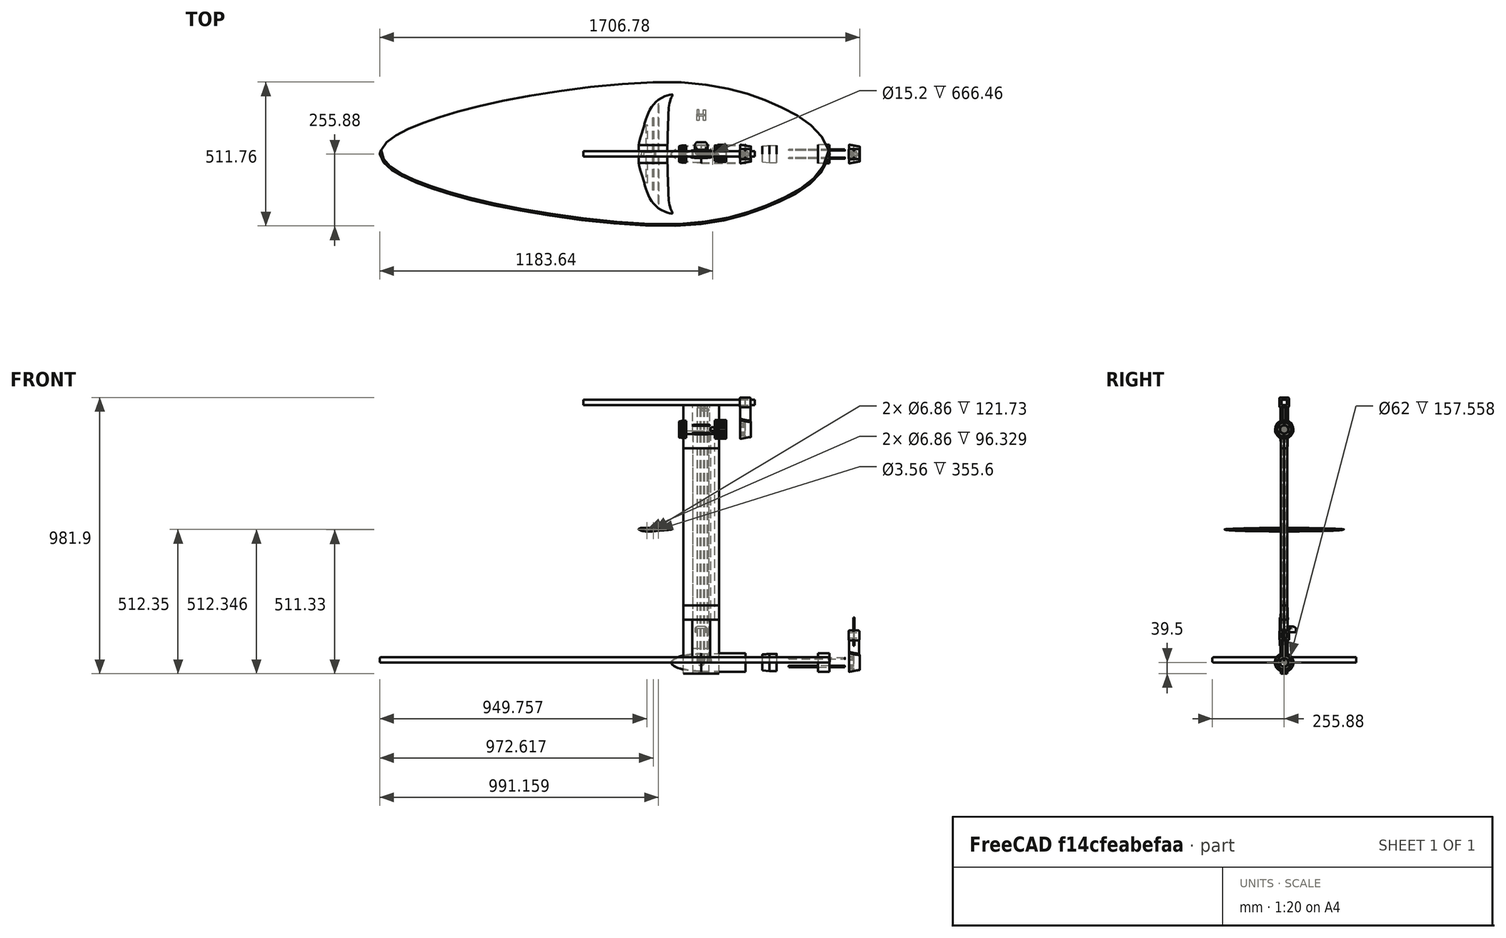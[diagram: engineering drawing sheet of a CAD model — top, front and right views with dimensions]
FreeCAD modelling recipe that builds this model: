
FCSTD DOCUMENT  (FreeCAD 0.21R33771 (Git))
Label: fullboard
License: All rights reserved
LicenseURL: https://en.wikipedia.org/wiki/All_rights_reserved
objects: Sketcher::SketchObject×75, Part::Cylinder×72, PartDesign::Body×57, Part::Cut×45, Part::Box×36, PartDesign::Pad×34, Part::MultiFuse×26, App::DocumentObjectGroup×21, Part::Feature×16, PartDesign::AdditiveLoft×12, Part::RegularPolygon×11, Part::Extrusion×11, App::Part×11, PartDesign::FeatureBase×8, Part::Mirroring×7, Part::Compound×7, Part::Fillet×6, PartDesign::Fillet×4, Mesh::Feature×4, Part::Chamfer×4, +10 more types
note: 500 computed .brp shape members not serialized (recipe doc carries the construction recipe); baked Part::Feature solids carry a one-line shape summary decoded from their .brp

FEATURE [Sketcher::SketchObject] Sketch001
  FullyConstrained = true
  MapMode = 5
  Support = -> [XY_Plane001]
  sketch-geometry (30):
    g0-g6: Circle x7 (B-spline internal-alignment scaffolding for g7; pole/knot coordinates omitted)
    g7: BSplineCurve PolesCount=7 KnotsCount=5 Degree=3 IsPeriodic=0
    g8-g12: GeomPoint x5 (B-spline internal-alignment scaffolding for g7; pole/knot coordinates omitted)
    g13-g19: Circle x7 (B-spline internal-alignment scaffolding for g20; pole/knot coordinates omitted)
    g20: BSplineCurve PolesCount=7 KnotsCount=5 Degree=3 IsPeriodic=0
    g21-g25: GeomPoint x5 (B-spline internal-alignment scaffolding for g20; pole/knot coordinates omitted)
    g26: LineSegment StartX=-28.575 StartY=9.525 StartZ=0 EndX=28.575 EndY=9.525 EndZ=0
    g27: LineSegment StartX=28.575 StartY=9.525 StartZ=0 EndX=28.575 EndY=-9.525 EndZ=0
    g28: LineSegment StartX=28.575 StartY=-9.525 StartZ=0 EndX=-28.575 EndY=-9.525 EndZ=0
    g29: LineSegment StartX=-28.575 StartY=-9.525 StartZ=0 EndX=-28.575 EndY=9.525 EndZ=0
  constraints (40):
    c: Weight(g0) = 1
    c: PointOnObject(g7,g-1)
    c: Equal(g0, g1-g6) x6
    c: PointOnObject(g7,g-1)
    c: InternalAlignment(g0-g6 -> g7) x7
    c: InternalAlignment(g8-g12 -> g7) x5
    c: Weight(g13) = 1
    c: Coincident(g20,g7)
    c: Equal(g13, g14-g19) x6
    c: Coincident(g20,g7)
    c: InternalAlignment(g13-g19 -> g20) x7
    c: InternalAlignment(g21-g25 -> g20) x5
    c: Symmetric(g5,g18,g-1)
    c: Symmetric(g17,g4,g-1)
    c: Symmetric(g16,g3,g-1)
    c: Symmetric(g15,g2,g-1)
    c: Symmetric(g14,g1,g-1)
    c: Coincident(g26,g27)
    c: Coincident(g27,g28)
    c: Coincident(g28,g29)
    c: Coincident(g29,g26)
    c: Horizontal(g26)
    c: Horizontal(g28)
    c: Vertical(g27)
    c: Vertical(g29)
    c: DistanceX(g26,g26) = 57.15
    c: DistanceX(g26,g-1) = 28.575
    c: DistanceY(g27,g26) = 19.05
    c: DistanceY(g27,g-1) = 9.525
    c: DistanceY(g26,g9) = 1
    c: DistanceX(g9,g26) = 1
    c: DistanceY(g26,g3) = 1.5
    c: DistanceY(g26,g11) = 1
    c: DistanceX(g26,g11) = 1
    c: Symmetric(g2,g4,g-2)
    c: DistanceX(g16,g-1) = 0
    c: DistanceX(g-1,g7) = 63.5
    c: DistanceX(g7,g-1) = 63.5
    c: DistanceY(g7,g5) = 7.1374
    c: DistanceX(g5,g7) = 16.5608
FEATURE [PartDesign::Pad] Pad001
  Direction = (0,0,1)
  Length = 863.6
  Length2 = 10
  Profile = -> Sketch001
  ReferenceAxis = -> Sketch001 [N_Axis]
  Type = 0
FEATURE [PartDesign::Body] Body001  label="Mast"
  Group = -> [Sketch001,Pad001]
  Origin = -> Origin001
  Placement = pos=(0,0,-39.497) rot=(0,0,1;0rad)
  Tip = -> Pad001
FEATURE [Sketcher::SketchObject] Sketch003
  FullyConstrained = true
  MapMode = 5
  Support = -> [XY_Plane002]
  sketch-geometry (32):
    g0: GeomPoint X=-1143 Y=0 Z=0
    g1: GeomPoint X=457.2 Y=0 Z=0
    g2-g9: Circle x8 (B-spline internal-alignment scaffolding for g10; pole/knot coordinates omitted)
    g10: BSplineCurve PolesCount=8 KnotsCount=6 Degree=3 IsPeriodic=0
    g11-g16: GeomPoint x6 (B-spline internal-alignment scaffolding for g10; pole/knot coordinates omitted)
    g17-g24: Circle x8 (B-spline internal-alignment scaffolding for g25; pole/knot coordinates omitted)
    g25: BSplineCurve PolesCount=8 KnotsCount=6 Degree=3 IsPeriodic=0
    g26-g31: GeomPoint x6 (B-spline internal-alignment scaffolding for g25; pole/knot coordinates omitted)
  constraints (34):
    c: PointOnObject(g0,g-1)
    c: DistanceX(g0,g-1) = 1143
    c: PointOnObject(g1,g-1)
    c: DistanceX(g-1,g1) = 457.2
    c: Weight(g2) = 1
    c: Coincident(g10,g0)
    c: Equal(g2, g3-g9) x7
    c: Coincident(g10,g1)
    c: InternalAlignment(g2-g9 -> g10) x8
    c: InternalAlignment(g11-g16 -> g10) x6
    c: Weight(g17) = 1
    c: Coincident(g25,g10)
    c: Equal(g17, g18-g24) x7
    c: Coincident(g25,g10)
    c: InternalAlignment(g17-g24 -> g25) x8
    c: InternalAlignment(g26-g31 -> g25) x6
    c: Symmetric(g8,g23,g-1)
    c: Symmetric(g7,g22,g-1)
    c: Symmetric(g6,g21,g-1)
    c: Symmetric(g5,g20,g-1)
    c: Symmetric(g4,g19,g-1)
    c: Symmetric(g3,g18,g-1)
    c: DistanceX(g8) = 435.486
    c: DistanceY(g8) = 90.2091
    c: DistanceX(g7) = 267.582
    c: DistanceY(g7) = 186.903
    c: DistanceX(g6) = -45.8772
    c: DistanceY(g6) = 284.203
    c: DistanceX(g5) = -655.352
    c: DistanceY(g5) = 209.349
    c: DistanceX(g4) = -999.419
    c: DistanceY(g4) = 118.665
    c: DistanceX(g3) = -1133.96
    c: DistanceY(g3) = 47.2203
FEATURE [PartDesign::Pad] Pad002
  Direction = (0,0,1)
  Length = 19.05
  Length2 = 10
  Profile = -> Sketch003
  ReferenceAxis = -> Sketch003 [N_Axis]
  Type = 0
FEATURE [PartDesign::Fillet] Fillet
  Base = -> Pad002 [Edge6]
  BaseFeature = -> Pad002
  Radius = 6.35
  SupportTransform = false
  UseAllEdges = false
FEATURE [PartDesign::Fillet] Fillet001
  Base = -> Fillet [Edge8]
  BaseFeature = -> Fillet
  Radius = 5.08
  SupportTransform = false
  UseAllEdges = false
FEATURE [PartDesign::Body] Body002  label="Board"
  Group = -> [Sketch003,Pad002,Fillet,Fillet001]
  Origin = -> Origin002
  Tip = -> Fillet001
FEATURE [Sketcher::SketchObject] Sketch006
  FullyConstrained = true
  MapMode = 5
  Placement = pos=(0,0,0) rot=(1,0,0;1.5708rad)
  Support = -> [XZ_Plane007]
  sketch-geometry (9):
    g0-g4: Circle x5 (B-spline internal-alignment scaffolding for g5; pole/knot coordinates omitted)
    g5: BSplineCurve PolesCount=5 KnotsCount=3 Degree=3 IsPeriodic=0
    g6: GeomPoint X=-61.1896 Y=1.55299 Z=0
    g7: GeomPoint X=141.928 Y=11.8848 Z=0
    g8: GeomPoint X=-61.1896 Y=1.55299 Z=0
  constraints (15):
    c: Weight(g0) = 1
    c: Equal(g0, g1-g4) x4
    c: Coincident(g5,g0)
    c: InternalAlignment(g0-g4 -> g5) x5
    c: InternalAlignment(g6,g5)
    c: InternalAlignment(g7,g5)
    c: InternalAlignment(g8,g5)
    c: DistanceX(g3) = 103.059
    c: DistanceY(g3) = -5.38655
    c: DistanceX(g1) = 89.7287
    c: DistanceY(g1) = 37.6307
    c: DistanceX(g2) = 187.462
    c: DistanceY(g2) = 7.64757
    c: DistanceX(g5) = -61.1896
    c: DistanceY(g5) = 1.55299
FEATURE [Part::Part2DObjectPython] Clone2D001  label="Wing100"  # Draft 2D object (typed FeaturePython)
  Fuse = false
  Placement = pos=(0,0,0) rot=(1,0,0;1.5708rad)
  Scale = (1,1,1)
FEATURE [Sketcher::SketchObject] Sketch007  label="Wing5"
  FullyConstrained = false
  Placement = pos=(-95.25,284.48,0) rot=(0.995037,0,0.099504;1.5708rad)
  sketch-geometry (1):
    g0: BSplineCurve PolesCount=5 KnotsCount=3 Degree=3 IsPeriodic=0
FEATURE [Sketcher::SketchObject] Sketch008  label="Wing4"
  FullyConstrained = false
  Placement = pos=(-88.9,279.4,0) rot=(0.998205,0,0.059892;1.5708rad)
  sketch-geometry (1):
    g0: BSplineCurve PolesCount=5 KnotsCount=3 Degree=3 IsPeriodic=0
FEATURE [Sketcher::SketchObject] Sketch009  label="Wing3"
  FullyConstrained = false
  Placement = pos=(-63.5,254,0) rot=(0.999201,0,0.039968;1.5708rad)
  sketch-geometry (1):
    g0: BSplineCurve PolesCount=5 KnotsCount=3 Degree=3 IsPeriodic=0
FEATURE [Sketcher::SketchObject] Sketch010  label="Wing2"
  FullyConstrained = false
  Placement = pos=(-25.4,152.4,0) rot=(0.9998,0,0.019996;1.5708rad)
  sketch-geometry (1):
    g0: BSplineCurve PolesCount=5 KnotsCount=3 Degree=3 IsPeriodic=0
FEATURE [Sketcher::SketchObject] Sketch011  label="Wing1"
  FullyConstrained = false
  Placement = pos=(0,-76.2,0) rot=(1,0,0;1.5708rad)
  sketch-geometry (1):
    g0: BSplineCurve PolesCount=5 KnotsCount=3 Degree=3 IsPeriodic=0
FEATURE [Sketcher::SketchObject] Sketch012  label="Wing1.5"
  FullyConstrained = false
  Placement = pos=(-12.7,50.8,0) rot=(-1,0,0;1.5708rad)
  sketch-geometry (1):
    g0: BSplineCurve PolesCount=5 KnotsCount=3 Degree=3 IsPeriodic=0
FEATURE [Sketcher::SketchObject] Sketch013  label="Wing1.25"
  FullyConstrained = false
  Placement = pos=(-3.81,-25.4,0) rot=(-1,0,0;1.5708rad)
  sketch-geometry (1):
    g0: BSplineCurve PolesCount=5 KnotsCount=3 Degree=3 IsPeriodic=0
FEATURE [Sketcher::SketchObject] Sketch014  label="Wing0"
  FullyConstrained = false
  Placement = pos=(0,-139.7,0) rot=(-1,0,0;1.5708rad)
  sketch-geometry (1):
    g0: BSplineCurve PolesCount=5 KnotsCount=3 Degree=3 IsPeriodic=0
FEATURE [Sketcher::SketchObject] Sketch015  label="Wing-1"
  FullyConstrained = false
  Placement = pos=(0,-177.8,0) rot=(-1,0,0;1.5708rad)
  sketch-geometry (1):
    g0: BSplineCurve PolesCount=5 KnotsCount=3 Degree=3 IsPeriodic=0
FEATURE [PartDesign::Body] Body007  label="Front Wing"
  Group = -> [Sketch006,Clone2D001,Sketch015]
  Origin = -> Origin007
FEATURE [PartDesign::AdditiveLoft] AdditiveLoft
  Closed = false
  Placement = pos=(-95.25,284.48,0) rot=(0.995037,0,0.099504;1.5708rad)
  Profile = -> Sketch007 [Edge1]
  Ruled = false
  Sections = -> [Sketch008,Sketch009,Sketch010,Sketch012,Sketch013,Sketch011]
FEATURE [PartDesign::AdditiveLoft] AdditiveLoft001
  BaseFeature = -> AdditiveLoft
  Closed = false
  Placement = pos=(-95.25,284.48,0) rot=(0.995037,0,0.099504;1.5708rad)
  Profile = -> Sketch011
  Ruled = false
  Sections = -> [Sketch014]
FEATURE [Part::Mirroring] Part__Mirroring  label="AdditiveLoft001 (Mirror #1)"
  Base = (0,0,0)
  Normal = (0,0,1)
  Placement = pos=(0,-279.4,3.1e-14) rot=(1,0,0;3.14159rad)
  Source = -> AdditiveLoft001
FEATURE [Sketcher::SketchObject] Sketch016
  FullyConstrained = true
  MapMode = 5
  Support = -> [XY_Plane008]
FEATURE [PartDesign::Body] Body008  label="Body"
  Group = -> [Sketch016]
  Origin = -> Origin008
FEATURE [Sketcher::SketchObject] Sketch017
  FullyConstrained = true
  MapMode = 5
  Placement = pos=(0,0,0) rot=(0.57735,0.57735,0.57735;2.0944rad)
  Support = -> [YZ_Plane009]
  sketch-geometry (4):
    g0: LineSegment StartX=-6.35 StartY=-12.7 StartZ=0 EndX=12.7 EndY=-12.7 EndZ=0
    g1: LineSegment StartX=12.7 StartY=-12.7 StartZ=0 EndX=12.7 EndY=6.35 EndZ=0
    g2: LineSegment StartX=12.7 StartY=6.35 StartZ=0 EndX=-6.35 EndY=6.35 EndZ=0
    g3: LineSegment StartX=-6.35 StartY=6.35 StartZ=0 EndX=-6.35 EndY=-12.7 EndZ=0
  constraints (12):
    c: Coincident(g0,g1)
    c: Coincident(g1,g2)
    c: Coincident(g2,g3)
    c: Coincident(g3,g0)
    c: Horizontal(g0)
    c: Horizontal(g2)
    c: Vertical(g1)
    c: Vertical(g3)
    c: DistanceY(g0,g1) = 19.05
    c: DistanceX(g2,g1) = 19.05
    c: DistanceX(g2) = -6.35
    c: DistanceY(g2) = 6.35
FEATURE [PartDesign::Pad] Pad003
  Direction = (1,-2e-16,3e-16)
  Length = 609.6
  Length2 = 10
  Placement = pos=(0,0,0) rot=(0.57735,0.57735,0.57735;2.0944rad)
  Profile = -> Sketch017
  ReferenceAxis = -> Sketch017 [N_Axis]
  Type = 0
FEATURE [PartDesign::Body] Body009  label="Fuselage"
  Group = -> [Sketch017,Pad003]
  Origin = -> Origin009
  Placement = pos=(-418.998,-3.175,928.688) rot=(0,0,1;0rad)
  Tip = -> Pad003
FEATURE [Sketcher::SketchObject] Sketch018
  FullyConstrained = true
  MapMode = 5
  Support = -> [XY_Plane010]
  sketch-geometry (16):
    g0: LineSegment StartX=-14.2219 StartY=6.35 StartZ=0 EndX=23.8781 EndY=6.35 EndZ=0
    g1: LineSegment StartX=23.8781 StartY=6.35 StartZ=0 EndX=23.8781 EndY=-6.35 EndZ=0
    g2: LineSegment StartX=23.8781 StartY=-6.35 StartZ=0 EndX=-14.2219 EndY=-6.35 EndZ=0
    g3: LineSegment StartX=-14.2219 StartY=-6.35 StartZ=0 EndX=-14.2219 EndY=6.35 EndZ=0
    g4: LineSegment StartX=-12.6217 StartY=4.7498 StartZ=0 EndX=-3.12209 EndY=4.7498 EndZ=0
    g5: LineSegment StartX=-3.12209 StartY=4.7498 StartZ=0 EndX=-3.12209 EndY=-4.7498 EndZ=0
    g6: LineSegment StartX=-3.12209 StartY=-4.7498 StartZ=0 EndX=-12.6217 EndY=-4.7498 EndZ=0
    g7: LineSegment StartX=-12.6217 StartY=-4.7498 StartZ=0 EndX=-12.6217 EndY=4.7498 EndZ=0
    g8: LineSegment StartX=0.078306 StartY=4.7498 StartZ=0 EndX=9.57791 EndY=4.7498 EndZ=0
    g9: LineSegment StartX=9.57791 StartY=4.7498 StartZ=0 EndX=9.57791 EndY=-4.7498 EndZ=0
    g10: LineSegment StartX=9.57791 StartY=-4.7498 StartZ=0 EndX=0.078306 EndY=-4.7498 EndZ=0
    g11: LineSegment StartX=0.078306 StartY=-4.7498 StartZ=0 EndX=0.078306 EndY=4.7498 EndZ=0
    g12: LineSegment StartX=12.7783 StartY=4.7498 StartZ=0 EndX=22.2779 EndY=4.7498 EndZ=0
    g13: LineSegment StartX=22.2779 StartY=4.7498 StartZ=0 EndX=22.2779 EndY=-4.7498 EndZ=0
    g14: LineSegment StartX=22.2779 StartY=-4.7498 StartZ=0 EndX=12.7783 EndY=-4.7498 EndZ=0
    g15: LineSegment StartX=12.7783 StartY=-4.7498 StartZ=0 EndX=12.7783 EndY=4.7498 EndZ=0
  constraints (48):
    c: Coincident(g0,g1)
    c: Coincident(g1,g2)
    c: Coincident(g2,g3)
    c: Coincident(g3,g0)
    c: Horizontal(g0)
    c: Horizontal(g2)
    c: Vertical(g1)
    c: Vertical(g3)
    c: Coincident(g4,g5)
    c: Coincident(g5,g6)
    c: Coincident(g6,g7)
    c: Coincident(g7,g4)
    c: Horizontal(g4)
    c: Horizontal(g6)
    c: Vertical(g5)
    c: Vertical(g7)
    c: Coincident(g8,g9)
    c: Coincident(g9,g10)
    c: Coincident(g10,g11)
    c: Coincident(g11,g8)
    c: Horizontal(g8)
    c: Horizontal(g10)
    c: Vertical(g9)
    c: Vertical(g11)
    c: Coincident(g12,g13)
    c: Coincident(g13,g14)
    c: Coincident(g14,g15)
    c: Coincident(g15,g12)
    c: Horizontal(g12)
    c: Horizontal(g14)
    c: Vertical(g13)
    c: Vertical(g15)
    c: DistanceX(g0,g0) = 38.1
    c: DistanceX(g4,g8) = 3.2004
    c: DistanceX(g8,g12) = 3.2004
    c: DistanceY(g8,g4) = 0
    c: DistanceY(g12,g8) = 0
    c: DistanceY(g2,g6) = 1.6002
    c: DistanceY(g2,g0) = 12.7
    c: DistanceY(g-1,g0) = 6.35
    c: DistanceY(g10,g5) = 0
    c: DistanceY(g14,g9) = 0
    c: DistanceY(g12,g0) = 1.6002
    c: DistanceX(g0,g4) = 1.6002
    c: DistanceX(g0) = -14.2219
    c: DistanceX(g4,g4) = 9.4996
    c: DistanceX(g8,g8) = 9.4996
    c: DistanceX(g12,g12) = 9.4996
FEATURE [PartDesign::Pad] Pad004
  Direction = (0,0,1)
  Length = 914.4
  Length2 = 10
  Profile = -> Sketch018
  ReferenceAxis = -> Sketch018 [N_Axis]
  Type = 0
FEATURE [PartDesign::Body] Body010  label="MastStruct"
  Group = -> [Sketch018,Pad004]
  Origin = -> Origin010
  Tip = -> Pad004
FEATURE [Part::Cylinder] Cylinder
  Angle = 360
  AttacherType = Attacher::AttachEngine3D
  FirstAngle = 0
  Height = 25.4
  Placement = pos=(5.076,0.2286,901.442) rot=(0,0,1;0rad)
  Radius = 3.175
  SecondAngle = 0
FEATURE [Sketcher::SketchObject] Sketch019
  FullyConstrained = true
  MapMode = 5
  Placement = pos=(0,0,0) rot=(1,0,0;1.5708rad)
  Support = -> [XZ_Plane011]
  sketch-geometry (8):
    g0: LineSegment StartX=4.08905 StartY=-9.05917 StartZ=0 EndX=13.6141 EndY=-9.05917 EndZ=0
    g1: LineSegment StartX=13.6141 StartY=-9.05917 StartZ=0 EndX=13.6141 EndY=-18.5842 EndZ=0
    g2: LineSegment StartX=13.6141 StartY=-18.5842 StartZ=0 EndX=4.08905 EndY=-18.5842 EndZ=0
    g3: LineSegment StartX=4.08905 StartY=-18.5842 StartZ=0 EndX=4.08905 EndY=-9.05917 EndZ=0
    g4: LineSegment StartX=4.97805 StartY=-9.94817 StartZ=0 EndX=12.7251 EndY=-9.94817 EndZ=0
    g5: LineSegment StartX=12.7251 StartY=-9.94817 StartZ=0 EndX=12.7251 EndY=-17.6952 EndZ=0
    g6: LineSegment StartX=12.7251 StartY=-17.6952 StartZ=0 EndX=4.97805 EndY=-17.6952 EndZ=0
    g7: LineSegment StartX=4.97805 StartY=-17.6952 StartZ=0 EndX=4.97805 EndY=-9.94817 EndZ=0
  constraints (24):
    c: Coincident(g0,g1)
    c: Coincident(g1,g2)
    c: Coincident(g2,g3)
    c: Coincident(g3,g0)
    c: Horizontal(g0)
    c: Horizontal(g2)
    c: Vertical(g1)
    c: Vertical(g3)
    c: Coincident(g4,g5)
    c: Coincident(g5,g6)
    c: Coincident(g6,g7)
    c: Coincident(g7,g4)
    c: Horizontal(g4)
    c: Horizontal(g6)
    c: Vertical(g5)
    c: Vertical(g7)
    c: DistanceX(g0,g4) = 0.889
    c: DistanceX(g0,g0) = 9.525
    c: DistanceX(g4,g0) = 0.889
    c: DistanceY(g2,g0) = 9.525
    c: DistanceY(g4,g0) = 0.889
    c: DistanceY(g2,g6) = 0.889
    c: DistanceX(g0) = 4.08905
    c: DistanceY(g0) = -9.05917
FEATURE [PartDesign::Pad] Pad005
  Direction = (0,-1,2e-16)
  Length = 9.525
  Length2 = 10
  Placement = pos=(0,0,0) rot=(1,0,0;1.5708rad)
  Profile = -> Sketch019
  ReferenceAxis = -> Sketch019 [N_Axis]
  Type = 0
FEATURE [PartDesign::Body] Body011  label="SteelConnector1"
  Group = -> [Sketch019,Pad005]
  Origin = -> Origin011
  Placement = pos=(-16.764,4.826,923.29) rot=(0,0,1;0rad)
  Tip = -> Pad005
FEATURE [Sketcher::SketchObject] Sketch020
  FullyConstrained = true
  MapMode = 5
  Placement = pos=(0,0,0) rot=(1,0,0;1.5708rad)
  Support = -> [XZ_Plane012]
  sketch-geometry (8):
    g0: LineSegment StartX=4.08905 StartY=-9.05917 StartZ=0 EndX=13.6141 EndY=-9.05917 EndZ=0
    g1: LineSegment StartX=13.6141 StartY=-9.05917 StartZ=0 EndX=13.6141 EndY=-18.5842 EndZ=0
    g2: LineSegment StartX=13.6141 StartY=-18.5842 StartZ=0 EndX=4.08905 EndY=-18.5842 EndZ=0
    g3: LineSegment StartX=4.08905 StartY=-18.5842 StartZ=0 EndX=4.08905 EndY=-9.05917 EndZ=0
    g4: LineSegment StartX=4.97805 StartY=-9.94817 StartZ=0 EndX=12.7251 EndY=-9.94817 EndZ=0
    g5: LineSegment StartX=12.7251 StartY=-9.94817 StartZ=0 EndX=12.7251 EndY=-17.6952 EndZ=0
    g6: LineSegment StartX=12.7251 StartY=-17.6952 StartZ=0 EndX=4.97805 EndY=-17.6952 EndZ=0
    g7: LineSegment StartX=4.97805 StartY=-17.6952 StartZ=0 EndX=4.97805 EndY=-9.94817 EndZ=0
  constraints (24):
    c: Coincident(g0,g1)
    c: Coincident(g1,g2)
    c: Coincident(g2,g3)
    c: Coincident(g3,g0)
    c: Horizontal(g0)
    c: Horizontal(g2)
    c: Vertical(g1)
    c: Vertical(g3)
    c: Coincident(g4,g5)
    c: Coincident(g5,g6)
    c: Coincident(g6,g7)
    c: Coincident(g7,g4)
    c: Horizontal(g4)
    c: Horizontal(g6)
    c: Vertical(g5)
    c: Vertical(g7)
    c: DistanceX(g0,g4) = 0.889
    c: DistanceX(g0,g0) = 9.525
    c: DistanceX(g4,g0) = 0.889
    c: DistanceY(g2,g0) = 9.525
    c: DistanceY(g4,g0) = 0.889
    c: DistanceY(g2,g6) = 0.889
    c: DistanceX(g0) = 4.08905
    c: DistanceY(g0) = -9.05917
FEATURE [PartDesign::Pad] Pad006
  Direction = (0,-1,2e-16)
  Length = 9.525
  Length2 = 10
  Placement = pos=(0,0,0) rot=(1,0,0;1.5708rad)
  Profile = -> Sketch020
  ReferenceAxis = -> Sketch020 [N_Axis]
  Type = 0
FEATURE [PartDesign::Body] Body012  label="SteelConnector2"
  Group = -> [Sketch020,Pad006]
  Origin = -> Origin012
  Placement = pos=(-4.064,4.826,923.29) rot=(0,0,1;0rad)
  Tip = -> Pad006
FEATURE [Sketcher::SketchObject] Sketch021
  FullyConstrained = true
  MapMode = 5
  Placement = pos=(0,0,0) rot=(1,0,0;1.5708rad)
  Support = -> [XZ_Plane013]
  sketch-geometry (8):
    g0: LineSegment StartX=4.08905 StartY=-9.05917 StartZ=0 EndX=13.6141 EndY=-9.05917 EndZ=0
    g1: LineSegment StartX=13.6141 StartY=-9.05917 StartZ=0 EndX=13.6141 EndY=-18.5842 EndZ=0
    g2: LineSegment StartX=13.6141 StartY=-18.5842 StartZ=0 EndX=4.08905 EndY=-18.5842 EndZ=0
    g3: LineSegment StartX=4.08905 StartY=-18.5842 StartZ=0 EndX=4.08905 EndY=-9.05917 EndZ=0
    g4: LineSegment StartX=4.97805 StartY=-9.94817 StartZ=0 EndX=12.7251 EndY=-9.94817 EndZ=0
    g5: LineSegment StartX=12.7251 StartY=-9.94817 StartZ=0 EndX=12.7251 EndY=-17.6952 EndZ=0
    g6: LineSegment StartX=12.7251 StartY=-17.6952 StartZ=0 EndX=4.97805 EndY=-17.6952 EndZ=0
    g7: LineSegment StartX=4.97805 StartY=-17.6952 StartZ=0 EndX=4.97805 EndY=-9.94817 EndZ=0
  constraints (24):
    c: Coincident(g0,g1)
    c: Coincident(g1,g2)
    c: Coincident(g2,g3)
    c: Coincident(g3,g0)
    c: Horizontal(g0)
    c: Horizontal(g2)
    c: Vertical(g1)
    c: Vertical(g3)
    c: Coincident(g4,g5)
    c: Coincident(g5,g6)
    c: Coincident(g6,g7)
    c: Coincident(g7,g4)
    c: Horizontal(g4)
    c: Horizontal(g6)
    c: Vertical(g5)
    c: Vertical(g7)
    c: DistanceX(g0,g4) = 0.889
    c: DistanceX(g0,g0) = 9.525
    c: DistanceX(g4,g0) = 0.889
    c: DistanceY(g2,g0) = 9.525
    c: DistanceY(g4,g0) = 0.889
    c: DistanceY(g2,g6) = 0.889
    c: DistanceX(g0) = 4.08905
    c: DistanceY(g0) = -9.05917
FEATURE [PartDesign::Pad] Pad007
  Direction = (0,-1,2e-16)
  Length = 9.525
  Length2 = 10
  Placement = pos=(0,0,0) rot=(1,0,0;1.5708rad)
  Profile = -> Sketch021
  ReferenceAxis = -> Sketch021 [N_Axis]
  Type = 0
FEATURE [PartDesign::Body] Body013  label="SteelConnector3"
  Group = -> [Sketch021,Pad007]
  Origin = -> Origin013
  Placement = pos=(8.636,4.826,923.29) rot=(0,0,1;0rad)
  Tip = -> Pad007
FEATURE [PartDesign::FeatureBase] BaseFeature
  BaseFeature = -> Cylinder
FEATURE [PartDesign::Body] Body014
  BaseFeature = -> Cylinder
  Group = -> [BaseFeature]
  Origin = -> Origin014
  Placement = pos=(27.2502,0,897.747) rot=(0,-1,0;1.5708rad)
  Tip = -> BaseFeature
FEATURE [App::DocumentObjectGroup] Group  label="Steel Connectors"
  Group = -> [Body011,Body012,Body013,Body014]
FEATURE [Part::Helix] Helix
  Angle = 0
  AttacherType = Attacher::AttachEngine3D
  Height = 50.8
  LocalCoord = 0
  Pitch = 0.999998
  Radius = 2.38125
  SegmentLength = 0
  Style = 1
FEATURE [App::DocumentObjectGroup] Group001  label="Front Wing Support"
FEATURE [Sketcher::SketchObject] Sketch022
  FullyConstrained = true
  MapMode = 5
  Placement = pos=(0,0,0) rot=(1,0,0;1.5708rad)
  Support = -> [XZ_Plane015]
  sketch-geometry (8):
    g0: LineSegment StartX=0 StartY=0 StartZ=0 EndX=12.7 EndY=0 EndZ=0
    g1: LineSegment StartX=12.7 StartY=0 StartZ=0 EndX=12.7 EndY=-12.7 EndZ=0
    g2: LineSegment StartX=12.7 StartY=-12.7 StartZ=0 EndX=0 EndY=-12.7 EndZ=0
    g3: LineSegment StartX=0 StartY=-12.7 StartZ=0 EndX=0 EndY=0 EndZ=0
    g4: LineSegment StartX=1.6002 StartY=-1.6002 StartZ=0 EndX=11.0998 EndY=-1.6002 EndZ=0
    g5: LineSegment StartX=11.0998 StartY=-1.6002 StartZ=0 EndX=11.0998 EndY=-11.0998 EndZ=0
    g6: LineSegment StartX=11.0998 StartY=-11.0998 StartZ=0 EndX=1.6002 EndY=-11.0998 EndZ=0
    g7: LineSegment StartX=1.6002 StartY=-11.0998 StartZ=0 EndX=1.6002 EndY=-1.6002 EndZ=0
  constraints (23):
    c: Coincident(g0,g1)
    c: Coincident(g1,g2)
    c: Coincident(g2,g3)
    c: Coincident(g3,g0)
    c: Horizontal(g0)
    c: Horizontal(g2)
    c: Vertical(g1)
    c: Vertical(g3)
    c: Coincident(g0,g-1)
    c: Coincident(g4,g5)
    c: Coincident(g5,g6)
    c: Coincident(g6,g7)
    c: Coincident(g7,g4)
    c: Horizontal(g4)
    c: Horizontal(g6)
    c: Vertical(g5)
    c: Vertical(g7)
    c: DistanceX(g2,g1) = 12.7
    c: DistanceY(g2,g0) = 12.7
    c: DistanceY(g2,g6) = 1.6002
    c: DistanceY(g4,g0) = 1.6002
    c: DistanceX(g0,g4) = 1.6002
    c: DistanceX(g4,g0) = 1.6002
FEATURE [PartDesign::Pad] Pad008
  Direction = (0,-1,-2e-16)
  Length = 152.4
  Length2 = 10
  Placement = pos=(0,0,0) rot=(1,0,0;1.5708rad)
  Profile = -> Sketch022
  ReferenceAxis = -> Sketch022 [N_Axis]
  Type = 0
FEATURE [PartDesign::Body] Body015  label="Body016"
  Group = -> [Sketch022,Pad008]
  Origin = -> Origin015
  Placement = pos=(-413.918,76.2,939.8) rot=(0,0,1;0rad)
  Tip = -> Pad008
FEATURE [Sketcher::SketchObject] Sketch023
  FullyConstrained = true
  MapMode = 5
  Placement = pos=(0,0,0) rot=(1,0,0;1.5708rad)
  Support = -> [XZ_Plane016]
  sketch-geometry (8):
    g0: LineSegment StartX=0 StartY=0 StartZ=0 EndX=12.7 EndY=0 EndZ=0
    g1: LineSegment StartX=12.7 StartY=0 StartZ=0 EndX=12.7 EndY=-12.7 EndZ=0
    g2: LineSegment StartX=12.7 StartY=-12.7 StartZ=0 EndX=0 EndY=-12.7 EndZ=0
    g3: LineSegment StartX=0 StartY=-12.7 StartZ=0 EndX=0 EndY=0 EndZ=0
    g4: LineSegment StartX=1.6002 StartY=-1.6002 StartZ=0 EndX=11.0998 EndY=-1.6002 EndZ=0
    g5: LineSegment StartX=11.0998 StartY=-1.6002 StartZ=0 EndX=11.0998 EndY=-11.0998 EndZ=0
    g6: LineSegment StartX=11.0998 StartY=-11.0998 StartZ=0 EndX=1.6002 EndY=-11.0998 EndZ=0
    g7: LineSegment StartX=1.6002 StartY=-11.0998 StartZ=0 EndX=1.6002 EndY=-1.6002 EndZ=0
  constraints (23):
    c: Coincident(g0,g1)
    c: Coincident(g1,g2)
    c: Coincident(g2,g3)
    c: Coincident(g3,g0)
    c: Horizontal(g0)
    c: Horizontal(g2)
    c: Vertical(g1)
    c: Vertical(g3)
    c: Coincident(g0,g-1)
    c: Coincident(g4,g5)
    c: Coincident(g5,g6)
    c: Coincident(g6,g7)
    c: Coincident(g7,g4)
    c: Horizontal(g4)
    c: Horizontal(g6)
    c: Vertical(g5)
    c: Vertical(g7)
    c: DistanceX(g2,g1) = 12.7
    c: DistanceY(g2,g0) = 12.7
    c: DistanceY(g2,g6) = 1.6002
    c: DistanceY(g4,g0) = 1.6002
    c: DistanceX(g0,g4) = 1.6002
    c: DistanceX(g4,g0) = 1.6002
FEATURE [PartDesign::Pad] Pad009
  Direction = (0,-1,-2e-16)
  Length = 381
  Length2 = 10
  Placement = pos=(0,0,0) rot=(1,0,0;1.5708rad)
  Profile = -> Sketch023
  ReferenceAxis = -> Sketch023 [N_Axis]
  Type = 0
FEATURE [PartDesign::Body] Body016  label="Body017"
  Group = -> [Sketch023,Pad009]
  Origin = -> Origin016
  Placement = pos=(-393.598,190.5,939.8) rot=(0,0,1;0rad)
  Tip = -> Pad009
FEATURE [Sketcher::SketchObject] Sketch024
  FullyConstrained = true
  MapMode = 5
  Placement = pos=(0,0,0) rot=(1,0,0;1.5708rad)
  Support = -> [XZ_Plane017]
  sketch-geometry (8):
    g0: LineSegment StartX=0 StartY=0 StartZ=0 EndX=12.7 EndY=0 EndZ=0
    g1: LineSegment StartX=12.7 StartY=0 StartZ=0 EndX=12.7 EndY=-12.7 EndZ=0
    g2: LineSegment StartX=12.7 StartY=-12.7 StartZ=0 EndX=0 EndY=-12.7 EndZ=0
    g3: LineSegment StartX=0 StartY=-12.7 StartZ=0 EndX=0 EndY=0 EndZ=0
    g4: LineSegment StartX=1.6002 StartY=-1.6002 StartZ=0 EndX=11.0998 EndY=-1.6002 EndZ=0
    g5: LineSegment StartX=11.0998 StartY=-1.6002 StartZ=0 EndX=11.0998 EndY=-11.0998 EndZ=0
    g6: LineSegment StartX=11.0998 StartY=-11.0998 StartZ=0 EndX=1.6002 EndY=-11.0998 EndZ=0
    g7: LineSegment StartX=1.6002 StartY=-11.0998 StartZ=0 EndX=1.6002 EndY=-1.6002 EndZ=0
  constraints (23):
    c: Coincident(g0,g1)
    c: Coincident(g1,g2)
    c: Coincident(g2,g3)
    c: Coincident(g3,g0)
    c: Horizontal(g0)
    c: Horizontal(g2)
    c: Vertical(g1)
    c: Vertical(g3)
    c: Coincident(g0,g-1)
    c: Coincident(g4,g5)
    c: Coincident(g5,g6)
    c: Coincident(g6,g7)
    c: Coincident(g7,g4)
    c: Horizontal(g4)
    c: Horizontal(g6)
    c: Vertical(g5)
    c: Vertical(g7)
    c: DistanceX(g2,g1) = 12.7
    c: DistanceY(g2,g0) = 12.7
    c: DistanceY(g2,g6) = 1.6002
    c: DistanceY(g4,g0) = 1.6002
    c: DistanceX(g0,g4) = 1.6002
    c: DistanceX(g4,g0) = 1.6002
FEATURE [PartDesign::Pad] Pad010
  Direction = (0,-1,-2e-16)
  Length = 50.8
  Length2 = 10
  Placement = pos=(0,0,0) rot=(1,0,0;1.5708rad)
  Profile = -> Sketch024
  ReferenceAxis = -> Sketch024 [N_Axis]
  Type = 0
FEATURE [PartDesign::Body] Body017  label="Body018"
  Group = -> [Sketch024,Pad010]
  Origin = -> Origin017
  Placement = pos=(139.7,-6.35,914.4) rot=(0,0,1;1.5708rad)
  Tip = -> Pad010
FEATURE [Sketcher::SketchObject] Sketch025
  FullyConstrained = true
  MapMode = 5
  Placement = pos=(0,0,0) rot=(1,0,0;1.5708rad)
  Support = -> [XZ_Plane018]
  sketch-geometry (8):
    g0: LineSegment StartX=0 StartY=0 StartZ=0 EndX=12.7 EndY=0 EndZ=0
    g1: LineSegment StartX=12.7 StartY=0 StartZ=0 EndX=12.7 EndY=-12.7 EndZ=0
    g2: LineSegment StartX=12.7 StartY=-12.7 StartZ=0 EndX=0 EndY=-12.7 EndZ=0
    g3: LineSegment StartX=0 StartY=-12.7 StartZ=0 EndX=0 EndY=0 EndZ=0
    g4: LineSegment StartX=1.6002 StartY=-1.6002 StartZ=0 EndX=11.0998 EndY=-1.6002 EndZ=0
    g5: LineSegment StartX=11.0998 StartY=-1.6002 StartZ=0 EndX=11.0998 EndY=-11.0998 EndZ=0
    g6: LineSegment StartX=11.0998 StartY=-11.0998 StartZ=0 EndX=1.6002 EndY=-11.0998 EndZ=0
    g7: LineSegment StartX=1.6002 StartY=-11.0998 StartZ=0 EndX=1.6002 EndY=-1.6002 EndZ=0
  constraints (23):
    c: Coincident(g0,g1)
    c: Coincident(g1,g2)
    c: Coincident(g2,g3)
    c: Coincident(g3,g0)
    c: Horizontal(g0)
    c: Horizontal(g2)
    c: Vertical(g1)
    c: Vertical(g3)
    c: Coincident(g0,g-1)
    c: Coincident(g4,g5)
    c: Coincident(g5,g6)
    c: Coincident(g6,g7)
    c: Coincident(g7,g4)
    c: Horizontal(g4)
    c: Horizontal(g6)
    c: Vertical(g5)
    c: Vertical(g7)
    c: DistanceX(g2,g1) = 12.7
    c: DistanceY(g2,g0) = 12.7
    c: DistanceY(g2,g6) = 1.6002
    c: DistanceY(g4,g0) = 1.6002
    c: DistanceX(g0,g4) = 1.6002
    c: DistanceX(g4,g0) = 1.6002
FEATURE [PartDesign::Pad] Pad011
  Direction = (0,-1,-2e-16)
  Length = 457.2
  Length2 = 10
  Placement = pos=(0,0,0) rot=(1,0,0;1.5708rad)
  Profile = -> Sketch025
  ReferenceAxis = -> Sketch025 [N_Axis]
  Type = 0
FEATURE [PartDesign::Body] Body018  label="Body019"
  Group = -> [Sketch025,Pad011]
  Origin = -> Origin018
  Placement = pos=(-368.198,228.6,939.8) rot=(0,0,1;0rad)
  Tip = -> Pad011
FEATURE [Sketcher::SketchObject] Sketch027
  FullyConstrained = true
  MapMode = 5
  Placement = pos=(0,0,0) rot=(1,0,0;1.5708rad)
  Support = -> [XZ_Plane020]
  sketch-geometry (8):
    g0: LineSegment StartX=0 StartY=0 StartZ=0 EndX=12.7 EndY=0 EndZ=0
    g1: LineSegment StartX=12.7 StartY=0 StartZ=0 EndX=12.7 EndY=-12.7 EndZ=0
    g2: LineSegment StartX=12.7 StartY=-12.7 StartZ=0 EndX=0 EndY=-12.7 EndZ=0
    g3: LineSegment StartX=0 StartY=-12.7 StartZ=0 EndX=0 EndY=0 EndZ=0
    g4: LineSegment StartX=1.6002 StartY=-1.6002 StartZ=0 EndX=11.0998 EndY=-1.6002 EndZ=0
    g5: LineSegment StartX=11.0998 StartY=-1.6002 StartZ=0 EndX=11.0998 EndY=-11.0998 EndZ=0
    g6: LineSegment StartX=11.0998 StartY=-11.0998 StartZ=0 EndX=1.6002 EndY=-11.0998 EndZ=0
    g7: LineSegment StartX=1.6002 StartY=-11.0998 StartZ=0 EndX=1.6002 EndY=-1.6002 EndZ=0
  constraints (23):
    c: Coincident(g0,g1)
    c: Coincident(g1,g2)
    c: Coincident(g2,g3)
    c: Coincident(g3,g0)
    c: Horizontal(g0)
    c: Horizontal(g2)
    c: Vertical(g1)
    c: Vertical(g3)
    c: Coincident(g0,g-1)
    c: Coincident(g4,g5)
    c: Coincident(g5,g6)
    c: Coincident(g6,g7)
    c: Coincident(g7,g4)
    c: Horizontal(g4)
    c: Horizontal(g6)
    c: Vertical(g5)
    c: Vertical(g7)
    c: DistanceX(g2,g1) = 12.7
    c: DistanceY(g2,g0) = 12.7
    c: DistanceY(g2,g6) = 1.6002
    c: DistanceY(g4,g0) = 1.6002
    c: DistanceX(g0,g4) = 1.6002
    c: DistanceX(g4,g0) = 1.6002
FEATURE [PartDesign::Pad] Pad013
  Direction = (0,-1,-2e-16)
  Length = 584.2
  Length2 = 10
  Placement = pos=(0,0,0) rot=(1,0,0;1.5708rad)
  Profile = -> Sketch027
  ReferenceAxis = -> Sketch027 [N_Axis]
  Type = 0
FEATURE [PartDesign::Body] Body020  label="Body021"
  Group = -> [Sketch027,Pad013]
  Origin = -> Origin020
  Placement = pos=(-347.878,292.1,939.8) rot=(0,0,1;0rad)
  Tip = -> Pad013
FEATURE [Part::Cylinder] Cylinder001
  Angle = 360
  AttacherType = Attacher::AttachEngine3D
  FirstAngle = 0
  Height = 9.906
  Placement = pos=(5.08,-0.86,911.35) rot=(0,0,1;0rad)
  Radius = 3.048
  SecondAngle = 0
FEATURE [Part::Cylinder] Cylinder002
  Angle = 360
  AttacherType = Attacher::AttachEngine3D
  FirstAngle = 0
  Height = 660.4
  Placement = pos=(-295.91,-330.2,937.768) rot=(-1,0,0;1.5708rad)
  Radius = 3.175
  SecondAngle = 0
FEATURE [Part::Cylinder] Cylinder004
  Angle = 360
  AttacherType = Attacher::AttachEngine3D
  FirstAngle = 0
  Height = 101.6
  Placement = pos=(144.78,-50.8,905.256) rot=(-1,0,0;1.5708rad)
  Radius = 1.5875
  SecondAngle = 0
  expr: .Placement.Base.z = 2.97 '
FEATURE [Part::Cylinder] Cylinder005
  Angle = 360
  AttacherType = Attacher::AttachEngine3D
  FirstAngle = 0
  Height = 203.2
  Placement = pos=(162.56,-101.6,905.26) rot=(-1,0,0;1.5708rad)
  Radius = 1.5875
  SecondAngle = 0
FEATURE [Part::Cylinder] Cylinder006
  Angle = 360
  AttacherType = Attacher::AttachEngine3D
  FirstAngle = 0
  Height = 304.8
  Placement = pos=(180.34,-152.4,905.26) rot=(-1,0,0;1.5708rad)
  Radius = 1.5875
  SecondAngle = 0
FEATURE [Part::Cylinder] Cylinder007
  Angle = 360
  AttacherType = Attacher::AttachEngine3D
  FirstAngle = 0
  Height = 355.6
  Placement = pos=(201.422,-177.8,903.935) rot=(-1,0,0;1.5708rad)
  Radius = 1.5875
  SecondAngle = 0
  expr: .Placement.Base.z = 2.97 '
FEATURE [Part::Cylinder] Cylinder008
  Angle = 360
  AttacherType = Attacher::AttachEngine3D
  FirstAngle = 0
  Height = 762
  Placement = pos=(-267.208,-381,942.086) rot=(-1,0,0;1.5708rad)
  Radius = 3.175
  SecondAngle = 0
FEATURE [Part::Box] Box  label="Cube"
  AttacherType = Attacher::AttachEngine3D
  Height = 127
  Length = 914.4
  Placement = pos=(-692,-203.2,25.4) rot=(0,0,1;0rad)
  Width = 406.4
FEATURE [Part::Cylinder] Cylinder009  label="BatteryCell001"
  Angle = 360
  AttacherType = Attacher::AttachEngine3D
  FirstAngle = 0
  Height = 69.85
  Placement = pos=(0,45.212,36.9999) rot=(0,0,1;0rad)
  Radius = 10.414
  SecondAngle = 0
FEATURE [Part::Cylinder] Cylinder010  label="BatteryCell002"
  Angle = 360
  AttacherType = Attacher::AttachEngine3D
  FirstAngle = 0
  Height = 69.85
  Placement = pos=(0,22.606,36.9999) rot=(0,0,1;0rad)
  Radius = 10.414
  SecondAngle = 0
FEATURE [Part::Cylinder] Cylinder011  label="BatteryCell003"
  Angle = 360
  AttacherType = Attacher::AttachEngine3D
  FirstAngle = 0
  Height = 69.85
  Placement = pos=(0,0,36.9999) rot=(0,0,1;0rad)
  Radius = 10.414
  SecondAngle = 0
FEATURE [Part::Cylinder] Cylinder012  label="BatteryCell004"
  Angle = 360
  AttacherType = Attacher::AttachEngine3D
  FirstAngle = 0
  Height = 69.85
  Placement = pos=(0,-22.606,36.9999) rot=(0,0,1;0rad)
  Radius = 10.414
  SecondAngle = 0
FEATURE [Part::Cylinder] Cylinder013  label="BatteryCell005"
  Angle = 360
  AttacherType = Attacher::AttachEngine3D
  FirstAngle = 0
  Height = 69.85
  Placement = pos=(0,-45.212,36.9999) rot=(0,0,1;0rad)
  Radius = 10.414
  SecondAngle = 0
FEATURE [Part::Cylinder] Cylinder014  label="BatteryCell006"
  Angle = 360
  AttacherType = Attacher::AttachEngine3D
  FirstAngle = 0
  Height = 69.85
  Placement = pos=(0,-67.818,36.9999) rot=(0,0,1;0rad)
  Radius = 10.414
  SecondAngle = 0
FEATURE [Part::Cylinder] Cylinder003  label="BatteryCell000"
  Angle = 360
  AttacherType = Attacher::AttachEngine3D
  FirstAngle = 0
  Height = 69.85
  Placement = pos=(0,67.818,36.9999) rot=(0,0,1;0rad)
  Radius = 10.414
  SecondAngle = 0
FEATURE [Part::Compound] Compound  label="Row"
  Links = -> [Cylinder014,Cylinder013,Cylinder012,Cylinder011,Cylinder010,Cylinder009,Cylinder003]
  Placement = pos=(-254,0,0) rot=(0,0,1;0rad)
FEATURE [App::DocumentObjectGroup] Group004  label="Base"
  Group = -> [Cylinder003,Cylinder009,Cylinder010,Cylinder011,Cylinder012,Cylinder013,Cylinder014]
FEATURE [Part::Cylinder] Cylinder015  label="BatteryCell007"
  Angle = 360
  AttacherType = Attacher::AttachEngine3D
  FirstAngle = 0
  Height = 69.85
  Placement = pos=(0,67.818,36.9999) rot=(0,0,1;0rad)
  Radius = 10.414
  SecondAngle = 0
FEATURE [Part::Cylinder] Cylinder016  label="BatteryCell008"
  Angle = 360
  AttacherType = Attacher::AttachEngine3D
  FirstAngle = 0
  Height = 69.85
  Placement = pos=(0,45.212,36.9999) rot=(0,0,1;0rad)
  Radius = 10.414
  SecondAngle = 0
FEATURE [Part::Cylinder] Cylinder017  label="BatteryCell009"
  Angle = 360
  AttacherType = Attacher::AttachEngine3D
  FirstAngle = 0
  Height = 69.85
  Placement = pos=(0,22.606,36.9999) rot=(0,0,1;0rad)
  Radius = 10.414
  SecondAngle = 0
FEATURE [Part::Cylinder] Cylinder018  label="BatteryCell010"
  Angle = 360
  AttacherType = Attacher::AttachEngine3D
  FirstAngle = 0
  Height = 69.85
  Placement = pos=(0,0,36.9999) rot=(0,0,1;0rad)
  Radius = 10.414
  SecondAngle = 0
FEATURE [Part::Cylinder] Cylinder019  label="BatteryCell011"
  Angle = 360
  AttacherType = Attacher::AttachEngine3D
  FirstAngle = 0
  Height = 69.85
  Placement = pos=(0,-22.606,36.9999) rot=(0,0,1;0rad)
  Radius = 10.414
  SecondAngle = 0
FEATURE [Part::Cylinder] Cylinder020  label="BatteryCell012"
  Angle = 360
  AttacherType = Attacher::AttachEngine3D
  FirstAngle = 0
  Height = 69.85
  Placement = pos=(0,-45.212,36.9999) rot=(0,0,1;0rad)
  Radius = 10.414
  SecondAngle = 0
FEATURE [Part::Cylinder] Cylinder021  label="BatteryCell013"
  Angle = 360
  AttacherType = Attacher::AttachEngine3D
  FirstAngle = 0
  Height = 69.85
  Placement = pos=(0,-67.818,36.9999) rot=(0,0,1;0rad)
  Radius = 10.414
  SecondAngle = 0
FEATURE [Part::Compound] Compound001  label="Row001"
  Links = -> [Cylinder021,Cylinder020,Cylinder019,Cylinder018,Cylinder017,Cylinder016,Cylinder015]
  Placement = pos=(-276.606,0,143.84) rot=(0,1,0;3.14159rad)
FEATURE [App::DocumentObjectGroup] Group002  label="Battery"
  Group = -> [Compound,Group004,Compound001]
FEATURE [Sketcher::SketchObject] Sketch028
  FullyConstrained = true
  MapMode = 5
  Support = -> [XY_Plane028]
  sketch-geometry (16):
    g0: LineSegment StartX=-15.1 StartY=-15.1 StartZ=0 EndX=-15.1 EndY=7.4 EndZ=0
    g1: LineSegment StartX=15.1 StartY=7.4 StartZ=0 EndX=15.1 EndY=-15.1 EndZ=0
    g2: LineSegment StartX=15.1 StartY=7.4 StartZ=0 EndX=12.1 EndY=7.4 EndZ=0
    g3: LineSegment StartX=12.1 StartY=7.4 StartZ=0 EndX=12.1 EndY=-0.1 EndZ=0
    g4: LineSegment StartX=12.1 StartY=-0.1 StartZ=0 EndX=11.1 EndY=-0.1 EndZ=0
    g5: LineSegment StartX=11.1 StartY=-0.1 StartZ=0 EndX=11.1 EndY=7.4 EndZ=0
    g6: LineSegment StartX=11.1 StartY=7.4 StartZ=0 EndX=-11.1 EndY=7.4 EndZ=0
    g7: LineSegment StartX=-11.1 StartY=7.4 StartZ=0 EndX=-11.1 EndY=-0.1 EndZ=0
    g8: LineSegment StartX=-11.1 StartY=-0.1 StartZ=0 EndX=-12.1 EndY=-0.1 EndZ=0
    g9: LineSegment StartX=-12.1 StartY=-0.1 StartZ=0 EndX=-12.1 EndY=7.4 EndZ=0
    g10: LineSegment StartX=-12.1 StartY=7.4 StartZ=0 EndX=-15.1 EndY=7.4 EndZ=0
    g11: LineSegment StartX=15.1 StartY=-15.1 StartZ=0 EndX=7.6 EndY=-15.1 EndZ=0
    g12: LineSegment StartX=7.6 StartY=-15.1 StartZ=0 EndX=7.6 EndY=0.1 EndZ=0
    g13: LineSegment StartX=7.6 StartY=0.1 StartZ=0 EndX=-7.6 EndY=0.1 EndZ=0
    g14: LineSegment StartX=-7.6 StartY=0.1 StartZ=0 EndX=-7.6 EndY=-15.1 EndZ=0
    g15: LineSegment StartX=-7.6 StartY=-15.1 StartZ=0 EndX=-15.1 EndY=-15.1 EndZ=0
  constraints (41):
    c: Vertical(g0)
    c: DistanceX(g0,g1) = 30.2
    c: Coincident(g1,g2)
    c: Horizontal(g2)
    c: Coincident(g2,g3)
    c: Vertical(g3)
    c: Coincident(g3,g4)
    c: Coincident(g4,g5)
    c: Vertical(g5)
    c: Coincident(g5,g6)
    c: Coincident(g6,g7)
    c: Coincident(g7,g8)
    c: Coincident(g8,g9)
    c: Coincident(g9,g10)
    c: Coincident(g10,g0)
    c: Horizontal(g4)
    c: DistanceX(g4,g3) = 1
    c: DistanceY(g5,g2) = 0
    c: DistanceX(g2,g1) = 3
    c: Symmetric(g1,g0,g-2)
    c: Symmetric(g5,g6,g-2)
    c: Symmetric(g7,g4,g-2)
    c: Symmetric(g8,g3,g-2)
    c: Symmetric(g2,g9,g-2)
    c: Symmetric(g1,g0,g-2)
    c: DistanceY(g4,g5) = 7.5
    c: DistanceY(g1,g1) = 22.5
    c: Coincident(g1,g11)
    c: Horizontal(g11)
    c: Coincident(g11,g12)
    c: Vertical(g12)
    c: Coincident(g12,g13)
    c: Coincident(g13,g14)
    c: Vertical(g14)
    c: Coincident(g14,g15)
    c: Coincident(g15,g0)
    c: Horizontal(g15)
    c: Symmetric(g12,g13,g-2)
    c: DistanceX(g11,g1) = 7.5
    c: Equal(g12,g13)
    c: DistanceY(g1,g-1) = 15.1
FEATURE [PartDesign::Pad] Pad014
  Direction = (0,0,1)
  Length = 0.15
  Length2 = 10
  Profile = -> Sketch028
  ReferenceAxis = -> Sketch028 [N_Axis]
  Type = 0
FEATURE [Sketcher::SketchObject] Sketch034
  FullyConstrained = false
  MapMode = 5
  Support = -> [XY_Plane026]
  sketch-geometry (22):
    g0: LineSegment StartX=-15.1 StartY=-15.1 StartZ=0 EndX=-15.1 EndY=7.4 EndZ=0
    g1: LineSegment StartX=15.1 StartY=7.4 StartZ=0 EndX=15.1 EndY=-15.1 EndZ=0
    g2: LineSegment StartX=12.1 StartY=7.4 StartZ=0 EndX=12.1 EndY=-0.1 EndZ=0
    g3: LineSegment StartX=12.1 StartY=-0.1 StartZ=0 EndX=11.1 EndY=-0.1 EndZ=0
    g4: LineSegment StartX=11.1 StartY=-0.1 StartZ=0 EndX=11.1 EndY=7.4 EndZ=0
    g5: LineSegment StartX=-11.1 StartY=7.4 StartZ=0 EndX=-11.1 EndY=-0.1 EndZ=0
    g6: LineSegment StartX=-11.1 StartY=-0.1 StartZ=0 EndX=-12.1 EndY=-0.1 EndZ=0
    g7: LineSegment StartX=-12.1 StartY=-0.1 StartZ=0 EndX=-12.1 EndY=7.4 EndZ=0
    g8: LineSegment StartX=15.1 StartY=-15.1 StartZ=0 EndX=7.6 EndY=-15.1 EndZ=0
    g9: LineSegment StartX=7.6 StartY=-15.1 StartZ=0 EndX=7.6 EndY=0.1 EndZ=0
    g10: LineSegment StartX=7.6 StartY=0.1 StartZ=0 EndX=-7.6 EndY=0.1 EndZ=0
    g11: LineSegment StartX=-7.6 StartY=0.1 StartZ=0 EndX=-7.6 EndY=-15.1 EndZ=0
    g12: LineSegment StartX=-7.6 StartY=-15.1 StartZ=0 EndX=-15.1 EndY=-15.1 EndZ=0
    g13: LineSegment StartX=7.6 StartY=7.4 StartZ=0 EndX=7.6 EndY=22.4 EndZ=0
    g14: LineSegment StartX=7.6 StartY=22.4 StartZ=0 EndX=15.1 EndY=22.4 EndZ=0
    g15: LineSegment StartX=15.1 StartY=22.4 StartZ=0 EndX=15.1 EndY=7.4 EndZ=0
    g16: LineSegment StartX=-7.6 StartY=7.4 StartZ=0 EndX=-7.6 EndY=22.4 EndZ=0
    g17: LineSegment StartX=-7.6 StartY=22.4 StartZ=0 EndX=-15.1 EndY=22.4 EndZ=0
    g18: LineSegment StartX=-15.1 StartY=22.4 StartZ=0 EndX=-15.1 EndY=7.4 EndZ=0
    g19: LineSegment StartX=-7.6 StartY=7.4 StartZ=0 EndX=7.6 EndY=7.4 EndZ=0
    g20: LineSegment StartX=-12.1 StartY=7.4 StartZ=0 EndX=-11.1 EndY=7.4 EndZ=0
    g21: LineSegment StartX=11.1 StartY=7.4 StartZ=0 EndX=12.1 EndY=7.4 EndZ=0
  constraints (60):
    c: Vertical(g0)
    c: DistanceX(g0,g1) = 30.2
    c: Vertical(g2)
    c: Coincident(g2,g3)
    c: Coincident(g3,g4)
    c: Vertical(g4)
    c: Coincident(g5,g6)
    c: Coincident(g6,g7)
    c: Horizontal(g3)
    c: DistanceX(g3,g2) = 1
    c: DistanceX(g2,g1) = 3
    c: Symmetric(g1,g0,g-2)
    c: Symmetric(g4,g5,g-2)
    c: Symmetric(g5,g3,g-2)
    c: Symmetric(g6,g2,g-2)
    c: Symmetric(g2,g7,g-2)
    c: Symmetric(g1,g0,g-2)
    c: DistanceY(g1,g1) = 22.5
    c: Coincident(g1,g8)
    c: Horizontal(g8)
    c: Coincident(g8,g9)
    c: Vertical(g9)
    c: Coincident(g9,g10)
    c: Coincident(g10,g11)
    c: Vertical(g11)
    c: Coincident(g11,g12)
    c: Coincident(g12,g0)
    c: Horizontal(g12)
    c: Symmetric(g9,g10,g-2)
    c: DistanceX(g8,g1) = 7.5
    c: Equal(g9,g10)
    c: DistanceY(g1,g-1) = 15.1
    c: Coincident(g13,g14)
    c: Coincident(g14,g15)
    c: Horizontal(g14)
    c: Vertical(g13)
    c: Vertical(g15)
    c: Coincident(g16,g17)
    c: Coincident(g17,g18)
    c: Horizontal(g17)
    c: Vertical(g16)
    c: Vertical(g18)
    c: DistanceY(g13,g13) = 15
    c: DistanceY(g16,g16) = 15
    c: DistanceX(g13,g14) = 7.5
    c: DistanceX(g17,g16) = 7.5
    c: Coincident(g19,g16)
    c: Coincident(g19,g13)
    c: Horizontal(g19)
    c: Coincident(g20,g7)
    c: Coincident(g20,g5)
    c: Horizontal(g20)
    c: Coincident(g21,g4)
    c: Coincident(g21,g2)
    c: DistanceX(g16) = -7.6
    c: DistanceY(g16) = 7.4
    c: DistanceX(g13) = 7.6
    c: DistanceY(g7) = 7.4
    c: DistanceY(g1,g15) = 0
    c: DistanceY(g0,g18) = 0
FEATURE [PartDesign::Pad] Pad020
  Direction = (0,0,1)
  Length = 0.15
  Length2 = 10
  Profile = -> Sketch034
  ReferenceAxis = -> Sketch034 [N_Axis]
  Type = 0
FEATURE [PartDesign::Body] Body026  label="Battery Connector006"
  Group = -> [Sketch034,Pad020]
  Origin = -> Origin026
  Placement = pos=(0,135,0) rot=(0,0,1;0rad)
  Tip = -> Pad020
FEATURE [Part::Feature] Part__Feature  label="21700Battery"
  shape: bbox 22.95 x 22.95 x 70.61 mm, 44 faces (baked)
FEATURE [Part::Box] Box001  label="Cube001"
  AttacherType = Attacher::AttachEngine3D
  Height = 50.8
  Length = 38.1
  Placement = pos=(1.6002,1.6002,1.6002) rot=(0,0,1;0rad)
  Width = 12.7
FEATURE [Part::Box] Box002  label="Cube002"
  AttacherType = Attacher::AttachEngine3D
  Height = 50.8
  Length = 41.3004
  Width = 15.9004
FEATURE [Part::Cut] Cut
  Base = -> Box002
  Placement = pos=(-15.8242,-7.874,-1.6002) rot=(0,0,1;0rad)
  Tool = -> Box001
FEATURE [Part::Box] Box003  label="Cube003"
  AttacherType = Attacher::AttachEngine3D
  Height = 52.4002
  Length = 44.5008
  Placement = pos=(-17.4244,-9.4742,-3.2004) rot=(0,0,1;0rad)
  Width = 19.1008
FEATURE [Part::Box] Box004  label="Cube004"
  AttacherType = Attacher::AttachEngine3D
  Height = 50.8
  Length = 41.3004
  Placement = pos=(-15.8242,-7.874,-1.6002) rot=(0,0,1;0rad)
  Width = 15.9004
FEATURE [Part::Cut] Cut001
  Base = -> Box003
  Tool = -> Box004
FEATURE [Part::Compound] Compound002  label="End Cap"
  Links = -> [Cut001,Cut]
FEATURE [Part::Box] Box005  label="Cube005"
  AttacherType = Attacher::AttachEngine3D
  Height = 50.8
  Length = 38.1
  Placement = pos=(1.6002,1.6002,1.6002) rot=(0,0,1;0rad)
  Width = 12.7
FEATURE [Part::Box] Box006  label="Cube006"
  AttacherType = Attacher::AttachEngine3D
  Height = 50.8
  Length = 41.3004
  Width = 15.9004
FEATURE [Part::Box] Box007  label="Cube007"
  AttacherType = Attacher::AttachEngine3D
  Height = 52.4002
  Length = 44.5008
  Placement = pos=(-17.4244,-9.4742,-3.2004) rot=(0,0,1;0rad)
  Width = 19.1008
FEATURE [Part::Box] Box008  label="Cube008"
  AttacherType = Attacher::AttachEngine3D
  Height = 50.8
  Length = 41.3004
  Placement = pos=(-15.8242,-7.874,-1.6002) rot=(0,0,1;0rad)
  Width = 15.9004
FEATURE [Part::Cut] Cut002
  Base = -> Box006
  Placement = pos=(-15.8242,-7.874,-1.6002) rot=(0,0,1;0rad)
  Tool = -> Box005
FEATURE [Part::Cut] Cut003
  Base = -> Box007
  Tool = -> Box008
FEATURE [Part::Compound] Compound003  label="End Cap001"
  Links = -> [Cut003,Cut002]
  Placement = pos=(0,2.54e-13,914.4) rot=(1,0,0;3.14159rad)
FEATURE [Part::Compound] Compound004  label="Capped Mast"
  Links = -> [Compound003,Pad004,Compound002]
FEATURE [Sketcher::SketchObject] Sketch035
  FullyConstrained = true
  MapMode = 5
  Placement = pos=(0,0,0) rot=(1,0,0;1.5708rad)
  Support = -> [XZ_Plane030]
  sketch-geometry (8):
    g0: LineSegment StartX=0 StartY=0 StartZ=0 EndX=12.7 EndY=0 EndZ=0
    g1: LineSegment StartX=12.7 StartY=0 StartZ=0 EndX=12.7 EndY=-12.7 EndZ=0
    g2: LineSegment StartX=12.7 StartY=-12.7 StartZ=0 EndX=0 EndY=-12.7 EndZ=0
    g3: LineSegment StartX=0 StartY=-12.7 StartZ=0 EndX=0 EndY=0 EndZ=0
    g4: LineSegment StartX=1.6002 StartY=-1.6002 StartZ=0 EndX=11.0998 EndY=-1.6002 EndZ=0
    g5: LineSegment StartX=11.0998 StartY=-1.6002 StartZ=0 EndX=11.0998 EndY=-11.0998 EndZ=0
    g6: LineSegment StartX=11.0998 StartY=-11.0998 StartZ=0 EndX=1.6002 EndY=-11.0998 EndZ=0
    g7: LineSegment StartX=1.6002 StartY=-11.0998 StartZ=0 EndX=1.6002 EndY=-1.6002 EndZ=0
  constraints (23):
    c: Coincident(g0,g1)
    c: Coincident(g1,g2)
    c: Coincident(g2,g3)
    c: Coincident(g3,g0)
    c: Horizontal(g0)
    c: Horizontal(g2)
    c: Vertical(g1)
    c: Vertical(g3)
    c: Coincident(g0,g-1)
    c: Coincident(g4,g5)
    c: Coincident(g5,g6)
    c: Coincident(g6,g7)
    c: Coincident(g7,g4)
    c: Horizontal(g4)
    c: Horizontal(g6)
    c: Vertical(g5)
    c: Vertical(g7)
    c: DistanceX(g2,g1) = 12.7
    c: DistanceY(g2,g0) = 12.7
    c: DistanceY(g2,g6) = 1.6002
    c: DistanceY(g4,g0) = 1.6002
    c: DistanceX(g0,g4) = 1.6002
    c: DistanceX(g4,g0) = 1.6002
FEATURE [PartDesign::Pad] Pad021
  Direction = (0,-1,2e-16)
  Length = 50.8
  Length2 = 10
  Placement = pos=(0,0,0) rot=(1,0,0;1.5708rad)
  Profile = -> Sketch035
  ReferenceAxis = -> Sketch035 [N_Axis]
  Type = 0
FEATURE [PartDesign::Body] Pad014Body
  Group = -> [Sketch028,Pad014]
  Origin = -> Origin028
  Tip = -> Pad014
FEATURE [PartDesign::Body] Pad021Body
  Group = -> [Sketch035,Pad021]
  Origin = -> Origin029
  Placement = pos=(-14.4556,6.16712,12.8016) rot=(0,0,1;1.5708rad)
  Tip = -> Pad021
FEATURE [PartDesign::Body] Body027
  Origin = -> Origin030
FEATURE [Part::Cylinder] Cylinder022
  Angle = 360
  AttacherType = Attacher::AttachEngine3D
  FirstAngle = 0
  Height = 25.4
  Placement = pos=(17.9538,3.2004,901.442) rot=(0,0,1;0rad)
  Radius = 2.3622
  SecondAngle = 0
FEATURE [Sketcher::SketchObject] Sketch036
  FullyConstrained = true
  MapMode = 5
  Support = -> [XY_Plane031]
  sketch-geometry (8):
    g0: LineSegment StartX=-9.525 StartY=-9.525 StartZ=0 EndX=9.525 EndY=-9.525 EndZ=0
    g1: LineSegment StartX=9.525 StartY=-9.525 StartZ=0 EndX=9.525 EndY=9.525 EndZ=0
    g2: LineSegment StartX=9.525 StartY=9.525 StartZ=0 EndX=-9.525 EndY=9.525 EndZ=0
    g3: LineSegment StartX=-9.525 StartY=9.525 StartZ=0 EndX=-9.525 EndY=-9.525 EndZ=0
    g4: LineSegment StartX=-6.35 StartY=-6.35 StartZ=0 EndX=6.35 EndY=-6.35 EndZ=0
    g5: LineSegment StartX=6.35 StartY=-6.35 StartZ=0 EndX=6.35 EndY=6.35 EndZ=0
    g6: LineSegment StartX=6.35 StartY=6.35 StartZ=0 EndX=-6.35 EndY=6.35 EndZ=0
    g7: LineSegment StartX=-6.35 StartY=6.35 StartZ=0 EndX=-6.35 EndY=-6.35 EndZ=0
  constraints (24):
    c: Coincident(g0,g1)
    c: Coincident(g1,g2)
    c: Coincident(g2,g3)
    c: Coincident(g3,g0)
    c: Horizontal(g0)
    c: Horizontal(g2)
    c: Vertical(g1)
    c: Vertical(g3)
    c: Coincident(g4,g5)
    c: Coincident(g5,g6)
    c: Coincident(g6,g7)
    c: Coincident(g7,g4)
    c: Horizontal(g4)
    c: Horizontal(g6)
    c: Vertical(g5)
    c: Vertical(g7)
    c: DistanceY(g0,g2) = 19.05
    c: DistanceX(g2,g1) = 19.05
    c: DistanceX(g2,g6) = 3.175
    c: DistanceX(g5,g1) = 3.175
    c: DistanceY(g6,g2) = 3.175
    c: DistanceY(g0,g4) = 3.175
    c: DistanceX(g2,g-1) = 9.525
    c: DistanceY(g-1,g1) = 9.525
FEATURE [PartDesign::Pad] Pad022
  Direction = (0,0,1)
  Length = 914.4
  Length2 = 10
  Profile = -> Sketch036
  ReferenceAxis = -> Sketch036 [N_Axis]
  Type = 0
FEATURE [PartDesign::Body] Body028
  Group = -> [Sketch036,Pad022]
  Origin = -> Origin031
  Placement = pos=(19.05,0,0) rot=(0,0,1;0rad)
  Tip = -> Pad022
FEATURE [PartDesign::FeatureBase] Clone001
  BaseFeature = -> Body028
FEATURE [PartDesign::Body] Body029
  Group = -> [Clone001]
  Origin = -> Origin032
  Tip = -> Clone001
FEATURE [PartDesign::FeatureBase] Clone002
  BaseFeature = -> Body028
FEATURE [PartDesign::Body] Body030
  Group = -> [Clone002]
  Origin = -> Origin033
  Placement = pos=(-19.05,0,0) rot=(0,0,1;0rad)
  Tip = -> Clone002
FEATURE [Part::Box] Box009  label="Cube009"
  AttacherType = Attacher::AttachEngine3D
  Height = 4.064
  Length = 12.7
  Placement = pos=(-6.354,-6.354,0) rot=(0,0,1;0rad)
  Width = 12.7
FEATURE [Part::Box] Box010  label="Cube010"
  AttacherType = Attacher::AttachEngine3D
  Height = 50.8
  Length = 57.15
  Placement = pos=(-28.575,-9.525,0) rot=(0,0,1;0rad)
  Width = 19.05
FEATURE [Part::Feature] Part__Feature001  label="21700Battery001"
  Placement = pos=(0,22.5,0) rot=(0,0,1;0rad)
  shape: bbox 22.95 x 22.95 x 70.61 mm, 44 faces (baked)
FEATURE [Part::Feature] Part__Feature002  label="21700Battery002"
  Placement = pos=(0,45,0) rot=(0,0,1;0rad)
  shape: bbox 22.95 x 22.95 x 70.61 mm, 44 faces (baked)
FEATURE [Part::Feature] Part__Feature003  label="21700Battery003"
  Placement = pos=(0,67.5,0) rot=(0,0,1;0rad)
  shape: bbox 22.95 x 22.95 x 70.61 mm, 44 faces (baked)
FEATURE [Part::Feature] Part__Feature004  label="21700Battery004"
  Placement = pos=(0,90,0) rot=(0,0,1;0rad)
  shape: bbox 22.95 x 22.95 x 70.61 mm, 44 faces (baked)
FEATURE [Part::Feature] Part__Feature005  label="21700Battery005"
  Placement = pos=(0,112.5,0) rot=(0,0,1;0rad)
  shape: bbox 22.95 x 22.95 x 70.61 mm, 44 faces (baked)
FEATURE [Part::Feature] Part__Feature006  label="21700Battery006"
  Placement = pos=(0,135,0) rot=(0,0,1;0rad)
  shape: bbox 22.95 x 22.95 x 70.61 mm, 44 faces (baked)
FEATURE [App::DocumentObjectGroup] Group008  label="BatteryRowBase"
  Group = -> [Part__Feature,Part__Feature001,Part__Feature002,Part__Feature003,Part__Feature004,Part__Feature005,Part__Feature006]
FEATURE [Part::Compound] Compound005  label="BatteryRow"
  Links = -> [Part__Feature,Part__Feature001,Part__Feature002,Part__Feature003,Part__Feature004,Part__Feature005,Part__Feature006]
  Placement = pos=(-8,-22.4,-127) rot=(0,0,1;0rad)
FEATURE [Sketcher::SketchObject] Sketch037
  FullyConstrained = true
  MapMode = 5
  Support = -> [XY_Plane034]
  sketch-geometry (16):
    g0: LineSegment StartX=-15.25 StartY=-15 StartZ=0 EndX=-15.25 EndY=7.5 EndZ=0
    g1: LineSegment StartX=15.25 StartY=7.5 StartZ=0 EndX=15.25 EndY=-15 EndZ=0
    g2: LineSegment StartX=15.25 StartY=7.5 StartZ=0 EndX=12.25 EndY=7.5 EndZ=0
    g3: LineSegment StartX=12.25 StartY=7.5 StartZ=0 EndX=12.25 EndY=0.25 EndZ=0
    g4: LineSegment StartX=12.25 StartY=0.25 StartZ=0 EndX=11.25 EndY=0.25 EndZ=0
    g5: LineSegment StartX=11.25 StartY=0.25 StartZ=0 EndX=11.25 EndY=7.5 EndZ=0
    g6: LineSegment StartX=11.25 StartY=7.5 StartZ=0 EndX=-11.25 EndY=7.5 EndZ=0
    g7: LineSegment StartX=-11.25 StartY=7.5 StartZ=0 EndX=-11.25 EndY=0.25 EndZ=0
    g8: LineSegment StartX=-11.25 StartY=0.25 StartZ=0 EndX=-12.25 EndY=0.25 EndZ=0
    g9: LineSegment StartX=-12.25 StartY=0.25 StartZ=0 EndX=-12.25 EndY=7.5 EndZ=0
    g10: LineSegment StartX=-12.25 StartY=7.5 StartZ=0 EndX=-15.25 EndY=7.5 EndZ=0
    g11: LineSegment StartX=15.25 StartY=-15 StartZ=0 EndX=7.625 EndY=-15 EndZ=0
    g12: LineSegment StartX=7.625 StartY=-15 StartZ=0 EndX=7.625 EndY=0.25 EndZ=0
    g13: LineSegment StartX=7.625 StartY=0.25 StartZ=0 EndX=-7.625 EndY=0.25 EndZ=0
    g14: LineSegment StartX=-7.625 StartY=0.25 StartZ=0 EndX=-7.625 EndY=-15 EndZ=0
    g15: LineSegment StartX=-7.625 StartY=-15 StartZ=0 EndX=-15.25 EndY=-15 EndZ=0
  constraints (41):
    c: Vertical(g0)
    c: DistanceX(g0,g1) = 30.5
    c: Coincident(g1,g2)
    c: Horizontal(g2)
    c: Coincident(g2,g3)
    c: Vertical(g3)
    c: Coincident(g3,g4)
    c: Coincident(g4,g5)
    c: Vertical(g5)
    c: Coincident(g5,g6)
    c: Coincident(g6,g7)
    c: Coincident(g7,g8)
    c: Coincident(g8,g9)
    c: Coincident(g9,g10)
    c: Coincident(g10,g0)
    c: Horizontal(g4)
    c: DistanceX(g4,g3) = 1
    c: DistanceY(g5,g2) = 0
    c: DistanceX(g2,g1) = 3
    c: Symmetric(g1,g0,g-2)
    c: Symmetric(g5,g6,g-2)
    c: Symmetric(g7,g4,g-2)
    c: Symmetric(g8,g3,g-2)
    c: Symmetric(g2,g9,g-2)
    c: Symmetric(g1,g0,g-2)
    c: DistanceY(g4,g5) = 7.25
    c: DistanceY(g1,g1) = 22.5
    c: Coincident(g1,g11)
    c: Horizontal(g11)
    c: Coincident(g11,g12)
    c: Vertical(g12)
    c: Coincident(g12,g13)
    c: Coincident(g13,g14)
    c: Vertical(g14)
    c: Coincident(g14,g15)
    c: Coincident(g15,g0)
    c: Horizontal(g15)
    c: Symmetric(g12,g13,g-2)
    c: DistanceX(g11,g1) = 7.625
    c: DistanceY(g1,g-1) = 15
    c: DistanceY(g4,g12) = 0
FEATURE [PartDesign::Pad] Pad023
  Direction = (0,0,1)
  Length = 0.15
  Length2 = 10
  Profile = -> Sketch037
  ReferenceAxis = -> Sketch037 [N_Axis]
  Type = 0
FEATURE [PartDesign::Body] Body031  label="Battery Connector007"
  Group = -> [Sketch037,Pad023]
  Origin = -> Origin034
  Tip = -> Pad023
FEATURE [Sketcher::SketchObject] Sketch038
  FullyConstrained = true
  MapMode = 5
  Support = -> [XY_Plane035]
  sketch-geometry (16):
    g0: LineSegment StartX=-15.25 StartY=-15 StartZ=0 EndX=-15.25 EndY=7.5 EndZ=0
    g1: LineSegment StartX=15.25 StartY=7.5 StartZ=0 EndX=15.25 EndY=-15 EndZ=0
    g2: LineSegment StartX=15.25 StartY=7.5 StartZ=0 EndX=12.25 EndY=7.5 EndZ=0
    g3: LineSegment StartX=12.25 StartY=7.5 StartZ=0 EndX=12.25 EndY=0.25 EndZ=0
    g4: LineSegment StartX=12.25 StartY=0.25 StartZ=0 EndX=11.25 EndY=0.25 EndZ=0
    g5: LineSegment StartX=11.25 StartY=0.25 StartZ=0 EndX=11.25 EndY=7.5 EndZ=0
    g6: LineSegment StartX=11.25 StartY=7.5 StartZ=0 EndX=-11.25 EndY=7.5 EndZ=0
    g7: LineSegment StartX=-11.25 StartY=7.5 StartZ=0 EndX=-11.25 EndY=0.25 EndZ=0
    g8: LineSegment StartX=-11.25 StartY=0.25 StartZ=0 EndX=-12.25 EndY=0.25 EndZ=0
    g9: LineSegment StartX=-12.25 StartY=0.25 StartZ=0 EndX=-12.25 EndY=7.5 EndZ=0
    g10: LineSegment StartX=-12.25 StartY=7.5 StartZ=0 EndX=-15.25 EndY=7.5 EndZ=0
    g11: LineSegment StartX=15.25 StartY=-15 StartZ=0 EndX=7.625 EndY=-15 EndZ=0
    g12: LineSegment StartX=7.625 StartY=-15 StartZ=0 EndX=7.625 EndY=0.25 EndZ=0
    g13: LineSegment StartX=7.625 StartY=0.25 StartZ=0 EndX=-7.625 EndY=0.25 EndZ=0
    g14: LineSegment StartX=-7.625 StartY=0.25 StartZ=0 EndX=-7.625 EndY=-15 EndZ=0
    g15: LineSegment StartX=-7.625 StartY=-15 StartZ=0 EndX=-15.25 EndY=-15 EndZ=0
  constraints (41):
    c: Vertical(g0)
    c: DistanceX(g0,g1) = 30.5
    c: Coincident(g1,g2)
    c: Horizontal(g2)
    c: Coincident(g2,g3)
    c: Vertical(g3)
    c: Coincident(g3,g4)
    c: Coincident(g4,g5)
    c: Vertical(g5)
    c: Coincident(g5,g6)
    c: Coincident(g6,g7)
    c: Coincident(g7,g8)
    c: Coincident(g8,g9)
    c: Coincident(g9,g10)
    c: Coincident(g10,g0)
    c: Horizontal(g4)
    c: DistanceX(g4,g3) = 1
    c: DistanceY(g5,g2) = 0
    c: DistanceX(g2,g1) = 3
    c: Symmetric(g1,g0,g-2)
    c: Symmetric(g5,g6,g-2)
    c: Symmetric(g7,g4,g-2)
    c: Symmetric(g8,g3,g-2)
    c: Symmetric(g2,g9,g-2)
    c: Symmetric(g1,g0,g-2)
    c: DistanceY(g4,g5) = 7.25
    c: DistanceY(g1,g1) = 22.5
    c: Coincident(g1,g11)
    c: Horizontal(g11)
    c: Coincident(g11,g12)
    c: Vertical(g12)
    c: Coincident(g12,g13)
    c: Coincident(g13,g14)
    c: Vertical(g14)
    c: Coincident(g14,g15)
    c: Coincident(g15,g0)
    c: Horizontal(g15)
    c: Symmetric(g12,g13,g-2)
    c: DistanceX(g11,g1) = 7.625
    c: DistanceY(g1,g-1) = 15
    c: DistanceY(g4,g12) = 0
FEATURE [PartDesign::Pad] Pad024
  Direction = (0,0,1)
  Length = 0.15
  Length2 = 10
  Profile = -> Sketch038
  ReferenceAxis = -> Sketch038 [N_Axis]
  Type = 0
FEATURE [PartDesign::Body] Body032  label="Battery Connector008"
  Group = -> [Sketch038,Pad024]
  Origin = -> Origin035
  Placement = pos=(0,22.5,0) rot=(0,0,1;0rad)
  Tip = -> Pad024
FEATURE [Sketcher::SketchObject] Sketch039
  FullyConstrained = true
  MapMode = 5
  Support = -> [XY_Plane036]
  sketch-geometry (16):
    g0: LineSegment StartX=-15.25 StartY=-15 StartZ=0 EndX=-15.25 EndY=7.5 EndZ=0
    g1: LineSegment StartX=15.25 StartY=7.5 StartZ=0 EndX=15.25 EndY=-15 EndZ=0
    g2: LineSegment StartX=15.25 StartY=7.5 StartZ=0 EndX=12.25 EndY=7.5 EndZ=0
    g3: LineSegment StartX=12.25 StartY=7.5 StartZ=0 EndX=12.25 EndY=0.25 EndZ=0
    g4: LineSegment StartX=12.25 StartY=0.25 StartZ=0 EndX=11.25 EndY=0.25 EndZ=0
    g5: LineSegment StartX=11.25 StartY=0.25 StartZ=0 EndX=11.25 EndY=7.5 EndZ=0
    g6: LineSegment StartX=11.25 StartY=7.5 StartZ=0 EndX=-11.25 EndY=7.5 EndZ=0
    g7: LineSegment StartX=-11.25 StartY=7.5 StartZ=0 EndX=-11.25 EndY=0.25 EndZ=0
    g8: LineSegment StartX=-11.25 StartY=0.25 StartZ=0 EndX=-12.25 EndY=0.25 EndZ=0
    g9: LineSegment StartX=-12.25 StartY=0.25 StartZ=0 EndX=-12.25 EndY=7.5 EndZ=0
    g10: LineSegment StartX=-12.25 StartY=7.5 StartZ=0 EndX=-15.25 EndY=7.5 EndZ=0
    g11: LineSegment StartX=15.25 StartY=-15 StartZ=0 EndX=7.625 EndY=-15 EndZ=0
    g12: LineSegment StartX=7.625 StartY=-15 StartZ=0 EndX=7.625 EndY=0.25 EndZ=0
    g13: LineSegment StartX=7.625 StartY=0.25 StartZ=0 EndX=-7.625 EndY=0.25 EndZ=0
    g14: LineSegment StartX=-7.625 StartY=0.25 StartZ=0 EndX=-7.625 EndY=-15 EndZ=0
    g15: LineSegment StartX=-7.625 StartY=-15 StartZ=0 EndX=-15.25 EndY=-15 EndZ=0
  constraints (41):
    c: Vertical(g0)
    c: DistanceX(g0,g1) = 30.5
    c: Coincident(g1,g2)
    c: Horizontal(g2)
    c: Coincident(g2,g3)
    c: Vertical(g3)
    c: Coincident(g3,g4)
    c: Coincident(g4,g5)
    c: Vertical(g5)
    c: Coincident(g5,g6)
    c: Coincident(g6,g7)
    c: Coincident(g7,g8)
    c: Coincident(g8,g9)
    c: Coincident(g9,g10)
    c: Coincident(g10,g0)
    c: Horizontal(g4)
    c: DistanceX(g4,g3) = 1
    c: DistanceY(g5,g2) = 0
    c: DistanceX(g2,g1) = 3
    c: Symmetric(g1,g0,g-2)
    c: Symmetric(g5,g6,g-2)
    c: Symmetric(g7,g4,g-2)
    c: Symmetric(g8,g3,g-2)
    c: Symmetric(g2,g9,g-2)
    c: Symmetric(g1,g0,g-2)
    c: DistanceY(g4,g5) = 7.25
    c: DistanceY(g1,g1) = 22.5
    c: Coincident(g1,g11)
    c: Horizontal(g11)
    c: Coincident(g11,g12)
    c: Vertical(g12)
    c: Coincident(g12,g13)
    c: Coincident(g13,g14)
    c: Vertical(g14)
    c: Coincident(g14,g15)
    c: Coincident(g15,g0)
    c: Horizontal(g15)
    c: Symmetric(g12,g13,g-2)
    c: DistanceX(g11,g1) = 7.625
    c: DistanceY(g1,g-1) = 15
    c: DistanceY(g4,g12) = 0
FEATURE [PartDesign::Pad] Pad025
  Direction = (0,0,1)
  Length = 0.15
  Length2 = 10
  Profile = -> Sketch039
  ReferenceAxis = -> Sketch039 [N_Axis]
  Type = 0
FEATURE [PartDesign::Body] Body033  label="Battery Connector009"
  Group = -> [Sketch039,Pad025]
  Origin = -> Origin036
  Placement = pos=(0,45,0) rot=(0,0,1;0rad)
  Tip = -> Pad025
FEATURE [Sketcher::SketchObject] Sketch040
  FullyConstrained = true
  MapMode = 5
  Support = -> [XY_Plane037]
  sketch-geometry (16):
    g0: LineSegment StartX=-15.25 StartY=-15 StartZ=0 EndX=-15.25 EndY=7.5 EndZ=0
    g1: LineSegment StartX=15.25 StartY=7.5 StartZ=0 EndX=15.25 EndY=-15 EndZ=0
    g2: LineSegment StartX=15.25 StartY=7.5 StartZ=0 EndX=12.25 EndY=7.5 EndZ=0
    g3: LineSegment StartX=12.25 StartY=7.5 StartZ=0 EndX=12.25 EndY=0.25 EndZ=0
    g4: LineSegment StartX=12.25 StartY=0.25 StartZ=0 EndX=11.25 EndY=0.25 EndZ=0
    g5: LineSegment StartX=11.25 StartY=0.25 StartZ=0 EndX=11.25 EndY=7.5 EndZ=0
    g6: LineSegment StartX=11.25 StartY=7.5 StartZ=0 EndX=-11.25 EndY=7.5 EndZ=0
    g7: LineSegment StartX=-11.25 StartY=7.5 StartZ=0 EndX=-11.25 EndY=0.25 EndZ=0
    g8: LineSegment StartX=-11.25 StartY=0.25 StartZ=0 EndX=-12.25 EndY=0.25 EndZ=0
    g9: LineSegment StartX=-12.25 StartY=0.25 StartZ=0 EndX=-12.25 EndY=7.5 EndZ=0
    g10: LineSegment StartX=-12.25 StartY=7.5 StartZ=0 EndX=-15.25 EndY=7.5 EndZ=0
    g11: LineSegment StartX=15.25 StartY=-15 StartZ=0 EndX=7.625 EndY=-15 EndZ=0
    g12: LineSegment StartX=7.625 StartY=-15 StartZ=0 EndX=7.625 EndY=0.25 EndZ=0
    g13: LineSegment StartX=7.625 StartY=0.25 StartZ=0 EndX=-7.625 EndY=0.25 EndZ=0
    g14: LineSegment StartX=-7.625 StartY=0.25 StartZ=0 EndX=-7.625 EndY=-15 EndZ=0
    g15: LineSegment StartX=-7.625 StartY=-15 StartZ=0 EndX=-15.25 EndY=-15 EndZ=0
  constraints (41):
    c: Vertical(g0)
    c: DistanceX(g0,g1) = 30.5
    c: Coincident(g1,g2)
    c: Horizontal(g2)
    c: Coincident(g2,g3)
    c: Vertical(g3)
    c: Coincident(g3,g4)
    c: Coincident(g4,g5)
    c: Vertical(g5)
    c: Coincident(g5,g6)
    c: Coincident(g6,g7)
    c: Coincident(g7,g8)
    c: Coincident(g8,g9)
    c: Coincident(g9,g10)
    c: Coincident(g10,g0)
    c: Horizontal(g4)
    c: DistanceX(g4,g3) = 1
    c: DistanceY(g5,g2) = 0
    c: DistanceX(g2,g1) = 3
    c: Symmetric(g1,g0,g-2)
    c: Symmetric(g5,g6,g-2)
    c: Symmetric(g7,g4,g-2)
    c: Symmetric(g8,g3,g-2)
    c: Symmetric(g2,g9,g-2)
    c: Symmetric(g1,g0,g-2)
    c: DistanceY(g4,g5) = 7.25
    c: DistanceY(g1,g1) = 22.5
    c: Coincident(g1,g11)
    c: Horizontal(g11)
    c: Coincident(g11,g12)
    c: Vertical(g12)
    c: Coincident(g12,g13)
    c: Coincident(g13,g14)
    c: Vertical(g14)
    c: Coincident(g14,g15)
    c: Coincident(g15,g0)
    c: Horizontal(g15)
    c: Symmetric(g12,g13,g-2)
    c: DistanceX(g11,g1) = 7.625
    c: DistanceY(g1,g-1) = 15
    c: DistanceY(g4,g12) = 0
FEATURE [PartDesign::Pad] Pad026
  Direction = (0,0,1)
  Length = 0.15
  Length2 = 10
  Profile = -> Sketch040
  ReferenceAxis = -> Sketch040 [N_Axis]
  Type = 0
FEATURE [PartDesign::Body] Body034  label="Battery Connector010"
  Group = -> [Sketch040,Pad026]
  Origin = -> Origin037
  Placement = pos=(0,67.5,0) rot=(0,0,1;0rad)
  Tip = -> Pad026
FEATURE [Sketcher::SketchObject] Sketch041
  FullyConstrained = true
  MapMode = 5
  Support = -> [XY_Plane038]
  sketch-geometry (16):
    g0: LineSegment StartX=-15.25 StartY=-15 StartZ=0 EndX=-15.25 EndY=7.5 EndZ=0
    g1: LineSegment StartX=15.25 StartY=7.5 StartZ=0 EndX=15.25 EndY=-15 EndZ=0
    g2: LineSegment StartX=15.25 StartY=7.5 StartZ=0 EndX=12.25 EndY=7.5 EndZ=0
    g3: LineSegment StartX=12.25 StartY=7.5 StartZ=0 EndX=12.25 EndY=0.25 EndZ=0
    g4: LineSegment StartX=12.25 StartY=0.25 StartZ=0 EndX=11.25 EndY=0.25 EndZ=0
    g5: LineSegment StartX=11.25 StartY=0.25 StartZ=0 EndX=11.25 EndY=7.5 EndZ=0
    g6: LineSegment StartX=11.25 StartY=7.5 StartZ=0 EndX=-11.25 EndY=7.5 EndZ=0
    g7: LineSegment StartX=-11.25 StartY=7.5 StartZ=0 EndX=-11.25 EndY=0.25 EndZ=0
    g8: LineSegment StartX=-11.25 StartY=0.25 StartZ=0 EndX=-12.25 EndY=0.25 EndZ=0
    g9: LineSegment StartX=-12.25 StartY=0.25 StartZ=0 EndX=-12.25 EndY=7.5 EndZ=0
    g10: LineSegment StartX=-12.25 StartY=7.5 StartZ=0 EndX=-15.25 EndY=7.5 EndZ=0
    g11: LineSegment StartX=15.25 StartY=-15 StartZ=0 EndX=7.625 EndY=-15 EndZ=0
    g12: LineSegment StartX=7.625 StartY=-15 StartZ=0 EndX=7.625 EndY=0.25 EndZ=0
    g13: LineSegment StartX=7.625 StartY=0.25 StartZ=0 EndX=-7.625 EndY=0.25 EndZ=0
    g14: LineSegment StartX=-7.625 StartY=0.25 StartZ=0 EndX=-7.625 EndY=-15 EndZ=0
    g15: LineSegment StartX=-7.625 StartY=-15 StartZ=0 EndX=-15.25 EndY=-15 EndZ=0
  constraints (41):
    c: Vertical(g0)
    c: DistanceX(g0,g1) = 30.5
    c: Coincident(g1,g2)
    c: Horizontal(g2)
    c: Coincident(g2,g3)
    c: Vertical(g3)
    c: Coincident(g3,g4)
    c: Coincident(g4,g5)
    c: Vertical(g5)
    c: Coincident(g5,g6)
    c: Coincident(g6,g7)
    c: Coincident(g7,g8)
    c: Coincident(g8,g9)
    c: Coincident(g9,g10)
    c: Coincident(g10,g0)
    c: Horizontal(g4)
    c: DistanceX(g4,g3) = 1
    c: DistanceY(g5,g2) = 0
    c: DistanceX(g2,g1) = 3
    c: Symmetric(g1,g0,g-2)
    c: Symmetric(g5,g6,g-2)
    c: Symmetric(g7,g4,g-2)
    c: Symmetric(g8,g3,g-2)
    c: Symmetric(g2,g9,g-2)
    c: Symmetric(g1,g0,g-2)
    c: DistanceY(g4,g5) = 7.25
    c: DistanceY(g1,g1) = 22.5
    c: Coincident(g1,g11)
    c: Horizontal(g11)
    c: Coincident(g11,g12)
    c: Vertical(g12)
    c: Coincident(g12,g13)
    c: Coincident(g13,g14)
    c: Vertical(g14)
    c: Coincident(g14,g15)
    c: Coincident(g15,g0)
    c: Horizontal(g15)
    c: Symmetric(g12,g13,g-2)
    c: DistanceX(g11,g1) = 7.625
    c: DistanceY(g1,g-1) = 15
    c: DistanceY(g4,g12) = 0
FEATURE [PartDesign::Pad] Pad027
  Direction = (0,0,1)
  Length = 0.15
  Length2 = 10
  Profile = -> Sketch041
  ReferenceAxis = -> Sketch041 [N_Axis]
  Type = 0
FEATURE [PartDesign::Body] Body035  label="Battery Connector011"
  Group = -> [Sketch041,Pad027]
  Origin = -> Origin038
  Placement = pos=(0,90,0) rot=(0,0,1;0rad)
  Tip = -> Pad027
FEATURE [Sketcher::SketchObject] Sketch042
  FullyConstrained = true
  MapMode = 5
  Support = -> [XY_Plane039]
  sketch-geometry (16):
    g0: LineSegment StartX=-15.25 StartY=-15 StartZ=0 EndX=-15.25 EndY=7.5 EndZ=0
    g1: LineSegment StartX=15.25 StartY=7.5 StartZ=0 EndX=15.25 EndY=-15 EndZ=0
    g2: LineSegment StartX=15.25 StartY=7.5 StartZ=0 EndX=12.25 EndY=7.5 EndZ=0
    g3: LineSegment StartX=12.25 StartY=7.5 StartZ=0 EndX=12.25 EndY=0.25 EndZ=0
    g4: LineSegment StartX=12.25 StartY=0.25 StartZ=0 EndX=11.25 EndY=0.25 EndZ=0
    g5: LineSegment StartX=11.25 StartY=0.25 StartZ=0 EndX=11.25 EndY=7.5 EndZ=0
    g6: LineSegment StartX=11.25 StartY=7.5 StartZ=0 EndX=-11.25 EndY=7.5 EndZ=0
    g7: LineSegment StartX=-11.25 StartY=7.5 StartZ=0 EndX=-11.25 EndY=0.25 EndZ=0
    g8: LineSegment StartX=-11.25 StartY=0.25 StartZ=0 EndX=-12.25 EndY=0.25 EndZ=0
    g9: LineSegment StartX=-12.25 StartY=0.25 StartZ=0 EndX=-12.25 EndY=7.5 EndZ=0
    g10: LineSegment StartX=-12.25 StartY=7.5 StartZ=0 EndX=-15.25 EndY=7.5 EndZ=0
    g11: LineSegment StartX=15.25 StartY=-15 StartZ=0 EndX=7.625 EndY=-15 EndZ=0
    g12: LineSegment StartX=7.625 StartY=-15 StartZ=0 EndX=7.625 EndY=0.25 EndZ=0
    g13: LineSegment StartX=7.625 StartY=0.25 StartZ=0 EndX=-7.625 EndY=0.25 EndZ=0
    g14: LineSegment StartX=-7.625 StartY=0.25 StartZ=0 EndX=-7.625 EndY=-15 EndZ=0
    g15: LineSegment StartX=-7.625 StartY=-15 StartZ=0 EndX=-15.25 EndY=-15 EndZ=0
  constraints (41):
    c: Vertical(g0)
    c: DistanceX(g0,g1) = 30.5
    c: Coincident(g1,g2)
    c: Horizontal(g2)
    c: Coincident(g2,g3)
    c: Vertical(g3)
    c: Coincident(g3,g4)
    c: Coincident(g4,g5)
    c: Vertical(g5)
    c: Coincident(g5,g6)
    c: Coincident(g6,g7)
    c: Coincident(g7,g8)
    c: Coincident(g8,g9)
    c: Coincident(g9,g10)
    c: Coincident(g10,g0)
    c: Horizontal(g4)
    c: DistanceX(g4,g3) = 1
    c: DistanceY(g5,g2) = 0
    c: DistanceX(g2,g1) = 3
    c: Symmetric(g1,g0,g-2)
    c: Symmetric(g5,g6,g-2)
    c: Symmetric(g7,g4,g-2)
    c: Symmetric(g8,g3,g-2)
    c: Symmetric(g2,g9,g-2)
    c: Symmetric(g1,g0,g-2)
    c: DistanceY(g4,g5) = 7.25
    c: DistanceY(g1,g1) = 22.5
    c: Coincident(g1,g11)
    c: Horizontal(g11)
    c: Coincident(g11,g12)
    c: Vertical(g12)
    c: Coincident(g12,g13)
    c: Coincident(g13,g14)
    c: Vertical(g14)
    c: Coincident(g14,g15)
    c: Coincident(g15,g0)
    c: Horizontal(g15)
    c: Symmetric(g12,g13,g-2)
    c: DistanceX(g11,g1) = 7.625
    c: DistanceY(g1,g-1) = 15
    c: DistanceY(g4,g12) = 0
FEATURE [PartDesign::Pad] Pad028
  Direction = (0,0,1)
  Length = 0.15
  Length2 = 10
  Profile = -> Sketch042
  ReferenceAxis = -> Sketch042 [N_Axis]
  Type = 0
FEATURE [PartDesign::Body] Body036  label="Battery Connector012"
  Group = -> [Sketch042,Pad028]
  Origin = -> Origin039
  Placement = pos=(0,112.5,0) rot=(0,0,1;0rad)
  Tip = -> Pad028
FEATURE [Sketcher::SketchObject] Sketch043
  FullyConstrained = true
  MapMode = 5
  Support = -> [XY_Plane040]
  sketch-geometry (16):
    g0: LineSegment StartX=-15.25 StartY=-15 StartZ=0 EndX=-15.25 EndY=7.5 EndZ=0
    g1: LineSegment StartX=15.25 StartY=7.5 StartZ=0 EndX=15.25 EndY=-15 EndZ=0
    g2: LineSegment StartX=15.25 StartY=7.5 StartZ=0 EndX=12.25 EndY=7.5 EndZ=0
    g3: LineSegment StartX=12.25 StartY=7.5 StartZ=0 EndX=12.25 EndY=0.25 EndZ=0
    g4: LineSegment StartX=12.25 StartY=0.25 StartZ=0 EndX=11.25 EndY=0.25 EndZ=0
    g5: LineSegment StartX=11.25 StartY=0.25 StartZ=0 EndX=11.25 EndY=7.5 EndZ=0
    g6: LineSegment StartX=11.25 StartY=7.5 StartZ=0 EndX=-11.25 EndY=7.5 EndZ=0
    g7: LineSegment StartX=-11.25 StartY=7.5 StartZ=0 EndX=-11.25 EndY=0.25 EndZ=0
    g8: LineSegment StartX=-11.25 StartY=0.25 StartZ=0 EndX=-12.25 EndY=0.25 EndZ=0
    g9: LineSegment StartX=-12.25 StartY=0.25 StartZ=0 EndX=-12.25 EndY=7.5 EndZ=0
    g10: LineSegment StartX=-12.25 StartY=7.5 StartZ=0 EndX=-15.25 EndY=7.5 EndZ=0
    g11: LineSegment StartX=15.25 StartY=-15 StartZ=0 EndX=7.625 EndY=-15 EndZ=0
    g12: LineSegment StartX=7.625 StartY=-15 StartZ=0 EndX=7.625 EndY=0.25 EndZ=0
    g13: LineSegment StartX=7.625 StartY=0.25 StartZ=0 EndX=-7.625 EndY=0.25 EndZ=0
    g14: LineSegment StartX=-7.625 StartY=0.25 StartZ=0 EndX=-7.625 EndY=-15 EndZ=0
    g15: LineSegment StartX=-7.625 StartY=-15 StartZ=0 EndX=-15.25 EndY=-15 EndZ=0
  constraints (41):
    c: Vertical(g0)
    c: DistanceX(g0,g1) = 30.5
    c: Coincident(g1,g2)
    c: Horizontal(g2)
    c: Coincident(g2,g3)
    c: Vertical(g3)
    c: Coincident(g3,g4)
    c: Coincident(g4,g5)
    c: Vertical(g5)
    c: Coincident(g5,g6)
    c: Coincident(g6,g7)
    c: Coincident(g7,g8)
    c: Coincident(g8,g9)
    c: Coincident(g9,g10)
    c: Coincident(g10,g0)
    c: Horizontal(g4)
    c: DistanceX(g4,g3) = 1
    c: DistanceY(g5,g2) = 0
    c: DistanceX(g2,g1) = 3
    c: Symmetric(g1,g0,g-2)
    c: Symmetric(g5,g6,g-2)
    c: Symmetric(g7,g4,g-2)
    c: Symmetric(g8,g3,g-2)
    c: Symmetric(g2,g9,g-2)
    c: Symmetric(g1,g0,g-2)
    c: DistanceY(g4,g5) = 7.25
    c: DistanceY(g1,g1) = 22.5
    c: Coincident(g1,g11)
    c: Horizontal(g11)
    c: Coincident(g11,g12)
    c: Vertical(g12)
    c: Coincident(g12,g13)
    c: Coincident(g13,g14)
    c: Vertical(g14)
    c: Coincident(g14,g15)
    c: Coincident(g15,g0)
    c: Horizontal(g15)
    c: Symmetric(g12,g13,g-2)
    c: DistanceX(g11,g1) = 7.625
    c: DistanceY(g1,g-1) = 15
    c: DistanceY(g4,g12) = 0
FEATURE [PartDesign::Pad] Pad029
  Direction = (0,0,1)
  Length = 0.15
  Length2 = 10
  Profile = -> Sketch043
  ReferenceAxis = -> Sketch043 [N_Axis]
  Type = 0
FEATURE [PartDesign::Body] Body037  label="Battery Connector013"
  Group = -> [Sketch043,Pad029]
  Origin = -> Origin040
  Placement = pos=(0,135,0) rot=(0,0,1;0rad)
  Tip = -> Pad029
FEATURE [Sketcher::SketchObject] Sketch044
  FullyConstrained = true
  MapMode = 5
  Support = -> [XY_Plane041]
  sketch-geometry (16):
    g0: LineSegment StartX=-15.25 StartY=-15 StartZ=0 EndX=-15.25 EndY=7.5 EndZ=0
    g1: LineSegment StartX=15.25 StartY=7.5 StartZ=0 EndX=15.25 EndY=-15 EndZ=0
    g2: LineSegment StartX=15.25 StartY=7.5 StartZ=0 EndX=12.25 EndY=7.5 EndZ=0
    g3: LineSegment StartX=12.25 StartY=7.5 StartZ=0 EndX=12.25 EndY=0.25 EndZ=0
    g4: LineSegment StartX=12.25 StartY=0.25 StartZ=0 EndX=11.25 EndY=0.25 EndZ=0
    g5: LineSegment StartX=11.25 StartY=0.25 StartZ=0 EndX=11.25 EndY=7.5 EndZ=0
    g6: LineSegment StartX=11.25 StartY=7.5 StartZ=0 EndX=-11.25 EndY=7.5 EndZ=0
    g7: LineSegment StartX=-11.25 StartY=7.5 StartZ=0 EndX=-11.25 EndY=0.25 EndZ=0
    g8: LineSegment StartX=-11.25 StartY=0.25 StartZ=0 EndX=-12.25 EndY=0.25 EndZ=0
    g9: LineSegment StartX=-12.25 StartY=0.25 StartZ=0 EndX=-12.25 EndY=7.5 EndZ=0
    g10: LineSegment StartX=-12.25 StartY=7.5 StartZ=0 EndX=-15.25 EndY=7.5 EndZ=0
    g11: LineSegment StartX=15.25 StartY=-15 StartZ=0 EndX=7.625 EndY=-15 EndZ=0
    g12: LineSegment StartX=7.625 StartY=-15 StartZ=0 EndX=7.625 EndY=0.25 EndZ=0
    g13: LineSegment StartX=7.625 StartY=0.25 StartZ=0 EndX=-7.625 EndY=0.25 EndZ=0
    g14: LineSegment StartX=-7.625 StartY=0.25 StartZ=0 EndX=-7.625 EndY=-15 EndZ=0
    g15: LineSegment StartX=-7.625 StartY=-15 StartZ=0 EndX=-15.25 EndY=-15 EndZ=0
  constraints (41):
    c: Vertical(g0)
    c: DistanceX(g0,g1) = 30.5
    c: Coincident(g1,g2)
    c: Horizontal(g2)
    c: Coincident(g2,g3)
    c: Vertical(g3)
    c: Coincident(g3,g4)
    c: Coincident(g4,g5)
    c: Vertical(g5)
    c: Coincident(g5,g6)
    c: Coincident(g6,g7)
    c: Coincident(g7,g8)
    c: Coincident(g8,g9)
    c: Coincident(g9,g10)
    c: Coincident(g10,g0)
    c: Horizontal(g4)
    c: DistanceX(g4,g3) = 1
    c: DistanceY(g5,g2) = 0
    c: DistanceX(g2,g1) = 3
    c: Symmetric(g1,g0,g-2)
    c: Symmetric(g5,g6,g-2)
    c: Symmetric(g7,g4,g-2)
    c: Symmetric(g8,g3,g-2)
    c: Symmetric(g2,g9,g-2)
    c: Symmetric(g1,g0,g-2)
    c: DistanceY(g4,g5) = 7.25
    c: DistanceY(g1,g1) = 22.5
    c: Coincident(g1,g11)
    c: Horizontal(g11)
    c: Coincident(g11,g12)
    c: Vertical(g12)
    c: Coincident(g12,g13)
    c: Coincident(g13,g14)
    c: Vertical(g14)
    c: Coincident(g14,g15)
    c: Coincident(g15,g0)
    c: Horizontal(g15)
    c: Symmetric(g12,g13,g-2)
    c: DistanceX(g11,g1) = 7.625
    c: DistanceY(g1,g-1) = 15
    c: DistanceY(g4,g12) = 0
FEATURE [PartDesign::Pad] Pad030
  Direction = (0,0,1)
  Length = 0.15
  Length2 = 10
  Profile = -> Sketch044
  ReferenceAxis = -> Sketch044 [N_Axis]
  Type = 0
FEATURE [PartDesign::Body] Body038  label="Battery Connector014"
  Group = -> [Sketch044,Pad030]
  Origin = -> Origin041
  Placement = pos=(0,157.5,0) rot=(0,0,1;0rad)
  Tip = -> Pad030
FEATURE [Part::Box] Box011  label="Cube011"
  AttacherType = Attacher::AttachEngine3D
  Height = 10
  Length = 32
  Placement = pos=(-16,157.75,-5) rot=(0,0,1;0rad)
  Width = 10
FEATURE [Part::Cut] Cut004
  Base = -> Body038
  Tool = -> Box011
FEATURE [Part::MultiFuse] Fusion
  Shapes = -> [Body031,Body032,Body033,Body034,Body035,Body036,Body037,Cut004]
FEATURE [Part::FeaturePython] refine  label="BatteryConnector"  # WARN: FeaturePython — macro-defined, semantics opaque (R4)
  Base = -> Fusion
  Placement = pos=(0,-1.273,-56.4) rot=(0,0,1;0rad)
FEATURE [App::DocumentObjectGroup] Group005  label="BatteryConnectorGroup"
  Group = -> [Fusion,refine]
FEATURE [App::DocumentObjectGroup] Group007  label="Battery001"
  Group = -> [Group008,Compound005,Group005]
FEATURE [Part::Cylinder] Cylinder023
  Angle = 360
  AttacherType = Attacher::AttachEngine3D
  FirstAngle = 0
  Height = 35
  Radius = 4
  SecondAngle = 0
FEATURE [Part::Cylinder] Cylinder024
  Angle = 360
  AttacherType = Attacher::AttachEngine3D
  FirstAngle = 0
  Height = 2.5
  Radius = 8
  SecondAngle = 0
FEATURE [Part::RegularPolygon] RegularPolygon  label="Regular polygon"
  AttacherType = Attacher::AttachEngine3D
  Circumradius = 3
  Polygon = 6
FEATURE [Part::Extrusion] Extrude
  Base = -> RegularPolygon
  Dir = (0,0,1)
  DirMode = 2
  FaceMakerClass = Part::FaceMakerBullseye
  LengthFwd = 3
  LengthRev = 0
  Solid = true
  Symmetric = false
  TaperAngle = -3
FEATURE [Part::MultiFuse] Fusion001
  Shapes = -> [Cylinder023,Cylinder024]
FEATURE [Part::Cut] Cut005  label="M8 35mm"
  Base = -> Fusion001
  Tool = -> Extrude
FEATURE [Part::Cylinder] Cylinder025
  Angle = 360
  AttacherType = Attacher::AttachEngine3D
  FirstAngle = 0
  Height = 25
  Radius = 3
  SecondAngle = 0
FEATURE [Part::Cylinder] Cylinder026
  Angle = 360
  AttacherType = Attacher::AttachEngine3D
  FirstAngle = 0
  Height = 1.3
  Radius = 6
  SecondAngle = 0
FEATURE [Part::MultiFuse] Fusion002
  Shapes = -> [Cylinder025,Cylinder026]
FEATURE [Part::RegularPolygon] RegularPolygon001  label="Regular polygon001"
  AttacherType = Attacher::AttachEngine3D
  Circumradius = 2.5
  Polygon = 6
FEATURE [Part::Extrusion] Extrude001
  Base = -> RegularPolygon001
  Dir = (0,0,1)
  DirMode = 2
  FaceMakerClass = Part::FaceMakerBullseye
  LengthFwd = 2.5
  LengthRev = 0
  Solid = true
  Symmetric = false
  TaperAngle = -3
FEATURE [Part::Cut] Cut006  label="M6 25mm"
  Base = -> Fusion002
  Placement = pos=(0,19.05,0) rot=(0,0,1;0rad)
  Tool = -> Extrude001
FEATURE [App::DocumentObjectGroup] Group009  label="Screws"
  Group = -> [Cut005,Cut006]
FEATURE [Part::Cylinder] Cylinder027
  Angle = 360
  AttacherType = Attacher::AttachEngine3D
  FirstAngle = 0
  Height = 35
  Radius = 4
  SecondAngle = 0
FEATURE [Part::Cylinder] Cylinder028
  Angle = 360
  AttacherType = Attacher::AttachEngine3D
  FirstAngle = 0
  Height = 2.5
  Radius = 8
  SecondAngle = 0
FEATURE [Part::MultiFuse] Fusion003
  Shapes = -> [Cylinder027,Cylinder028]
FEATURE [Part::RegularPolygon] RegularPolygon002  label="Regular polygon002"
  AttacherType = Attacher::AttachEngine3D
  Circumradius = 3
  Polygon = 6
FEATURE [Part::Extrusion] Extrude002
  Base = -> RegularPolygon002
  Dir = (0,0,1)
  DirMode = 2
  FaceMakerClass = Part::FaceMakerBullseye
  LengthFwd = 3
  LengthRev = 0
  Solid = true
  Symmetric = false
  TaperAngle = -3
FEATURE [Part::Cut] Cut007  label="M8 35mm001"
  Base = -> Fusion003
  Placement = pos=(19.05,0,-19.05) rot=(0,0,1;0rad)
  Tool = -> Extrude002
FEATURE [Part::Cylinder] Cylinder029
  Angle = 360
  AttacherType = Attacher::AttachEngine3D
  FirstAngle = 0
  Height = 35
  Radius = 4
  SecondAngle = 0
FEATURE [Part::Cylinder] Cylinder030
  Angle = 360
  AttacherType = Attacher::AttachEngine3D
  FirstAngle = 0
  Height = 2.5
  Radius = 8
  SecondAngle = 0
FEATURE [Part::MultiFuse] Fusion004
  Shapes = -> [Cylinder029,Cylinder030]
FEATURE [Part::RegularPolygon] RegularPolygon003  label="Regular polygon003"
  AttacherType = Attacher::AttachEngine3D
  Circumradius = 3
  Polygon = 6
FEATURE [Part::Extrusion] Extrude003
  Base = -> RegularPolygon003
  Dir = (0,0,1)
  DirMode = 2
  FaceMakerClass = Part::FaceMakerBullseye
  LengthFwd = 3
  LengthRev = 0
  Solid = true
  Symmetric = false
  TaperAngle = -3
FEATURE [Part::Cut] Cut008  label="M8 35mm002"
  Base = -> Fusion004
  Placement = pos=(0,0,-19.05) rot=(0,0,1;0rad)
  Tool = -> Extrude003
FEATURE [Part::Cylinder] Cylinder031
  Angle = 360
  AttacherType = Attacher::AttachEngine3D
  FirstAngle = 0
  Height = 35
  Radius = 4
  SecondAngle = 0
FEATURE [Part::Cylinder] Cylinder032
  Angle = 360
  AttacherType = Attacher::AttachEngine3D
  FirstAngle = 0
  Height = 2.5
  Radius = 8
  SecondAngle = 0
FEATURE [Part::MultiFuse] Fusion005
  Shapes = -> [Cylinder031,Cylinder032]
FEATURE [Part::RegularPolygon] RegularPolygon004  label="Regular polygon004"
  AttacherType = Attacher::AttachEngine3D
  Circumradius = 3
  Polygon = 6
FEATURE [Part::Extrusion] Extrude004
  Base = -> RegularPolygon004
  Dir = (0,0,1)
  DirMode = 2
  FaceMakerClass = Part::FaceMakerBullseye
  LengthFwd = 3
  LengthRev = 0
  Solid = true
  Symmetric = false
  TaperAngle = -3
FEATURE [Part::Cut] Cut009  label="M8 35mm003"
  Base = -> Fusion005
  Placement = pos=(-19.05,0,-19.05) rot=(0,0,1;0rad)
  Tool = -> Extrude004
FEATURE [Part::Box] Box012  label="Cube012"
  AttacherType = Attacher::AttachEngine3D
  Height = 6.35
  Length = 12.7
  Width = 12.7
FEATURE [Part::Cylinder] Cylinder033
  Angle = 360
  AttacherType = Attacher::AttachEngine3D
  FirstAngle = 0
  Height = 10
  Placement = pos=(6.35,6.35,0) rot=(0,0,1;0rad)
  Radius = 4
  SecondAngle = 0
FEATURE [Part::Cut] Cut010  label="M8 Nut"
  Base = -> Box012
  Refine = true
  Tool = -> Cylinder033
FEATURE [Part::Box] Box013  label="Cube013"
  AttacherType = Attacher::AttachEngine3D
  Height = 3
  Length = 9.525
  Placement = pos=(1.62052,1.55448,0) rot=(0,0,1;0rad)
  Width = 9.525
FEATURE [Part::Cylinder] Cylinder034
  Angle = 360
  AttacherType = Attacher::AttachEngine3D
  FirstAngle = 0
  Height = 3
  Placement = pos=(6.35,6.35,0) rot=(0,0,1;0rad)
  Radius = 3
  SecondAngle = 0
FEATURE [Part::Cut] Cut011  label="M6 Nut"
  Base = -> Box013
  Placement = pos=(0,-40.4165,0) rot=(0,0,1;0rad)
  Refine = true
  Tool = -> Cylinder034
FEATURE [App::DocumentObjectGroup] Group011  label="Nuts"
  Group = -> [Cut010,Cut011]
FEATURE [Part::Box] Box014  label="Cube014"
  AttacherType = Attacher::AttachEngine3D
  Height = 6.35
  Length = 12.7
  Width = 12.7
FEATURE [Part::Cylinder] Cylinder035
  Angle = 360
  AttacherType = Attacher::AttachEngine3D
  FirstAngle = 0
  Height = 10
  Placement = pos=(6.35,6.35,0) rot=(0,0,1;0rad)
  Radius = 4
  SecondAngle = 0
FEATURE [Part::Cut] Cut012  label="M8 Nut001"
  Base = -> Box014
  Placement = pos=(-6.35,-6.35,0) rot=(0,0,1;0rad)
  Refine = true
  Tool = -> Cylinder035
FEATURE [Part::Box] Box015  label="Cube015"
  AttacherType = Attacher::AttachEngine3D
  Height = 6.35
  Length = 12.7
  Width = 12.7
FEATURE [Part::Cylinder] Cylinder036
  Angle = 360
  AttacherType = Attacher::AttachEngine3D
  FirstAngle = 0
  Height = 10
  Placement = pos=(6.35,6.35,0) rot=(0,0,1;0rad)
  Radius = 4
  SecondAngle = 0
FEATURE [Part::Cut] Cut013  label="M8 Nut002"
  Base = -> Box015
  Placement = pos=(12.7,-6.35,0) rot=(0,0,1;0rad)
  Refine = true
  Tool = -> Cylinder036
FEATURE [Part::Box] Box016  label="Cube016"
  AttacherType = Attacher::AttachEngine3D
  Height = 6.35
  Length = 12.7
  Width = 12.7
FEATURE [Part::Cylinder] Cylinder037
  Angle = 360
  AttacherType = Attacher::AttachEngine3D
  FirstAngle = 0
  Height = 10
  Placement = pos=(6.35,6.35,0) rot=(0,0,1;0rad)
  Radius = 4
  SecondAngle = 0
FEATURE [Part::Cut] Cut014  label="M8 Nut003"
  Base = -> Box016
  Placement = pos=(-25.4,-6.35,0) rot=(0,0,1;0rad)
  Refine = true
  Tool = -> Cylinder037
FEATURE [App::DocumentObjectGroup] Group013  label="Upper"
  Group = -> [Cut012,Cut013,Cut014]
FEATURE [Part::Box] Box017  label="Cube017"
  AttacherType = Attacher::AttachEngine3D
  Height = 6.35
  Length = 12.7
  Width = 12.7
FEATURE [Part::Box] Box018  label="Cube018"
  AttacherType = Attacher::AttachEngine3D
  Height = 6.35
  Length = 12.7
  Width = 12.7
FEATURE [Part::Box] Box019  label="Cube019"
  AttacherType = Attacher::AttachEngine3D
  Height = 6.35
  Length = 12.7
  Width = 12.7
FEATURE [Part::Cylinder] Cylinder038
  Angle = 360
  AttacherType = Attacher::AttachEngine3D
  FirstAngle = 0
  Height = 10
  Placement = pos=(6.35,6.35,0) rot=(0,0,1;0rad)
  Radius = 4
  SecondAngle = 0
FEATURE [Part::Cut] Cut015  label="M8 Nut004"
  Base = -> Box017
  Placement = pos=(-6.35,-6.35,908.05) rot=(0,0,1;0rad)
  Refine = true
  Tool = -> Cylinder038
FEATURE [Part::Cylinder] Cylinder039
  Angle = 360
  AttacherType = Attacher::AttachEngine3D
  FirstAngle = 0
  Height = 10
  Placement = pos=(6.35,6.35,0) rot=(0,0,1;0rad)
  Radius = 4
  SecondAngle = 0
FEATURE [Part::Cut] Cut016  label="M8 Nut005"
  Base = -> Box018
  Placement = pos=(12.7,-6.35,908.05) rot=(0,0,1;0rad)
  Refine = true
  Tool = -> Cylinder039
FEATURE [Part::Cylinder] Cylinder040
  Angle = 360
  AttacherType = Attacher::AttachEngine3D
  FirstAngle = 0
  Height = 10
  Placement = pos=(6.35,6.35,0) rot=(0,0,1;0rad)
  Radius = 4
  SecondAngle = 0
FEATURE [Part::Cut] Cut017  label="M8 Nut006"
  Base = -> Box019
  Placement = pos=(-25.4,-6.35,908.05) rot=(0,0,1;0rad)
  Refine = true
  Tool = -> Cylinder040
FEATURE [App::DocumentObjectGroup] Group015  label="Lower"
  Group = -> [Cut015,Cut016,Cut017]
FEATURE [App::DocumentObjectGroup] Group012  label="Mast Nuts"
  Group = -> [Group013,Group015]
FEATURE [Part::Cylinder] Cylinder041
  Angle = 360
  AttacherType = Attacher::AttachEngine3D
  FirstAngle = 0
  Height = 35
  Radius = 4
  SecondAngle = 0
FEATURE [Part::Cylinder] Cylinder042
  Angle = 360
  AttacherType = Attacher::AttachEngine3D
  FirstAngle = 0
  Height = 2.5
  Radius = 8
  SecondAngle = 0
FEATURE [Part::MultiFuse] Fusion006
  Shapes = -> [Cylinder041,Cylinder042]
FEATURE [Part::RegularPolygon] RegularPolygon005  label="Regular polygon005"
  AttacherType = Attacher::AttachEngine3D
  Circumradius = 3
  Polygon = 6
FEATURE [Part::Extrusion] Extrude005
  Base = -> RegularPolygon005
  Dir = (0,0,1)
  DirMode = 2
  FaceMakerClass = Part::FaceMakerBullseye
  LengthFwd = 3
  LengthRev = 0
  Solid = true
  Symmetric = false
  TaperAngle = -3
FEATURE [Part::Cut] Cut018  label="M8 35mm004"
  Base = -> Fusion006
  Placement = pos=(19.05,0,933.45) rot=(1,0,0;3.14159rad)
  Tool = -> Extrude005
FEATURE [Part::Cylinder] Cylinder043
  Angle = 360
  AttacherType = Attacher::AttachEngine3D
  FirstAngle = 0
  Height = 35
  Radius = 4
  SecondAngle = 0
FEATURE [Part::Cylinder] Cylinder044
  Angle = 360
  AttacherType = Attacher::AttachEngine3D
  FirstAngle = 0
  Height = 2.5
  Radius = 8
  SecondAngle = 0
FEATURE [Part::MultiFuse] Fusion007
  Shapes = -> [Cylinder043,Cylinder044]
FEATURE [Part::RegularPolygon] RegularPolygon006  label="Regular polygon006"
  AttacherType = Attacher::AttachEngine3D
  Circumradius = 3
  Polygon = 6
FEATURE [Part::Extrusion] Extrude006
  Base = -> RegularPolygon006
  Dir = (0,0,1)
  DirMode = 2
  FaceMakerClass = Part::FaceMakerBullseye
  LengthFwd = 3
  LengthRev = 0
  Solid = true
  Symmetric = false
  TaperAngle = -3
FEATURE [Part::Cut] Cut019  label="M8 35mm005"
  Base = -> Fusion007
  Placement = pos=(4e-15,0,933.45) rot=(1,0,0;3.14159rad)
  Tool = -> Extrude006
FEATURE [Part::Cylinder] Cylinder045
  Angle = 360
  AttacherType = Attacher::AttachEngine3D
  FirstAngle = 0
  Height = 35
  Radius = 4
  SecondAngle = 0
FEATURE [Part::Cylinder] Cylinder046
  Angle = 360
  AttacherType = Attacher::AttachEngine3D
  FirstAngle = 0
  Height = 2.5
  Radius = 8
  SecondAngle = 0
FEATURE [Part::MultiFuse] Fusion008
  Shapes = -> [Cylinder045,Cylinder046]
FEATURE [Part::RegularPolygon] RegularPolygon007  label="Regular polygon007"
  AttacherType = Attacher::AttachEngine3D
  Circumradius = 3
  Polygon = 6
FEATURE [Part::Extrusion] Extrude007
  Base = -> RegularPolygon007
  Dir = (0,0,1)
  DirMode = 2
  FaceMakerClass = Part::FaceMakerBullseye
  LengthFwd = 3
  LengthRev = 0
  Solid = true
  Symmetric = false
  TaperAngle = -3
FEATURE [Part::Cut] Cut020  label="M8 35mm006"
  Base = -> Fusion008
  Placement = pos=(-19.05,0,933.45) rot=(1,0,0;3.14159rad)
  Tool = -> Extrude007
FEATURE [Part::Box] Box020  label="Cube020"
  AttacherType = Attacher::AttachEngine3D
  Height = 52.3875
  Length = 60.325
  Placement = pos=(-30.1625,-11.1125,-1.5875) rot=(0,0,1;0rad)
  Width = 22.225
FEATURE [App::DocumentObjectGroup] Group016  label="M8"
  Group = -> [Cut007,Cut008,Cut009,Cut018,Cut019,Cut020]
FEATURE [Part::Cylinder] Cylinder051
  Angle = 360
  AttacherType = Attacher::AttachEngine3D
  FirstAngle = 0
  Height = 35
  Radius = 4
  SecondAngle = 0
FEATURE [Part::Cylinder] Cylinder052
  Angle = 360
  AttacherType = Attacher::AttachEngine3D
  FirstAngle = 0
  Height = 2.5
  Radius = 8
  SecondAngle = 0
FEATURE [Part::MultiFuse] Fusion010
  Shapes = -> [Cylinder051,Cylinder052]
FEATURE [Part::RegularPolygon] RegularPolygon009  label="Regular polygon009"
  AttacherType = Attacher::AttachEngine3D
  Circumradius = 3
  Polygon = 6
FEATURE [Part::Extrusion] Extrude009
  Base = -> RegularPolygon009
  Dir = (0,0,1)
  DirMode = 2
  FaceMakerClass = Part::FaceMakerBullseye
  LengthFwd = 3
  LengthRev = 0
  Solid = true
  Symmetric = false
  TaperAngle = -3
FEATURE [Part::Cut] Cut023  label="M8 35mm007"
  Base = -> Fusion010
  Placement = pos=(-19.05,0,933.45) rot=(1,0,0;3.14159rad)
  Tool = -> Extrude009
FEATURE [App::DocumentObjectGroup] Group017  label="Mast M6 Screws"
  Group = -> [Cut023]
FEATURE [App::DocumentObjectGroup] Group010  label="Mast Screws"
  Group = -> [Group016,Group017]
FEATURE [Part::Cut] Cut024  label="Steel Cap"
  Base = -> Box020
  Refine = true
  Tool = -> Box010
FEATURE [Part::Box] Box022  label="Cube022"
  AttacherType = Attacher::AttachEngine3D
  Height = 50.8
  Length = 57.15
  Placement = pos=(-28.575,-9.525,0) rot=(0,0,1;0rad)
  Width = 19.05
FEATURE [Part::Box] Box023  label="Cube023"
  AttacherType = Attacher::AttachEngine3D
  Height = 52.3875
  Length = 60.325
  Placement = pos=(-30.1625,-11.1125,-1.5875) rot=(0,0,1;0rad)
  Width = 22.225
FEATURE [Part::Cut] Cut025  label="Steel Cap001"
  Base = -> Box023
  Placement = pos=(0,0,914.4) rot=(1,0,0;3.14159rad)
  Refine = true
  Tool = -> Box022
FEATURE [App::DocumentObjectGroup] Group018  label="Mast Rods"
  Group = -> [Body028,Body029,Body030]
FEATURE [Sketcher::SketchObject] Sketch045
  FullyConstrained = true
  MapMode = 5
  Support = -> [XY_Plane042]
  sketch-geometry (30):
    g0-g6: Circle x7 (B-spline internal-alignment scaffolding for g7; pole/knot coordinates omitted)
    g7: BSplineCurve PolesCount=7 KnotsCount=5 Degree=3 IsPeriodic=0
    g8-g12: GeomPoint x5 (B-spline internal-alignment scaffolding for g7; pole/knot coordinates omitted)
    g13-g19: Circle x7 (B-spline internal-alignment scaffolding for g20; pole/knot coordinates omitted)
    g20: BSplineCurve PolesCount=7 KnotsCount=5 Degree=3 IsPeriodic=0
    g21-g25: GeomPoint x5 (B-spline internal-alignment scaffolding for g20; pole/knot coordinates omitted)
    g26: LineSegment StartX=-30.5 StartY=11.5 StartZ=0 EndX=30.5 EndY=11.5 EndZ=0
    g27: LineSegment StartX=30.5 StartY=11.5 StartZ=0 EndX=30.5 EndY=-11.5 EndZ=0
    g28: LineSegment StartX=30.5 StartY=-11.5 StartZ=0 EndX=-30.5 EndY=-11.5 EndZ=0
    g29: LineSegment StartX=-30.5 StartY=-11.5 StartZ=0 EndX=-30.5 EndY=11.5 EndZ=0
  constraints (40):
    c: Weight(g0) = 1
    c: PointOnObject(g7,g-1)
    c: Equal(g0, g1-g6) x6
    c: PointOnObject(g7,g-1)
    c: InternalAlignment(g0-g6 -> g7) x7
    c: InternalAlignment(g8-g12 -> g7) x5
    c: Weight(g13) = 1
    c: Coincident(g20,g7)
    c: Equal(g13, g14-g19) x6
    c: Coincident(g20,g7)
    c: InternalAlignment(g13-g19 -> g20) x7
    c: InternalAlignment(g21-g25 -> g20) x5
    c: Symmetric(g5,g18,g-1)
    c: Symmetric(g17,g4,g-1)
    c: Symmetric(g16,g3,g-1)
    c: Symmetric(g15,g2,g-1)
    c: Symmetric(g14,g1,g-1)
    c: Coincident(g26,g27)
    c: Coincident(g27,g28)
    c: Coincident(g28,g29)
    c: Coincident(g29,g26)
    c: Horizontal(g26)
    c: Horizontal(g28)
    c: Vertical(g27)
    c: Vertical(g29)
    c: DistanceX(g26,g26) = 61
    c: DistanceX(g26,g-1) = 30.5
    c: DistanceY(g27,g26) = 23
    c: DistanceY(g26,g9) = 1
    c: DistanceX(g9,g26) = 1
    c: DistanceY(g26,g3) = 1.5
    c: DistanceY(g26,g11) = 1
    c: DistanceX(g26,g11) = 1
    c: Symmetric(g2,g4,g-2)
    c: DistanceX(g16,g-1) = 0
    c: DistanceX(g-1,g7) = 63.5
    c: DistanceX(g7,g-1) = 63.5
    c: DistanceY(g7,g5) = 7.1374
    c: DistanceX(g5,g7) = 16.5608
    c: DistanceY(g27,g-1) = 11.5
FEATURE [PartDesign::Pad] Pad
  Direction = (0,0,1)
  Length = 103.188
  Length2 = 10
  Profile = -> Sketch045
  ReferenceAxis = -> Sketch045 [N_Axis]
  Type = 0
FEATURE [PartDesign::Body] Body039  label="Mast001"
  Group = -> [Sketch045,Pad]
  Origin = -> Origin042
  Placement = pos=(0,0,812.8) rot=(0,0,1;0rad)
  Tip = -> Pad
FEATURE [Sketcher::SketchObject] Sketch047
  FullyConstrained = true
  MapMode = 5
  Support = -> [XY_Plane044]
  sketch-geometry (8):
    g0: LineSegment StartX=-30.1625 StartY=11.1125 StartZ=0 EndX=30.1625 EndY=11.1125 EndZ=0
    g1: LineSegment StartX=30.1625 StartY=11.1125 StartZ=0 EndX=30.1625 EndY=-11.1125 EndZ=0
    g2: LineSegment StartX=30.1625 StartY=-11.1125 StartZ=0 EndX=-30.1625 EndY=-11.1125 EndZ=0
    g3: LineSegment StartX=-30.1625 StartY=-11.1125 StartZ=0 EndX=-30.1625 EndY=11.1125 EndZ=0
    g4: LineSegment StartX=-31.75 StartY=12.7 StartZ=0 EndX=31.75 EndY=12.7 EndZ=0
    g5: LineSegment StartX=31.75 StartY=12.7 StartZ=0 EndX=31.75 EndY=-12.7 EndZ=0
    g6: LineSegment StartX=31.75 StartY=-12.7 StartZ=0 EndX=-31.75 EndY=-12.7 EndZ=0
    g7: LineSegment StartX=-31.75 StartY=-12.7 StartZ=0 EndX=-31.75 EndY=12.7 EndZ=0
  constraints (24):
    c: Coincident(g0,g1)
    c: Coincident(g1,g2)
    c: Coincident(g2,g3)
    c: Coincident(g3,g0)
    c: Horizontal(g0)
    c: Horizontal(g2)
    c: Vertical(g1)
    c: Vertical(g3)
    c: DistanceX(g0,g0) = 60.325
    c: DistanceX(g0,g-1) = 30.1625
    c: DistanceY(g1,g0) = 22.225
    c: DistanceY(g1,g-1) = 11.1125
    c: Coincident(g4,g5)
    c: Coincident(g5,g6)
    c: Coincident(g6,g7)
    c: Coincident(g7,g4)
    c: Horizontal(g4)
    c: Horizontal(g6)
    c: Vertical(g5)
    c: Vertical(g7)
    c: DistanceX(g6) = -31.75
    c: DistanceY(g6) = -12.7
    c: DistanceX(g4) = 31.75
    c: DistanceY(g4) = 12.7
FEATURE [Sketcher::SketchObject] Sketch048
  FullyConstrained = true
  MapMode = 5
  Support = -> [XY_Plane045]
  sketch-geometry (8):
    g0: LineSegment StartX=-28.575 StartY=9.525 StartZ=0 EndX=28.575 EndY=9.525 EndZ=0
    g1: LineSegment StartX=28.575 StartY=9.525 StartZ=0 EndX=28.575 EndY=-9.525 EndZ=0
    g2: LineSegment StartX=28.575 StartY=-9.525 StartZ=0 EndX=-28.575 EndY=-9.525 EndZ=0
    g3: LineSegment StartX=-28.575 StartY=-9.525 StartZ=0 EndX=-28.575 EndY=9.525 EndZ=0
    g4: LineSegment StartX=-31.75 StartY=12.7 StartZ=0 EndX=31.75 EndY=12.7 EndZ=0
    g5: LineSegment StartX=31.75 StartY=12.7 StartZ=0 EndX=31.75 EndY=-12.7 EndZ=0
    g6: LineSegment StartX=31.75 StartY=-12.7 StartZ=0 EndX=-31.75 EndY=-12.7 EndZ=0
    g7: LineSegment StartX=-31.75 StartY=-12.7 StartZ=0 EndX=-31.75 EndY=12.7 EndZ=0
  constraints (24):
    c: Coincident(g0,g1)
    c: Coincident(g1,g2)
    c: Coincident(g2,g3)
    c: Coincident(g3,g0)
    c: Horizontal(g0)
    c: Horizontal(g2)
    c: Vertical(g1)
    c: Vertical(g3)
    c: DistanceX(g0,g0) = 57.15
    c: DistanceX(g0,g-1) = 28.575
    c: DistanceY(g1,g0) = 19.05
    c: DistanceY(g1,g-1) = 9.525
    c: Coincident(g4,g5)
    c: Coincident(g5,g6)
    c: Coincident(g6,g7)
    c: Coincident(g7,g4)
    c: Horizontal(g4)
    c: Horizontal(g6)
    c: Vertical(g5)
    c: Vertical(g7)
    c: DistanceX(g6) = -31.75
    c: DistanceY(g6) = -12.7
    c: DistanceX(g4) = 31.75
    c: DistanceY(g4) = 12.7
FEATURE [PartDesign::Pad] Pad033
  Direction = (0,0,1)
  Length = 52.3875
  Length2 = 10
  Profile = -> Sketch047
  ReferenceAxis = -> Sketch047 [N_Axis]
  Type = 0
FEATURE [PartDesign::Pad] Pad032
  Direction = (0,0,1)
  Length = 101.6
  Length2 = 10
  Profile = -> Sketch048
  ReferenceAxis = -> Sketch048 [N_Axis]
  Type = 0
FEATURE [Sketcher::SketchObject] Sketch051
  FullyConstrained = true
  MapMode = 5
  Support = -> [XY_Plane048]
  sketch-geometry (30):
    g0-g6: Circle x7 (B-spline internal-alignment scaffolding for g7; pole/knot coordinates omitted)
    g7: BSplineCurve PolesCount=7 KnotsCount=5 Degree=3 IsPeriodic=0
    g8-g12: GeomPoint x5 (B-spline internal-alignment scaffolding for g7; pole/knot coordinates omitted)
    g13-g19: Circle x7 (B-spline internal-alignment scaffolding for g20; pole/knot coordinates omitted)
    g20: BSplineCurve PolesCount=7 KnotsCount=5 Degree=3 IsPeriodic=0
    g21-g25: GeomPoint x5 (B-spline internal-alignment scaffolding for g20; pole/knot coordinates omitted)
    g26: LineSegment StartX=-28.575 StartY=9.525 StartZ=0 EndX=28.575 EndY=9.525 EndZ=0
    g27: LineSegment StartX=28.575 StartY=9.525 StartZ=0 EndX=28.575 EndY=-9.525 EndZ=0
    g28: LineSegment StartX=28.575 StartY=-9.525 StartZ=0 EndX=-28.575 EndY=-9.525 EndZ=0
    g29: LineSegment StartX=-28.575 StartY=-9.525 StartZ=0 EndX=-28.575 EndY=9.525 EndZ=0
  constraints (40):
    c: Weight(g0) = 1
    c: PointOnObject(g7,g-1)
    c: Equal(g0, g1-g6) x6
    c: PointOnObject(g7,g-1)
    c: InternalAlignment(g0-g6 -> g7) x7
    c: InternalAlignment(g8-g12 -> g7) x5
    c: Weight(g13) = 1
    c: Coincident(g20,g7)
    c: Equal(g13, g14-g19) x6
    c: Coincident(g20,g7)
    c: InternalAlignment(g13-g19 -> g20) x7
    c: InternalAlignment(g21-g25 -> g20) x5
    c: Symmetric(g5,g18,g-1)
    c: Symmetric(g17,g4,g-1)
    c: Symmetric(g16,g3,g-1)
    c: Symmetric(g15,g2,g-1)
    c: Symmetric(g14,g1,g-1)
    c: Coincident(g26,g27)
    c: Coincident(g27,g28)
    c: Coincident(g28,g29)
    c: Coincident(g29,g26)
    c: Horizontal(g26)
    c: Horizontal(g28)
    c: Vertical(g27)
    c: Vertical(g29)
    c: DistanceX(g26,g26) = 57.15
    c: DistanceX(g26,g-1) = 28.575
    c: DistanceY(g27,g26) = 19.05
    c: Symmetric(g2,g4,g-2)
    c: DistanceX(g16,g-1) = 0
    c: DistanceX(g-1,g7) = 63.5
    c: DistanceX(g7,g-1) = 63.5
    c: DistanceY(g7,g5) = 7.1374
    c: DistanceX(g5,g7) = 16.5608
    c: DistanceY(g27,g-1) = 9.525
    c: DistanceX(g2) = -33.3046
    c: DistanceY(g2) = 14.1018
    c: DistanceX(g1) = -46.9392
    c: DistanceY(g1) = 7.1374
    c: DistanceY(g10) = 13.1089
FEATURE [Sketcher::SketchObject] Sketch052
  AttachmentOffset = pos=(0,0,50.8) rot=(0,0,1;0rad)
  FullyConstrained = true
  MapMode = 5
  Placement = pos=(0,0,50.8) rot=(0,0,1;0rad)
  Support = -> [XY_Plane048]
  sketch-geometry (30):
    g0-g6: Circle x7 (B-spline internal-alignment scaffolding for g7; pole/knot coordinates omitted)
    g7: BSplineCurve PolesCount=7 KnotsCount=5 Degree=3 IsPeriodic=0
    g8-g12: GeomPoint x5 (B-spline internal-alignment scaffolding for g7; pole/knot coordinates omitted)
    g13-g19: Circle x7 (B-spline internal-alignment scaffolding for g20; pole/knot coordinates omitted)
    g20: BSplineCurve PolesCount=7 KnotsCount=5 Degree=3 IsPeriodic=0
    g21-g25: GeomPoint x5 (B-spline internal-alignment scaffolding for g20; pole/knot coordinates omitted)
    g26: LineSegment StartX=-28.575 StartY=9.525 StartZ=0 EndX=28.575 EndY=9.525 EndZ=0
    g27: LineSegment StartX=28.575 StartY=9.525 StartZ=0 EndX=28.575 EndY=-9.525 EndZ=0
    g28: LineSegment StartX=28.575 StartY=-9.525 StartZ=0 EndX=-28.575 EndY=-9.525 EndZ=0
    g29: LineSegment StartX=-28.575 StartY=-9.525 StartZ=0 EndX=-28.575 EndY=9.525 EndZ=0
  constraints (40):
    c: Weight(g0) = 1
    c: PointOnObject(g7,g-1)
    c: Equal(g0, g1-g6) x6
    c: PointOnObject(g7,g-1)
    c: InternalAlignment(g0-g6 -> g7) x7
    c: InternalAlignment(g8-g12 -> g7) x5
    c: Weight(g13) = 1
    c: Coincident(g20,g7)
    c: Equal(g13, g14-g19) x6
    c: Coincident(g20,g7)
    c: InternalAlignment(g13-g19 -> g20) x7
    c: InternalAlignment(g21-g25 -> g20) x5
    c: Symmetric(g5,g18,g-1)
    c: Symmetric(g17,g4,g-1)
    c: Symmetric(g16,g3,g-1)
    c: Symmetric(g15,g2,g-1)
    c: Symmetric(g14,g1,g-1)
    c: Coincident(g26,g27)
    c: Coincident(g27,g28)
    c: Coincident(g28,g29)
    c: Coincident(g29,g26)
    c: Horizontal(g26)
    c: Horizontal(g28)
    c: Vertical(g27)
    c: Vertical(g29)
    c: DistanceX(g26,g26) = 57.15
    c: DistanceX(g26,g-1) = 28.575
    c: DistanceY(g27,g26) = 19.05
    c: DistanceY(g27,g-1) = 9.525
    c: DistanceY(g26,g9) = 1
    c: DistanceX(g9,g26) = 1
    c: DistanceY(g26,g3) = 1.5
    c: DistanceY(g26,g11) = 1
    c: DistanceX(g26,g11) = 1
    c: Symmetric(g2,g4,g-2)
    c: DistanceX(g16,g-1) = 0
    c: DistanceX(g-1,g7) = 63.5
    c: DistanceX(g7,g-1) = 63.5
    c: DistanceY(g7,g5) = 7.1374
    c: DistanceX(g5,g7) = 16.5608
FEATURE [PartDesign::AdditiveLoft] AdditiveLoft002
  Closed = false
  Profile = -> Sketch051
  Ruled = false
  Sections = -> [Sketch052]
FEATURE [PartDesign::Body] Body045  label="Upper 2 Inch Thick Aero"
  Group = -> [Sketch051,Sketch052,AdditiveLoft002]
  Origin = -> Origin048
  Placement = pos=(0,0,152.4) rot=(0,0,1;0rad)
  Tip = -> AdditiveLoft002
FEATURE [Sketcher::SketchObject] Sketch053
  FullyConstrained = true
  MapMode = 5
  Support = -> [XY_Plane049]
  sketch-geometry (30):
    g0-g6: Circle x7 (B-spline internal-alignment scaffolding for g7; pole/knot coordinates omitted)
    g7: BSplineCurve PolesCount=7 KnotsCount=5 Degree=3 IsPeriodic=0
    g8-g12: GeomPoint x5 (B-spline internal-alignment scaffolding for g7; pole/knot coordinates omitted)
    g13-g19: Circle x7 (B-spline internal-alignment scaffolding for g20; pole/knot coordinates omitted)
    g20: BSplineCurve PolesCount=7 KnotsCount=5 Degree=3 IsPeriodic=0
    g21-g25: GeomPoint x5 (B-spline internal-alignment scaffolding for g20; pole/knot coordinates omitted)
    g26: LineSegment StartX=-28.575 StartY=10 StartZ=0 EndX=28.575 EndY=10 EndZ=0
    g27: LineSegment StartX=28.575 StartY=10 StartZ=0 EndX=28.575 EndY=-10 EndZ=0
    g28: LineSegment StartX=28.575 StartY=-10 StartZ=0 EndX=-28.575 EndY=-10 EndZ=0
    g29: LineSegment StartX=-28.575 StartY=-10 StartZ=0 EndX=-28.575 EndY=10 EndZ=0
  constraints (40):
    c: Weight(g0) = 1
    c: PointOnObject(g7,g-1)
    c: Equal(g0, g1-g6) x6
    c: PointOnObject(g7,g-1)
    c: InternalAlignment(g0-g6 -> g7) x7
    c: InternalAlignment(g8-g12 -> g7) x5
    c: Weight(g13) = 1
    c: Coincident(g20,g7)
    c: Equal(g13, g14-g19) x6
    c: Coincident(g20,g7)
    c: InternalAlignment(g13-g19 -> g20) x7
    c: InternalAlignment(g21-g25 -> g20) x5
    c: Symmetric(g5,g18,g-1)
    c: Symmetric(g17,g4,g-1)
    c: Symmetric(g16,g3,g-1)
    c: Symmetric(g15,g2,g-1)
    c: Symmetric(g14,g1,g-1)
    c: Coincident(g26,g27)
    c: Coincident(g27,g28)
    c: Coincident(g28,g29)
    c: Coincident(g29,g26)
    c: Horizontal(g26)
    c: Horizontal(g28)
    c: Vertical(g27)
    c: Vertical(g29)
    c: DistanceX(g26,g26) = 57.15
    c: DistanceX(g26,g-1) = 28.575
    c: DistanceY(g27,g26) = 20
    c: Symmetric(g2,g4,g-2)
    c: DistanceX(g16,g-1) = 0
    c: DistanceX(g-1,g7) = 63.5
    c: DistanceX(g7,g-1) = 63.5
    c: DistanceY(g7,g5) = 7.1374
    c: DistanceX(g5,g7) = 16.5608
    c: DistanceY(g27,g-1) = 10
    c: DistanceX(g1) = -46.9392
    c: DistanceY(g1) = 7.15
    c: DistanceY(g-1,g3) = 13
    c: DistanceX(g2) = -33.6961
    c: DistanceY(g2) = 14.6719
FEATURE [Sketcher::SketchObject] Sketch054
  AttachmentOffset = pos=(0,0,50.8) rot=(0,0,1;0rad)
  FullyConstrained = true
  MapMode = 5
  Placement = pos=(0,0,50.8) rot=(0,0,1;0rad)
  Support = -> [XY_Plane049]
  sketch-geometry (30):
    g0-g6: Circle x7 (B-spline internal-alignment scaffolding for g7; pole/knot coordinates omitted)
    g7: BSplineCurve PolesCount=7 KnotsCount=5 Degree=3 IsPeriodic=0
    g8-g12: GeomPoint x5 (B-spline internal-alignment scaffolding for g7; pole/knot coordinates omitted)
    g13-g19: Circle x7 (B-spline internal-alignment scaffolding for g20; pole/knot coordinates omitted)
    g20: BSplineCurve PolesCount=7 KnotsCount=5 Degree=3 IsPeriodic=0
    g21-g25: GeomPoint x5 (B-spline internal-alignment scaffolding for g20; pole/knot coordinates omitted)
    g26: LineSegment StartX=-28.575 StartY=9.525 StartZ=0 EndX=28.575 EndY=9.525 EndZ=0
    g27: LineSegment StartX=28.575 StartY=9.525 StartZ=0 EndX=28.575 EndY=-9.525 EndZ=0
    g28: LineSegment StartX=28.575 StartY=-9.525 StartZ=0 EndX=-28.575 EndY=-9.525 EndZ=0
    g29: LineSegment StartX=-28.575 StartY=-9.525 StartZ=0 EndX=-28.575 EndY=9.525 EndZ=0
  constraints (40):
    c: Weight(g0) = 1
    c: PointOnObject(g7,g-1)
    c: Equal(g0, g1-g6) x6
    c: PointOnObject(g7,g-1)
    c: InternalAlignment(g0-g6 -> g7) x7
    c: InternalAlignment(g8-g12 -> g7) x5
    c: Weight(g13) = 1
    c: Coincident(g20,g7)
    c: Equal(g13, g14-g19) x6
    c: Coincident(g20,g7)
    c: InternalAlignment(g13-g19 -> g20) x7
    c: InternalAlignment(g21-g25 -> g20) x5
    c: Symmetric(g5,g18,g-1)
    c: Symmetric(g17,g4,g-1)
    c: Symmetric(g16,g3,g-1)
    c: Symmetric(g15,g2,g-1)
    c: Symmetric(g14,g1,g-1)
    c: Coincident(g26,g27)
    c: Coincident(g27,g28)
    c: Coincident(g28,g29)
    c: Coincident(g29,g26)
    c: Horizontal(g26)
    c: Horizontal(g28)
    c: Vertical(g27)
    c: Vertical(g29)
    c: DistanceX(g26,g26) = 57.15
    c: DistanceX(g26,g-1) = 28.575
    c: DistanceY(g27,g26) = 19.05
    c: DistanceY(g27,g-1) = 9.525
    c: DistanceY(g26,g9) = 1
    c: DistanceX(g9,g26) = 1
    c: DistanceY(g26,g3) = 1.5
    c: DistanceY(g26,g11) = 1
    c: DistanceX(g26,g11) = 1
    c: Symmetric(g2,g4,g-2)
    c: DistanceX(g16,g-1) = 0
    c: DistanceX(g-1,g7) = 63.5
    c: DistanceX(g7,g-1) = 63.5
    c: DistanceY(g7,g5) = 7.1374
    c: DistanceX(g5,g7) = 16.5608
FEATURE [PartDesign::AdditiveLoft] AdditiveLoft003
  Closed = false
  Profile = -> Sketch053
  Ruled = false
  Sections = -> [Sketch054]
FEATURE [PartDesign::Body] Body046  label="Lower 2 Inch Thick Aero001"
  Group = -> [Sketch053,Sketch054,AdditiveLoft003]
  Origin = -> Origin049
  Placement = pos=(0,0,812.8) rot=(0,1,0;3.14159rad)
  Tip = -> AdditiveLoft003
FEATURE [Sketcher::SketchObject] Sketch055
  AttachmentOffset = pos=(0,0,50.8) rot=(0,0,1;0rad)
  FullyConstrained = true
  MapMode = 5
  Placement = pos=(0,0,50.8) rot=(0,0,1;0rad)
  Support = -> [XY_Plane043]
  sketch-geometry (30):
    g0-g6: Circle x7 (B-spline internal-alignment scaffolding for g7; pole/knot coordinates omitted)
    g7: BSplineCurve PolesCount=7 KnotsCount=5 Degree=3 IsPeriodic=0
    g8-g12: GeomPoint x5 (B-spline internal-alignment scaffolding for g7; pole/knot coordinates omitted)
    g13-g19: Circle x7 (B-spline internal-alignment scaffolding for g20; pole/knot coordinates omitted)
    g20: BSplineCurve PolesCount=7 KnotsCount=5 Degree=3 IsPeriodic=0
    g21-g25: GeomPoint x5 (B-spline internal-alignment scaffolding for g20; pole/knot coordinates omitted)
    g26: LineSegment StartX=-28.575 StartY=9.525 StartZ=0 EndX=28.575 EndY=9.525 EndZ=0
    g27: LineSegment StartX=28.575 StartY=9.525 StartZ=0 EndX=28.575 EndY=-9.525 EndZ=0
    g28: LineSegment StartX=28.575 StartY=-9.525 StartZ=0 EndX=-28.575 EndY=-9.525 EndZ=0
    g29: LineSegment StartX=-28.575 StartY=-9.525 StartZ=0 EndX=-28.575 EndY=9.525 EndZ=0
  constraints (40):
    c: Weight(g0) = 1
    c: PointOnObject(g7,g-1)
    c: Equal(g0, g1-g6) x6
    c: PointOnObject(g7,g-1)
    c: InternalAlignment(g0-g6 -> g7) x7
    c: InternalAlignment(g8-g12 -> g7) x5
    c: Weight(g13) = 1
    c: Coincident(g20,g7)
    c: Equal(g13, g14-g19) x6
    c: Coincident(g20,g7)
    c: InternalAlignment(g13-g19 -> g20) x7
    c: InternalAlignment(g21-g25 -> g20) x5
    c: Symmetric(g5,g18,g-1)
    c: Symmetric(g17,g4,g-1)
    c: Symmetric(g16,g3,g-1)
    c: Symmetric(g15,g2,g-1)
    c: Symmetric(g14,g1,g-1)
    c: Coincident(g26,g27)
    c: Coincident(g27,g28)
    c: Coincident(g28,g29)
    c: Coincident(g29,g26)
    c: Horizontal(g26)
    c: Horizontal(g28)
    c: Vertical(g27)
    c: Vertical(g29)
    c: DistanceX(g26,g26) = 57.15
    c: DistanceX(g26,g-1) = 28.575
    c: DistanceY(g27,g26) = 19.05
    c: DistanceY(g27,g-1) = 9.525
    c: DistanceY(g26,g9) = 1
    c: DistanceX(g9,g26) = 1
    c: DistanceY(g26,g3) = 1.5
    c: DistanceY(g26,g11) = 1
    c: DistanceX(g26,g11) = 1
    c: Symmetric(g2,g4,g-2)
    c: DistanceX(g16,g-1) = 0
    c: DistanceX(g-1,g7) = 63.5
    c: DistanceX(g7,g-1) = 63.5
    c: DistanceY(g7,g5) = 7.1374
    c: DistanceX(g5,g7) = 16.5608
FEATURE [PartDesign::Pad] Pad034
  Direction = (0,0,1)
  Length = 558.8
  Length2 = 10
  Profile = -> Sketch055
  ReferenceAxis = -> Sketch055 [N_Axis]
  Type = 0
FEATURE [PartDesign::Body] Body040  label="Mast002"
  Group = -> [Sketch055,Pad034]
  Origin = -> Origin043
  Placement = pos=(0,0,152.4) rot=(0,0,1;0rad)
  Tip = -> Pad034
FEATURE [PartDesign::Fillet] Fillet002
  Base = -> Pad032 [Edge8,Edge1,Edge2,Edge5]
  BaseFeature = -> Pad032
  Radius = 0.999998
  SupportTransform = false
  UseAllEdges = false
FEATURE [PartDesign::Body] Body042  label="Mast004"
  Group = -> [Sketch048,Pad032,Fillet002]
  Origin = -> Origin045
  Placement = pos=(0,0,50.8) rot=(0,0,1;0rad)
  Tip = -> Fillet002
FEATURE [PartDesign::Fillet] Fillet003
  Base = -> Pad033 [Edge1,Edge8,Edge5,Edge2]
  BaseFeature = -> Pad033
  Radius = 0.999998
  SupportTransform = false
  UseAllEdges = false
FEATURE [PartDesign::Body] Body041  label="Mast003"
  Group = -> [Sketch047,Pad033,Fillet003]
  Origin = -> Origin044
  Placement = pos=(0,0,-1.5875) rot=(0,0,1;0rad)
  Tip = -> Fillet003
FEATURE [Part::FeaturePython] Connect001  label="Mast Support Plastic"  # WARN: FeaturePython — macro-defined, semantics opaque (R4)
  Objects = -> [Body039,Body040,Body041,Body042,Body045,Body046]
  Refine = true
  Tolerance = 0
FEATURE [Part::MultiFuse] Fusion011  label="Front Wing Support001"
  Placement = pos=(0,0,6.35) rot=(0,0,1;0rad)
  Refine = true
  Shapes = -> [Body015,Body016,Body018,Body020,Cylinder002,Cylinder008]
FEATURE [Part::Cylinder] Cylinder053
  Angle = 360
  AttacherType = Attacher::AttachEngine3D
  FirstAngle = 0
  Height = 660.4
  Placement = pos=(-318.77,-330.2,937.362) rot=(-1,0,0;1.5708rad)
  Radius = 3.429
  SecondAngle = 0
FEATURE [Part::Cylinder] Cylinder054
  Angle = 360
  AttacherType = Attacher::AttachEngine3D
  FirstAngle = 0
  Height = 711.2
  Placement = pos=(-298.831,-355.6,937.349) rot=(-1,0,0;1.5708rad)
  Radius = 3.429
  SecondAngle = 0
FEATURE [Sketcher::SketchObject] Sketch056
  FullyConstrained = true
  MapMode = 5
  Placement = pos=(0,0,0) rot=(1,0,0;1.5708rad)
  Support = -> [XZ_Plane051]
  sketch-geometry (4):
    g0: LineSegment StartX=0 StartY=0 StartZ=0 EndX=13.716 EndY=0 EndZ=0
    g1: LineSegment StartX=13.716 StartY=0 StartZ=0 EndX=13.716 EndY=-13.716 EndZ=0
    g2: LineSegment StartX=13.716 StartY=-13.716 StartZ=0 EndX=0 EndY=-13.716 EndZ=0
    g3: LineSegment StartX=0 StartY=-13.716 StartZ=0 EndX=0 EndY=0 EndZ=0
  constraints (11):
    c: Coincident(g0,g1)
    c: Coincident(g1,g2)
    c: Coincident(g2,g3)
    c: Coincident(g3,g0)
    c: Horizontal(g0)
    c: Horizontal(g2)
    c: Vertical(g1)
    c: Vertical(g3)
    c: Coincident(g0,g-1)
    c: DistanceX(g2,g1) = 13.716
    c: DistanceY(g2,g0) = 13.716
FEATURE [PartDesign::Pad] Pad035
  Direction = (0,-1,-2e-16)
  Length = 203.2
  Length2 = 10
  Placement = pos=(0,0,0) rot=(1,0,0;1.5708rad)
  Profile = -> Sketch056
  ReferenceAxis = -> Sketch056 [N_Axis]
  Type = 0
FEATURE [PartDesign::Body] Body047
  Group = -> [Sketch056,Pad035]
  Origin = -> Origin050
  Placement = pos=(-407.314,101.6,940.816) rot=(0,0,1;0rad)
  Tip = -> Pad035
FEATURE [Sketcher::SketchObject] Sketch057
  FullyConstrained = true
  MapMode = 5
  Placement = pos=(0,0,0) rot=(1,0,0;1.5708rad)
  Support = -> [XZ_Plane052]
  sketch-geometry (4):
    g0: LineSegment StartX=0 StartY=0 StartZ=0 EndX=13.716 EndY=0 EndZ=0
    g1: LineSegment StartX=13.716 StartY=0 StartZ=0 EndX=13.716 EndY=-13.716 EndZ=0
    g2: LineSegment StartX=13.716 StartY=-13.716 StartZ=0 EndX=0 EndY=-13.716 EndZ=0
    g3: LineSegment StartX=0 StartY=-13.716 StartZ=0 EndX=0 EndY=0 EndZ=0
  constraints (11):
    c: Coincident(g0,g1)
    c: Coincident(g1,g2)
    c: Coincident(g2,g3)
    c: Coincident(g3,g0)
    c: Horizontal(g0)
    c: Horizontal(g2)
    c: Vertical(g1)
    c: Vertical(g3)
    c: Coincident(g0,g-1)
    c: DistanceY(g2,g0) = 13.716
    c: DistanceX(g0,g0) = 13.716
FEATURE [PartDesign::Pad] Pad036
  Direction = (0,-1,-2e-16)
  Length = 381
  Length2 = 10
  Placement = pos=(0,0,0) rot=(1,0,0;1.5708rad)
  Profile = -> Sketch057
  ReferenceAxis = -> Sketch057 [N_Axis]
  Type = 0
FEATURE [PartDesign::Body] Body048
  Group = -> [Sketch057,Pad036]
  Origin = -> Origin051
  Placement = pos=(-387.502,190.5,940.816) rot=(0,0,1;0rad)
  Tip = -> Pad036
FEATURE [Sketcher::SketchObject] Sketch058
  FullyConstrained = true
  MapMode = 5
  Placement = pos=(0,0,0) rot=(1,0,0;1.5708rad)
  Support = -> [XZ_Plane053]
  sketch-geometry (4):
    g0: LineSegment StartX=0 StartY=0 StartZ=0 EndX=13.716 EndY=0 EndZ=0
    g1: LineSegment StartX=13.716 StartY=0 StartZ=0 EndX=13.716 EndY=-13.716 EndZ=0
    g2: LineSegment StartX=13.716 StartY=-13.716 StartZ=0 EndX=0 EndY=-13.716 EndZ=0
    g3: LineSegment StartX=0 StartY=-13.716 StartZ=0 EndX=0 EndY=0 EndZ=0
  constraints (11):
    c: Coincident(g0,g1)
    c: Coincident(g1,g2)
    c: Coincident(g2,g3)
    c: Coincident(g3,g0)
    c: Horizontal(g0)
    c: Horizontal(g2)
    c: Vertical(g1)
    c: Vertical(g3)
    c: Coincident(g0,g-1)
    c: DistanceX(g2,g1) = 13.716
    c: DistanceY(g2,g0) = 13.716
FEATURE [PartDesign::Pad] Pad037
  Direction = (0,-1,-2e-16)
  Length = 457.2
  Length2 = 10
  Placement = pos=(0,0,0) rot=(1,0,0;1.5708rad)
  Profile = -> Sketch058
  ReferenceAxis = -> Sketch058 [N_Axis]
  Type = 0
FEATURE [PartDesign::Body] Body049
  Group = -> [Sketch058,Pad037]
  Origin = -> Origin052
  Placement = pos=(-368.198,228.6,940.816) rot=(0,0,1;0rad)
  Tip = -> Pad037
FEATURE [Sketcher::SketchObject] Sketch059
  FullyConstrained = true
  MapMode = 5
  Placement = pos=(0,0,0) rot=(1,0,0;1.5708rad)
  Support = -> [XZ_Plane054]
  sketch-geometry (4):
    g0: LineSegment StartX=0 StartY=0 StartZ=0 EndX=13.716 EndY=0 EndZ=0
    g1: LineSegment StartX=13.716 StartY=0 StartZ=0 EndX=13.716 EndY=-13.716 EndZ=0
    g2: LineSegment StartX=13.716 StartY=-13.716 StartZ=0 EndX=0 EndY=-13.716 EndZ=0
    g3: LineSegment StartX=0 StartY=-13.716 StartZ=0 EndX=0 EndY=0 EndZ=0
  constraints (11):
    c: Coincident(g0,g1)
    c: Coincident(g1,g2)
    c: Coincident(g2,g3)
    c: Coincident(g3,g0)
    c: Horizontal(g0)
    c: Horizontal(g2)
    c: Vertical(g1)
    c: Vertical(g3)
    c: Coincident(g0,g-1)
    c: DistanceX(g2,g1) = 13.716
    c: DistanceY(g2,g0) = 13.716
FEATURE [PartDesign::Pad] Pad038
  Direction = (0,-1,-2e-16)
  Length = 584.2
  Length2 = 10
  Placement = pos=(0,0,0) rot=(1,0,0;1.5708rad)
  Profile = -> Sketch059
  ReferenceAxis = -> Sketch059 [N_Axis]
  Type = 0
FEATURE [PartDesign::Body] Body050
  Group = -> [Sketch059,Pad038]
  Origin = -> Origin053
  Placement = pos=(-348.386,292.1,940.816) rot=(0,0,1;0rad)
  Tip = -> Pad038
FEATURE [Part::MultiFuse] Fusion012  label="Front Wing Subract"
  Placement = pos=(0,0,6.35) rot=(0,0,1;0rad)
  Refine = true
  Shapes = -> [Cylinder054,Cylinder053,Body050,Body049,Body048,Body047]
FEATURE [Sketcher::SketchObject] Sketch063
  FullyConstrained = true
  MapMode = 5
  Placement = pos=(0,0,0) rot=(0.57735,0.57735,0.57735;2.0944rad)
  Support = -> [YZ_Plane057]
  sketch-geometry (4):
    g0: LineSegment StartX=-6.35 StartY=-12.7 StartZ=0 EndX=13.208 EndY=-12.7 EndZ=0
    g1: LineSegment StartX=13.208 StartY=-12.7 StartZ=0 EndX=13.208 EndY=6.35 EndZ=0
    g2: LineSegment StartX=13.208 StartY=6.35 StartZ=0 EndX=-6.35 EndY=6.35 EndZ=0
    g3: LineSegment StartX=-6.35 StartY=6.35 StartZ=0 EndX=-6.35 EndY=-12.7 EndZ=0
  constraints (12):
    c: Coincident(g0,g1)
    c: Coincident(g1,g2)
    c: Coincident(g2,g3)
    c: Coincident(g3,g0)
    c: Horizontal(g0)
    c: Horizontal(g2)
    c: Vertical(g1)
    c: Vertical(g3)
    c: DistanceY(g0,g1) = 19.05
    c: DistanceX(g2,g1) = 19.558
    c: DistanceX(g2) = -6.35
    c: DistanceY(g2) = 6.35
FEATURE [PartDesign::Pad] Pad042
  Direction = (1,-2e-16,3e-16)
  Length = 609.6
  Length2 = 10
  Placement = pos=(0,0,0) rot=(0.57735,0.57735,0.57735;2.0944rad)
  Profile = -> Sketch063
  ReferenceAxis = -> Sketch063 [N_Axis]
  Type = 0
FEATURE [PartDesign::Body] Body054  label="Fuselage001"
  Group = -> [Sketch063,Pad042]
  Origin = -> Origin057
  Placement = pos=(-418.998,-3.429,927.1) rot=(0,0,1;0rad)
  Tip = -> Pad042
FEATURE [PartDesign::Body] Body  label="Body054"
  Origin = -> Origin
FEATURE [App::Part] Part
  Group = -> [Body027,Pad021Body,Body]
  Origin = -> Origin027
FEATURE [Part::Part2DObjectPython] Clone2D002  label="Wing101"  # Draft 2D object (typed FeaturePython)
  Fuse = false
  Placement = pos=(0,0,0) rot=(1,0,0;1.5708rad)
  Scale = (1,1,1)
FEATURE [Sketcher::SketchObject] Sketch064
  FullyConstrained = true
  MapMode = 5
  Placement = pos=(0,0,0) rot=(1,0,0;1.5708rad)
  Support = -> [XZ_Plane060]
  sketch-geometry (9):
    g0-g4: Circle x5 (B-spline internal-alignment scaffolding for g5; pole/knot coordinates omitted)
    g5: BSplineCurve PolesCount=5 KnotsCount=3 Degree=3 IsPeriodic=0
    g6: GeomPoint X=-61.1896 Y=1.55299 Z=0
    g7: GeomPoint X=141.928 Y=11.8848 Z=0
    g8: GeomPoint X=-61.1896 Y=1.55299 Z=0
  constraints (15):
    c: Weight(g0) = 1
    c: Equal(g0, g1-g4) x4
    c: Coincident(g5,g0)
    c: InternalAlignment(g0-g4 -> g5) x5
    c: InternalAlignment(g6,g5)
    c: InternalAlignment(g7,g5)
    c: InternalAlignment(g8,g5)
    c: DistanceX(g3) = 103.059
    c: DistanceY(g3) = -5.38655
    c: DistanceX(g1) = 89.7287
    c: DistanceY(g1) = 37.6307
    c: DistanceX(g2) = 187.462
    c: DistanceY(g2) = 7.64757
    c: DistanceX(g5) = -61.1896
    c: DistanceY(g5) = 1.55299
FEATURE [Sketcher::SketchObject] Sketch065  label="Wing102"
  FullyConstrained = false
  Placement = pos=(-95.25,284.48,0) rot=(0.995037,0,0.099504;1.5708rad)
  sketch-geometry (1):
    g0: BSplineCurve PolesCount=5 KnotsCount=3 Degree=3 IsPeriodic=0
FEATURE [Sketcher::SketchObject] Sketch066  label="Wing103"
  FullyConstrained = false
  Placement = pos=(-88.9,279.4,0) rot=(0.998205,0,0.059892;1.5708rad)
  sketch-geometry (1):
    g0: BSplineCurve PolesCount=5 KnotsCount=3 Degree=3 IsPeriodic=0
FEATURE [Sketcher::SketchObject] Sketch067  label="Wing104"
  FullyConstrained = false
  Placement = pos=(-63.5,254,0) rot=(0.999201,0,0.039968;1.5708rad)
  sketch-geometry (1):
    g0: BSplineCurve PolesCount=5 KnotsCount=3 Degree=3 IsPeriodic=0
FEATURE [Sketcher::SketchObject] Sketch068  label="Wing105"
  FullyConstrained = false
  Placement = pos=(-25.4,152.4,0) rot=(0.9998,0,0.019996;1.5708rad)
  sketch-geometry (1):
    g0: BSplineCurve PolesCount=5 KnotsCount=3 Degree=3 IsPeriodic=0
FEATURE [Sketcher::SketchObject] Sketch069  label="Wing106"
  FullyConstrained = false
  Placement = pos=(0,-76.2,0) rot=(1,0,0;1.5708rad)
  sketch-geometry (1):
    g0: BSplineCurve PolesCount=5 KnotsCount=3 Degree=3 IsPeriodic=0
FEATURE [Sketcher::SketchObject] Sketch070  label="Wing1.026"
  FullyConstrained = false
  Placement = pos=(-12.7,50.8,0) rot=(-1,0,0;1.5708rad)
  sketch-geometry (1):
    g0: BSplineCurve PolesCount=5 KnotsCount=3 Degree=3 IsPeriodic=0
FEATURE [Sketcher::SketchObject] Sketch071  label="Wing1.027"
  FullyConstrained = false
  Placement = pos=(-3.81,-25.4,0) rot=(-1,0,0;1.5708rad)
  sketch-geometry (1):
    g0: BSplineCurve PolesCount=5 KnotsCount=3 Degree=3 IsPeriodic=0
FEATURE [PartDesign::AdditiveLoft] AdditiveLoft004
  Closed = false
  Placement = pos=(-95.25,284.48,0) rot=(0.995037,0,0.099504;1.5708rad)
  Profile = -> Sketch065 [Edge1]
  Ruled = false
  Sections = -> [Sketch066,Sketch067,Sketch068,Sketch070,Sketch071,Sketch069]
FEATURE [Sketcher::SketchObject] Sketch072  label="Wing107"
  FullyConstrained = false
  Placement = pos=(0,-127,0) rot=(-1,0,0;1.5708rad)
  sketch-geometry (1):
    g0: BSplineCurve PolesCount=5 KnotsCount=3 Degree=3 IsPeriodic=0
FEATURE [PartDesign::AdditiveLoft] AdditiveLoft005
  BaseFeature = -> AdditiveLoft004
  Closed = false
  Placement = pos=(-95.25,284.48,0) rot=(0.995037,0,0.099504;1.5708rad)
  Profile = -> Sketch069
  Ruled = false
  Sections = -> [Sketch072]
FEATURE [Part::Mirroring] Part__Mirroring001  label="AdditiveLoft001 (Mirror #1)001"
  Base = (0,0,0)
  Normal = (0,0,1)
  Placement = pos=(0,-253.999,3.1e-14) rot=(1,0,0;3.14159rad)
  Source = -> AdditiveLoft005
FEATURE [Sketcher::SketchObject] Sketch073  label="Wing-002"
  FullyConstrained = false
  Placement = pos=(0,-177.8,0) rot=(-1,0,0;1.5708rad)
  sketch-geometry (1):
    g0: BSplineCurve PolesCount=5 KnotsCount=3 Degree=3 IsPeriodic=0
FEATURE [PartDesign::Body] Body056  label="Front Wing002"
  Group = -> [Sketch064,Clone2D002,Sketch065,Sketch066,Sketch067,Sketch068,Sketch069,Sketch070,Sketch071,Sketch072,AdditiveLoft004,Sketch073,AdditiveLoft005]
  Origin = -> Origin059
  Tip = -> AdditiveLoft005
FEATURE [Part::MultiFuse] Fusion013
  Placement = pos=(-302.793,126.009,950.976) rot=(0,1,0;3.12414rad)
  Refine = true
  Shapes = -> [Body056,Part__Mirroring001]
FEATURE [Sketcher::SketchObject] Sketch074  label="Wing108"
  FullyConstrained = false
  Placement = pos=(0,-76.2,0) rot=(1,0,0;1.5708rad)
  sketch-geometry (1):
    g0: BSplineCurve PolesCount=5 KnotsCount=3 Degree=3 IsPeriodic=0
FEATURE [Sketcher::SketchObject] Sketch075  label="Wing109"
  FullyConstrained = false
  Placement = pos=(0,-139.7,0) rot=(-1,0,0;1.5708rad)
  sketch-geometry (1):
    g0: BSplineCurve PolesCount=5 KnotsCount=3 Degree=3 IsPeriodic=0
FEATURE [PartDesign::AdditiveLoft] AdditiveLoft006
  BaseFeature = -> AdditiveLoft001
  Closed = false
  Placement = pos=(-95.25,284.48,0) rot=(0.995037,0,0.099504;1.5708rad)
  Profile = -> Sketch074
  Ruled = false
  Sections = -> [Sketch075]
FEATURE [PartDesign::Body] Body057
  Origin = -> Origin062
FEATURE [Part::MultiFuse] Fusion014  label="FrontWingFull"
  Placement = pos=(-303.871,139.892,950.921) rot=(0,1,0;3.12414rad)
  Shapes = -> [AdditiveLoft006,Part__Mirroring]
FEATURE [Part::Cut] Cut026
  Base = -> Fusion014
  Tool = -> Fusion012
FEATURE [Part::Cut] Cut027  label="Hollow Wing"
  Base = -> Cut026
  Tool = -> Body054
FEATURE [Part::Cylinder] Cylinder055
  Angle = 360
  AttacherType = Attacher::AttachEngine3D
  FirstAngle = 0
  Height = 10
  Placement = pos=(-38.1,0,0) rot=(0,0,1;0rad)
  Radius = 4
  SecondAngle = 0
FEATURE [Part::MultiFuse] Fusion015  label="Final Front Wing"
  Shapes = -> [Fusion011,Cut027]
FEATURE [App::Part] Part001  label="Front Wing003"
  Group = -> [Body007,Body057,Body048,Body047,Body050,Body049,Body054,Part__Mirroring,Sketch007,Sketch008,Sketch009,Sketch010,Sketch011,Sketch012,Sketch013,Sketch014,AdditiveLoft001,AdditiveLoft,Body015,Body016,Body018,Body020,Cylinder002,Cylinder008,Cylinder053,Cylinder054,Fusion015,Fusion014,Cut027,Fusion011,Cut026,Fusion012,Sketch075,Sketch074,AdditiveLoft006]
  Origin = -> Origin060
FEATURE [Mesh::Feature] Body1
  Placement = pos=(0,71.4375,-122.237) rot=(0,0,1;0rad)
FEATURE [Sketcher::SketchObject] Sketch076  label="Wing110"
  FullyConstrained = false
  Placement = pos=(-95.25,284.48,0) rot=(0.995037,0,0.099504;1.5708rad)
  sketch-geometry (1):
    g0: BSplineCurve PolesCount=5 KnotsCount=3 Degree=3 IsPeriodic=0
FEATURE [Sketcher::SketchObject] Sketch077  label="Wing111"
  FullyConstrained = false
  Placement = pos=(-88.9,279.4,0) rot=(0.998205,0,0.059892;1.5708rad)
  sketch-geometry (1):
    g0: BSplineCurve PolesCount=5 KnotsCount=3 Degree=3 IsPeriodic=0
FEATURE [Sketcher::SketchObject] Sketch078  label="Wing112"
  FullyConstrained = false
  Placement = pos=(-63.5,254,0) rot=(0.999201,0,0.039968;1.5708rad)
  sketch-geometry (1):
    g0: BSplineCurve PolesCount=5 KnotsCount=3 Degree=3 IsPeriodic=0
FEATURE [Sketcher::SketchObject] Sketch079  label="Wing113"
  FullyConstrained = false
  Placement = pos=(-25.4,152.4,0) rot=(0.9998,0,0.019996;1.5708rad)
  sketch-geometry (1):
    g0: BSplineCurve PolesCount=5 KnotsCount=3 Degree=3 IsPeriodic=0
FEATURE [Sketcher::SketchObject] Sketch080  label="Wing114"
  FullyConstrained = false
  Placement = pos=(0,-76.2,0) rot=(1,0,0;1.5708rad)
  sketch-geometry (1):
    g0: BSplineCurve PolesCount=5 KnotsCount=3 Degree=3 IsPeriodic=0
FEATURE [Sketcher::SketchObject] Sketch081  label="Wing1.028"
  FullyConstrained = false
  Placement = pos=(-12.7,50.8,0) rot=(-1,0,0;1.5708rad)
  sketch-geometry (1):
    g0: BSplineCurve PolesCount=5 KnotsCount=3 Degree=3 IsPeriodic=0
FEATURE [Sketcher::SketchObject] Sketch082  label="Wing1.029"
  FullyConstrained = false
  Placement = pos=(-3.81,-25.4,0) rot=(-1,0,0;1.5708rad)
  sketch-geometry (1):
    g0: BSplineCurve PolesCount=5 KnotsCount=3 Degree=3 IsPeriodic=0
FEATURE [Sketcher::SketchObject] Sketch083  label="Wing115"
  FullyConstrained = false
  Placement = pos=(0,-139.7,0) rot=(-1,0,0;1.5708rad)
  sketch-geometry (1):
    g0: BSplineCurve PolesCount=5 KnotsCount=3 Degree=3 IsPeriodic=0
FEATURE [Sketcher::SketchObject] Sketch084  label="Wing116"
  FullyConstrained = false
  Placement = pos=(0,-76.2,0) rot=(1,0,0;1.5708rad)
  sketch-geometry (1):
    g0: BSplineCurve PolesCount=5 KnotsCount=3 Degree=3 IsPeriodic=0
FEATURE [Sketcher::SketchObject] Sketch085  label="Wing117"
  FullyConstrained = false
  Placement = pos=(0,-139.7,0) rot=(-1,0,0;1.5708rad)
  sketch-geometry (1):
    g0: BSplineCurve PolesCount=5 KnotsCount=3 Degree=3 IsPeriodic=0
FEATURE [PartDesign::AdditiveLoft] AdditiveLoft007
  Closed = false
  Placement = pos=(-95.25,284.48,0) rot=(0.995037,0,0.099504;1.5708rad)
  Profile = -> Sketch076 [Edge1]
  Ruled = false
  Sections = -> [Sketch077,Sketch078,Sketch079,Sketch081,Sketch082,Sketch080]
FEATURE [PartDesign::AdditiveLoft] AdditiveLoft008
  BaseFeature = -> AdditiveLoft007
  Closed = false
  Placement = pos=(-95.25,284.48,0) rot=(0.995037,0,0.099504;1.5708rad)
  Profile = -> Sketch080
  Ruled = false
  Sections = -> [Sketch083]
FEATURE [PartDesign::AdditiveLoft] AdditiveLoft009
  BaseFeature = -> AdditiveLoft008
  Closed = false
  Placement = pos=(-95.25,284.48,0) rot=(0.995037,0,0.099504;1.5708rad)
  Profile = -> Sketch084
  Ruled = false
  Sections = -> [Sketch085]
FEATURE [Part::Mirroring] Part__Mirroring002  label="AdditiveLoft001 (Mirror #1)002"
  Base = (0,0,0)
  Normal = (0,0,1)
  Placement = pos=(0,-279.4,3.1e-14) rot=(1,0,0;3.14159rad)
  Source = -> AdditiveLoft008
FEATURE [Part::MultiFuse] Fusion016  label="FrontWingFull001"
  Placement = pos=(-297.784,139.892,951.536) rot=(0,1,0;3.12414rad)
  Shapes = -> [AdditiveLoft009,Part__Mirroring002]
FEATURE [Part::FeaturePython] Clone003  label="BackWing002"  # Draft clone (typed FeaturePython)
  AttacherType = Attacher::AttachEngine3D
  Fuse = false
  Objects = -> [Fusion016]
  Placement = pos=(-150.428,69.946,476.077) rot=(0,1,0;3.19395rad)
  Scale = (0.5,0.5,0.5)
FEATURE [Mesh::Feature] battery_new_v1  label="battery new v1"
FEATURE [App::Part] Part003  label="Fuselage002"
  Group = -> [battery_new_v1,Body009]
  Origin = -> Origin064
FEATURE [Sketcher::SketchObject] Sketch086
  FullyConstrained = true
  MapMode = 5
  Placement = pos=(0,0,0) rot=(1,0,0;1.5708rad)
  Support = -> [XZ_Plane066]
  sketch-geometry (4):
    g0: LineSegment StartX=0 StartY=0 StartZ=0 EndX=13.716 EndY=0 EndZ=0
    g1: LineSegment StartX=13.716 StartY=0 StartZ=0 EndX=13.716 EndY=-13.716 EndZ=0
    g2: LineSegment StartX=13.716 StartY=-13.716 StartZ=0 EndX=0 EndY=-13.716 EndZ=0
    g3: LineSegment StartX=0 StartY=-13.716 StartZ=0 EndX=0 EndY=0 EndZ=0
  constraints (11):
    c: Coincident(g0,g1)
    c: Coincident(g1,g2)
    c: Coincident(g2,g3)
    c: Coincident(g3,g0)
    c: Horizontal(g0)
    c: Horizontal(g2)
    c: Vertical(g1)
    c: Vertical(g3)
    c: Coincident(g0,g-1)
    c: DistanceX(g2,g1) = 13.716
    c: DistanceY(g2,g0) = 13.716
FEATURE [PartDesign::Pad] Pad043
  Direction = (0,-1,-2e-16)
  Length = 50.8
  Length2 = 10
  Placement = pos=(0,0,0) rot=(1,0,0;1.5708rad)
  Profile = -> Sketch086
  ReferenceAxis = -> Sketch086 [N_Axis]
  Type = 0
FEATURE [Part::Cylinder] Cylinder057
  Angle = 360
  AttacherType = Attacher::AttachEngine3D
  FirstAngle = 0
  Height = 206.375
  Placement = pos=(160.02,-103.188,906.276) rot=(-1,0,0;1.5708rad)
  Radius = 3.429
  SecondAngle = 0
FEATURE [Part::Cylinder] Cylinder058
  Angle = 360
  AttacherType = Attacher::AttachEngine3D
  FirstAngle = 0
  Height = 257.175
  Placement = pos=(182.88,-128.588,906.272) rot=(-1,0,0;1.5708rad)
  Radius = 3.429
  SecondAngle = 0
FEATURE [Part::Cylinder] Cylinder059
  Angle = 360
  AttacherType = Attacher::AttachEngine3D
  FirstAngle = 0
  Height = 355.6
  Placement = pos=(201.422,-177.8,905.256) rot=(-1,0,0;1.5708rad)
  Radius = 1.778
  SecondAngle = 0
  expr: .Placement.Base.z = 2.97 '
FEATURE [Part::MultiFuse] Fusion018  label="Back Wing Support"
  Placement = pos=(-353.263,0,-433.426) rot=(0,0,1;0rad)
  Shapes = -> [Cylinder004,Cylinder005,Cylinder006,Cylinder007,Body017]
FEATURE [App::DocumentObjectGroup] Group003  label="BackWing Support"
  Group = -> [Cylinder005,Fusion018]
FEATURE [Part::Box] Box024  label="Cube024"
  AttacherType = Attacher::AttachEngine3D
  Height = 3
  Length = 9.525
  Placement = pos=(1.62052,1.55448,0) rot=(0,0,1;0rad)
  Width = 9.525
FEATURE [Part::Cylinder] Cylinder060
  Angle = 360
  AttacherType = Attacher::AttachEngine3D
  FirstAngle = 0
  Height = 3
  Placement = pos=(6.35,6.35,0) rot=(0,0,1;0rad)
  Radius = 3
  SecondAngle = 0
FEATURE [Part::Cut] Cut029  label="M6 Nut001"
  Base = -> Box024
  Placement = pos=(141.732,-6.38048,903.3) rot=(0,0,1;0rad)
  Refine = true
  Tool = -> Cylinder060
FEATURE [Part::Box] Box025  label="Cube025"
  AttacherType = Attacher::AttachEngine3D
  Height = 3
  Length = 9.525
  Placement = pos=(1.62052,1.55448,0) rot=(0,0,1;0rad)
  Width = 9.525
FEATURE [Part::Cylinder] Cylinder061
  Angle = 360
  AttacherType = Attacher::AttachEngine3D
  FirstAngle = 0
  Height = 3
  Placement = pos=(6.35,6.35,0) rot=(0,0,1;0rad)
  Radius = 3
  SecondAngle = 0
FEATURE [Part::Cut] Cut030  label="M6 Nut002"
  Base = -> Box025
  Placement = pos=(165.278,-6.38048,903.3) rot=(0,0,1;0rad)
  Refine = true
  Tool = -> Cylinder061
FEATURE [Part::Cylinder] Cylinder062
  Angle = 360
  AttacherType = Attacher::AttachEngine3D
  FirstAngle = 0
  Height = 25
  Radius = 3
  SecondAngle = 0
FEATURE [Part::Cylinder] Cylinder063
  Angle = 360
  AttacherType = Attacher::AttachEngine3D
  FirstAngle = 0
  Height = 1.3
  Radius = 6
  SecondAngle = 0
FEATURE [Part::MultiFuse] Fusion019
  Shapes = -> [Cylinder062,Cylinder063]
FEATURE [Part::RegularPolygon] RegularPolygon010  label="Regular polygon010"
  AttacherType = Attacher::AttachEngine3D
  Circumradius = 2.5
  Polygon = 6
FEATURE [Part::Extrusion] Extrude010
  Base = -> RegularPolygon010
  Dir = (0,0,1)
  DirMode = 2
  FaceMakerClass = Part::FaceMakerBullseye
  LengthFwd = 2.5
  LengthRev = 0
  Solid = true
  Symmetric = false
  TaperAngle = -3
FEATURE [Part::Cut] Cut031  label="M6 25mm001"
  Base = -> Fusion019
  Placement = pos=(148.031,0,928.472) rot=(0,1,0;3.14159rad)
  Tool = -> Extrude010
FEATURE [Part::Cylinder] Cylinder064
  Angle = 360
  AttacherType = Attacher::AttachEngine3D
  FirstAngle = 0
  Height = 25
  Radius = 3
  SecondAngle = 0
FEATURE [Part::Cylinder] Cylinder065
  Angle = 360
  AttacherType = Attacher::AttachEngine3D
  FirstAngle = 0
  Height = 1.3
  Radius = 6
  SecondAngle = 0
FEATURE [Part::MultiFuse] Fusion020
  Shapes = -> [Cylinder064,Cylinder065]
FEATURE [Part::RegularPolygon] RegularPolygon011  label="Regular polygon011"
  AttacherType = Attacher::AttachEngine3D
  Circumradius = 2.5
  Polygon = 6
FEATURE [Part::Extrusion] Extrude011
  Base = -> RegularPolygon011
  Dir = (0,0,1)
  DirMode = 2
  FaceMakerClass = Part::FaceMakerBullseye
  LengthFwd = 2.5
  LengthRev = 0
  Solid = true
  Symmetric = false
  TaperAngle = -3
FEATURE [Part::Cut] Cut032  label="M6 25mm002"
  Base = -> Fusion020
  Placement = pos=(171.552,0,928.472) rot=(0,1,0;3.14159rad)
  Tool = -> Extrude011
FEATURE [Part::MultiFuse] Fusion021  label="BackWingFasteners"
  Placement = pos=(-353.263,0,-433.426) rot=(0,0,1;0rad)
  Shapes = -> [Cut032,Cut031,Cut030,Cut029]
FEATURE [Part::Feature] Part__Feature007  label="SINGLE v2"
  Placement = pos=(0,0,-207.962) rot=(0,0,1;0rad)
  shape: bbox 23.5 x 4 x 23.5 mm, 6 faces (baked)
FEATURE [Part::Feature] Part__Feature008  label="SINGLE v003"
  Placement = pos=(0,0,-274.637) rot=(0,0,1;0rad)
  shape: bbox 23.5 x 7 x 23.5 mm, 6 faces (baked)
FEATURE [PartDesign::FeatureBase] BaseFeature001
  BaseFeature = -> Part__Feature008
FEATURE [PartDesign::Body] Body059
  BaseFeature = -> Part__Feature008
  Group = -> [BaseFeature001]
  Origin = -> Origin068
  Tip = -> BaseFeature001
FEATURE [Part::Cylinder] Cylinder066
  Angle = 360
  AttacherType = Attacher::AttachEngine3D
  FirstAngle = 0
  Height = 914.4
  Placement = pos=(40.64,0,-95.54) rot=(0,0,1;0rad)
  Radius = 7.6
  SecondAngle = 0
FEATURE [Part::Box] Box026  label="Cube026"
  AttacherType = Attacher::AttachEngine3D
  Height = 10
  Length = 10.0076
  Placement = pos=(650.293,-21.59,1327.73) rot=(0,-1,0;0.785398rad)
  Width = 50.8
FEATURE [App::Part] Part005
  Group = -> [Body059,Box026]
  Origin = -> Origin067
  Placement = pos=(0,0,-134.938) rot=(0,0,1;0rad)
FEATURE [Part::Chamfer] Chamfer
  Base = -> Pad043
  Edges = 1 edges r=1: [Edge9]
FEATURE [Part::Chamfer] Chamfer001
  Base = -> Pad043
  Edges = 1 edges r=1.016: [Edge9]
FEATURE [Part::Chamfer] Chamfer002
  Base = -> Pad043
  Edges = 1 edges r=1: [Edge9]
FEATURE [PartDesign::Body] AdditiveLoft001Body
  Origin = -> Origin070
FEATURE [App::Part] Part006
  Group = -> [AdditiveLoft001Body]
  Origin = -> Origin069
FEATURE [PartDesign::Body] Body060
  Origin = -> Origin071
FEATURE [PartDesign::Chamfer] Chamfer003
  Angle = 45
  Base = -> Pad043 [Edge9]
  BaseFeature = -> Pad043
  ChamferType = 1
  FlipDirection = false
  Placement = pos=(0,0,0) rot=(1,0,0;1.5708rad)
  Size = 8.89
  Size2 = 2.032
  SupportTransform = false
  UseAllEdges = false
FEATURE [App::MeasureDistance] Distance  label="Distance: 41.681 thou"
  Distance = 1.05869
  P1 = (359.991,177.8,905.067)
  P2 = (359.998,177.675,904.016)
FEATURE [PartDesign::Chamfer] Chamfer004
  Angle = 45
  Base = -> Chamfer003 [Edge7]
  BaseFeature = -> Chamfer003
  ChamferType = 1
  FlipDirection = false
  Placement = pos=(0,0,0) rot=(1,0,0;1.5708rad)
  Size = 5.08
  Size2 = 1.016
  SupportTransform = false
  UseAllEdges = false
FEATURE [PartDesign::Body] Body058
  Group = -> [Sketch086,Pad043,Chamfer003,Chamfer004]
  Origin = -> Origin065
  Placement = pos=(139.7,-6.858,914.908) rot=(0,0,1;1.5708rad)
  Tip = -> Chamfer004
FEATURE [Part::MultiFuse] Fusion017  label="Back Wing Sub"
  Placement = pos=(-353.263,0,-433.426) rot=(0,0,1;0rad)
  Shapes = -> [Cylinder059,Cylinder058,Cylinder057,Body058]
FEATURE [Part::Cut] Cut028  label="BackWingHollow"
  Base = -> Clone003
  Tool = -> Fusion017
FEATURE [App::DocumentObjectGroup] Group020  label="Back Wing Subtract"
  Group = -> [Cut028]
FEATURE [App::Part] Part002  label="Back Wing"
  Group = -> [Part__Mirroring002,Sketch077,Sketch079,Sketch080,Sketch076,Sketch078,Sketch085,Sketch081,Sketch084,Sketch083,Sketch082,AdditiveLoft009,AdditiveLoft007,AdditiveLoft008,Fusion016,Group020,Group003,Body017,Cylinder004,Cylinder005,Cylinder006,Cylinder007,Fusion018,Body058,Clone003,Fusion017,Cylinder059,Cylinder058,Cylinder057,Cut028,Fusion020,Cut030,Cut031,Fusion019,Cut029,Cut032,Cylinder063,+12 more]
  Origin = -> Origin063
  Placement = pos=(353.162,0,435.013) rot=(0,0,1;0rad)
FEATURE [App::Part] Part004  label="Bottom Attachment"
  Group = -> [Part003,Part002,Part001]
  Origin = -> Origin066
  Placement = pos=(158.75,0,0) rot=(0,0,1;0rad)
FEATURE [App::MeasureDistance] Distance001  label="Distance: 24.756 thou"
  Distance = 0.628798
  P1 = (346.1,5.21184,902.78)
  P2 = (345.883,5.21184,902.19)
FEATURE [Mesh::Feature] Fore_mast_clamp_v4
  Placement = pos=(55.0362,-30.6666,860.156) rot=(0.57735,0.57735,-0.57735;4.18879rad)
FEATURE [Mesh::Feature] Aft_mast_clamp_v4
  Placement = pos=(88.9,-27.3309,862.322) rot=(-0.57735,-0.57735,0.57735;2.0944rad)
FEATURE [Part::Feature] Part__Feature009  label="Tail support FR clocked vertical"
  shape: bbox 70.89 x 43.63 x 168.7 mm, 166 faces (baked)
FEATURE [Part::Feature] Part__Feature010  label="Tail support FR clocked vertical001"
  shape: bbox 45.5 x 41.7 x 20.75 mm, 65 faces (baked)
FEATURE [App::Part] Tail_support_FR_clocked_vertical  label="Tail support FR clocked vertical002"
  Group = -> [Part__Feature009,Part__Feature010]
  Origin = -> Origin072
  Placement = pos=(181.61,-4.03e-14,817.88) rot=(0,0,1;4.71239rad)
FEATURE [Sketcher::SketchObject] Sketch
  FullyConstrained = true
  MapMode = 5
  Placement = pos=(0,0,0) rot=(0.57735,0.57735,0.57735;2.0944rad)
  Support = -> [YZ_Plane074]
  sketch-geometry (1):
    g0: Circle CenterX=0 CenterY=0 CenterZ=0 NormalX=0 NormalY=0 NormalZ=1 AngleXU=0 Radius=28.5
  constraints (2):
    c: Coincident(g0,g-1)
    c: Radius(g0) = 28.5
FEATURE [PartDesign::Plane] DatumPlane
  AttachmentOffset = pos=(0,0,25.4) rot=(0,0,1;0rad)
  Length = 73.1303
  MapMode = 11
  Placement = pos=(25.4,-5.6e-15,5.6e-15) rot=(0.707107,0,0.707107;3.14159rad)
  ResizeMode = 0
  Support = -> [Sketch]
  Width = 73.156
FEATURE [Sketcher::SketchObject] Sketch087
  FullyConstrained = true
  MapMode = 5
  Placement = pos=(25.4,-5.6e-15,5.6e-15) rot=(0.707107,0,0.707107;3.14159rad)
  Support = -> [DatumPlane]
  sketch-geometry (1):
    g0: Circle CenterX=0 CenterY=0 CenterZ=0 NormalX=0 NormalY=0 NormalZ=1 AngleXU=0 Radius=30.5
  constraints (2):
    c: Coincident(g0,g-1)
    c: Radius(g0) = 30.5
FEATURE [PartDesign::AdditiveLoft] AdditiveLoft010
  Closed = false
  Midplane = true
  Placement = pos=(0,0,0) rot=(0.57735,0.57735,0.57735;2.0944rad)
  Profile = -> Sketch
  Ruled = false
  Sections = -> [Sketch087]
FEATURE [PartDesign::Plane] DatumPlane001
  AttachmentOffset = pos=(0,0,25.4) rot=(0,0,1;0rad)
  Length = 73.1303
  MapMode = 5
  Placement = pos=(50.8,-1.13e-14,1.13e-14) rot=(0.707107,0,0.707107;3.14159rad)
  ResizeMode = 0
  Support = -> [DatumPlane]
  Width = 73.156
FEATURE [Sketcher::SketchObject] Sketch089
  FullyConstrained = true
  MapMode = 5
  Placement = pos=(50.8,-1.13e-14,1.13e-14) rot=(0.707107,0,0.707107;3.14159rad)
  Support = -> [DatumPlane001]
  sketch-geometry (1):
    g0: Circle CenterX=0 CenterY=0 CenterZ=0 NormalX=0 NormalY=0 NormalZ=1 AngleXU=0 Radius=30.5
  constraints (2):
    c: Coincident(g0,g-1)
    c: Radius(g0) = 30.5
FEATURE [Sketcher::SketchObject] Sketch090
  FullyConstrained = true
  MapMode = 5
  Placement = pos=(0,0,0) rot=(1,0,0;1.5708rad)
  Support = -> [XZ_Plane076]
  sketch-geometry (18):
    g0-g3: Circle x4 (B-spline internal-alignment scaffolding for g4; pole/knot coordinates omitted)
    g4: BSplineCurve PolesCount=4 KnotsCount=2 Degree=3 IsPeriodic=0
    g5: GeomPoint X=-107.949 Y=0 Z=0
    g6: GeomPoint X=0 Y=33 Z=0
    g7: LineSegment StartX=-107.949 StartY=0 StartZ=0 EndX=-105.949 EndY=0 EndZ=0
    g8-g11: Circle x4 (B-spline internal-alignment scaffolding for g12; pole/knot coordinates omitted)
    g12: BSplineCurve PolesCount=4 KnotsCount=2 Degree=3 IsPeriodic=0
    g13: GeomPoint X=-105.949 Y=0 Z=0
    g14: GeomPoint X=0 Y=31 Z=0
    g15: LineSegment StartX=0 StartY=33 StartZ=0 EndX=157.558 EndY=33 EndZ=0
    g16: LineSegment StartX=0 StartY=31 StartZ=0 EndX=157.558 EndY=31 EndZ=0
    g17: LineSegment StartX=157.558 StartY=33 StartZ=0 EndX=157.558 EndY=31 EndZ=0
  constraints (40):
    c: Weight(g0) = 1
    c: PointOnObject(g4,g-1)
    c: Equal(g0,g1)
    c: Equal(g0,g2)
    c: Equal(g0,g3)
    c: PointOnObject(g4,g-2)
    c: InternalAlignment(g0-g3 -> g4) x4
    c: InternalAlignment(g5,g4)
    c: InternalAlignment(g6,g4)
    c: Coincident(g7,g4)
    c: Coincident(g12,g7)
    c: Equal(g8,g9)
    c: Equal(g8,g10)
    c: Equal(g8,g11)
    c: PointOnObject(g12,g-2)
    c: InternalAlignment(g8-g11 -> g12) x4
    c: InternalAlignment(g13,g12)
    c: InternalAlignment(g14,g12)
    c: DistanceX(g2,g10) = 0
    c: DistanceY(g12,g4) = 2
    c: DistanceY(g7,g-1) = 0
    c: DistanceX(g4,g7) = 2
    c: Coincident(g15,g4)
    c: Horizontal(g15)
    c: Coincident(g16,g12)
    c: Horizontal(g16)
    c: Coincident(g17,g15)
    c: Coincident(g17,g16)
    c: Vertical(g17)
    c: DistanceY(g7,g4) = 33
    c: DistanceX(g4) = -107.949
    c: DistanceX(g15) = 157.558
    c: DistanceX(g9,g2) = 50.713
    c: Weight(g8) = 1
    c: DistanceY(g10,g2) = 2
    c: DistanceX(g9) = -100.396
    c: DistanceX(g1) = -101.315
    c: DistanceY(g-1,g2) = 31.7754
    c: DistanceY(g9,g1) = 2.7686
    c: DistanceY(g4,g1) = 19.6088
FEATURE [PartDesign::Revolution] Revolution
  Angle = 360
  Axis = (1,0,0)
  Base = (0,0,0)
  Placement = pos=(0,0,0) rot=(1,0,0;1.5708rad)
  Profile = -> Sketch090
  ReferenceAxis = -> Sketch090 [H_Axis]
FEATURE [PartDesign::Body] Body062
  Group = -> [Sketch090,Revolution]
  Origin = -> Origin075
  Tip = -> Revolution
FEATURE [Part::Feature] Nose_cone_v005_solid  label="Nose_cone_v005 (Solid)"
  shape: bbox 65.49 x 65.5 x 154.5 mm, 26990 faces (baked)
FEATURE [Part::Refine] Nose_cone_v005_solid001  label="Nose_cone_v005 (Solid)001"
  Placement = pos=(0,0,0) rot=(0,1,0;4.71239rad)
  Source = -> Nose_cone_v005_solid
FEATURE [PartDesign::FeatureBase] BaseFeature002
  BaseFeature = -> Nose_cone_v005_solid001
FEATURE [PartDesign::Body] Body063
  BaseFeature = -> Nose_cone_v005_solid001
  Group = -> [BaseFeature002]
  Origin = -> Origin078
  Placement = pos=(62.4632,-31.9022,817.713) rot=(0.57735,0.57735,-0.57735;4.18879rad)
  Tip = -> BaseFeature002
FEATURE [PartDesign::Body] AdditiveLoft001Body001
  Origin = -> Origin081
FEATURE [App::Part] Part008
  Group = -> [AdditiveLoft001Body001]
  Origin = -> Origin080
FEATURE [PartDesign::AdditiveLoft] AdditiveLoft011
  BaseFeature = -> AdditiveLoft010
  Closed = false
  Placement = pos=(0,0,0) rot=(0.57735,0.57735,0.57735;2.0944rad)
  Profile = -> Sketch087
  Ruled = false
  Sections = -> [Sketch089]
FEATURE [PartDesign::Body] Body061
  Group = -> [Sketch,DatumPlane,Sketch087,AdditiveLoft010,DatumPlane001,Sketch089,AdditiveLoft011]
  Origin = -> Origin074
  Placement = pos=(217.627,0,0) rot=(0,0,1;0rad)
  Tip = -> AdditiveLoft011
FEATURE [PartDesign::Body] Body064
  Origin = -> Origin082
  Placement = pos=(0,14.3,14.3) rot=(0,0,1;0rad)
FEATURE [Part::Cylinder] Cylinder067
  Angle = 360
  AttacherType = Attacher::AttachEngine3D
  FirstAngle = 0
  Height = 200
  Placement = pos=(311.15,14.3,14.3) rot=(0,1,0;1.5708rad)
  Radius = 2.1
  SecondAngle = 0
FEATURE [PartDesign::FeatureBase] Clone
  BaseFeature = -> Cylinder067
  Placement = pos=(311.15,0,0) rot=(0,1,0;1.5708rad)
FEATURE [PartDesign::Body] Body065
  Group = -> [Clone]
  Origin = -> Origin083
  Placement = pos=(0,14.3,-14.3) rot=(0,0,1;0rad)
  Tip = -> Clone
FEATURE [PartDesign::FeatureBase] Clone004
  BaseFeature = -> Cylinder067
  Placement = pos=(311.15,0,0) rot=(0,1,0;1.5708rad)
FEATURE [PartDesign::Body] Body066
  Group = -> [Clone004]
  Origin = -> Origin084
  Placement = pos=(0,-14.3,-14.3) rot=(0,0,1;0rad)
  Tip = -> Clone004
FEATURE [PartDesign::FeatureBase] Clone005
  BaseFeature = -> Body065
FEATURE [PartDesign::Body] Body067
  Group = -> [Clone005]
  Origin = -> Origin085
  Placement = pos=(0,-14.3,14.3) rot=(0,0,1;0rad)
  Tip = -> Clone005
FEATURE [Part::Compound] Compound006  label="screw holes"
  Links = -> [Body067,Body066,Body065,Cylinder067,Body064]
FEATURE [App::DocumentObjectGroup] Group021  label="Group"
FEATURE [Part::Cylinder] Cylinder068
  Angle = 360
  AttacherType = Attacher::AttachEngine3D
  FirstAngle = 0
  Height = 40
  Placement = pos=(416.077,0,0) rot=(0,1,0;1.5708rad)
  Radius = 33
  SecondAngle = 0
FEATURE [Part::Feature] Part__Feature011  label="Tail support FR clocked vertical003"
  Placement = pos=(525.78,-1.17e-13,0) rot=(0,0,-1;1.5708rad)
  shape: bbox 43.63 x 70.89 x 168.7 mm, 166 faces (baked)
FEATURE [Part::Box] Box027  label="Cube027"
  AttacherType = Attacher::AttachEngine3D
  Height = 50
  Length = 50
  Placement = pos=(520.7,-25.4,81.28) rot=(0,0,1;0rad)
  Width = 50
FEATURE [Part::Cut] Cut034
  Base = -> Part__Feature011
  Refine = true
  Tool = -> Box027
FEATURE [Part::Box] Box028  label="Cube028"
  AttacherType = Attacher::AttachEngine3D
  Height = 35
  Length = 38
  Placement = pos=(534.67,-17.5,95.25) rot=(0,0,1;0rad)
  Width = 35
FEATURE [Part::Box] Box029  label="Cube029"
  AttacherType = Attacher::AttachEngine3D
  Height = 19.558
  Length = 50
  Placement = pos=(528.17,-9.779,103.467) rot=(0,0,1;0rad)
  Width = 19.558
FEATURE [Part::Cut] Cut035
  Base = -> Box028
  Placement = pos=(-10.3,0,-16.6) rot=(0,0,1;0rad)
  Refine = true
  Tool = -> Box029
FEATURE [Part::Fillet] Fillet004
  Base = -> Cut035
  Edges = 4 edges r=5: [Edge9,Edge11,Edge12,Edge14]
FEATURE [Part::Fillet] Fillet005
  Base = -> Fillet004
  Edges = 2 edges r=3: [Edge4,Edge20]
FEATURE [Part::Cylinder] Cylinder069
  Angle = 360
  AttacherType = Attacher::AttachEngine3D
  FirstAngle = 0
  Height = 100
  Placement = pos=(543.2,13.75,60) rot=(0,0,1;0rad)
  Radius = 1.6
  SecondAngle = 0
FEATURE [Part::Mirroring] Part__Mirroring003  label="Cylinder069 (Mirror #4)"
  Base = (0,0,0)
  Normal = (0,1,0)
  Source = -> Cylinder069
FEATURE [Part::Cut] Cut036
  Base = -> Fillet005
  Refine = true
  Tool = -> Cylinder069
FEATURE [Part::Cut] Cut037
  Base = -> Cut036
  Refine = true
  Tool = -> Part__Mirroring003
FEATURE [Part::Box] Box030  label="Cube030"
  AttacherType = Attacher::AttachEngine3D
  Height = 35
  Length = 38
  Placement = pos=(534.67,-17.5,95.25) rot=(0,0,1;0rad)
  Width = 35
FEATURE [Part::Box] Box031  label="Cube031"
  AttacherType = Attacher::AttachEngine3D
  Height = 19.558
  Length = 50
  Placement = pos=(528.17,-9.779,103.467) rot=(0,0,1;0rad)
  Width = 19.558
FEATURE [Part::Cut] Cut038
  Base = -> Box030
  Placement = pos=(-10.3,0,-16.6) rot=(0,0,1;0rad)
  Refine = true
  Tool = -> Box031
FEATURE [Part::Cylinder] Cylinder070
  Angle = 360
  AttacherType = Attacher::AttachEngine3D
  FirstAngle = 0
  Height = 100
  Placement = pos=(543.2,13.75,60) rot=(0,0,1;0rad)
  Radius = 1.6
  SecondAngle = 0
FEATURE [Part::Fillet] Fillet006
  Base = -> Cut038
  Edges = 4 edges r=5: [Edge9,Edge11,Edge12,Edge14]
FEATURE [Part::Fillet] Fillet007
  Base = -> Fillet006
  Edges = 2 edges r=3: [Edge4,Edge20]
FEATURE [Part::Cut] Cut039
  Base = -> Fillet007
  Refine = true
  Tool = -> Cylinder070
FEATURE [Part::Mirroring] Part__Mirroring004  label="Cylinder069 (Mirror #4)001"
  Base = (0,0,0)
  Normal = (0,1,0)
  Source = -> Cylinder070
FEATURE [Part::MultiFuse] Fusion022
  Refine = true
  Shapes = -> [Cut037,Cut034]
FEATURE [App::Part] Part007  label="Motor Holder"
  Group = -> [Body061,Body062,Body064,Cylinder067,Body065,Body066,Body067,Compound006,Cylinder068,Part__Feature011,Box027,Box029,Box028,Fillet004,Fillet005,Cut035,Cut036,Cut037,Cut034,Part__Mirroring003,Cylinder069,Fusion022]
  Origin = -> Origin073
  Placement = pos=(0,-163.83,802.64) rot=(0,0,1;0rad)
FEATURE [Part::Box] Box032  label="Cube032"
  AttacherType = Attacher::AttachEngine3D
  Height = 50
  Length = 50
  Placement = pos=(520.7,-25.4,81.28) rot=(0,0,1;0rad)
  Width = 50
FEATURE [Part::Box] Box033  label="Cube033"
  AttacherType = Attacher::AttachEngine3D
  Height = 35
  Length = 38
  Placement = pos=(534.67,-17.5,95.25) rot=(0,0,1;0rad)
  Width = 35
FEATURE [Part::Box] Box034  label="Cube034"
  AttacherType = Attacher::AttachEngine3D
  Height = 19.558
  Length = 50
  Placement = pos=(528.17,-9.779,103.467) rot=(0,0,1;0rad)
  Width = 19.558
FEATURE [Part::Cut] Cut042
  Base = -> Box033
  Placement = pos=(-10.3,0,-16.6) rot=(0,0,1;0rad)
  Refine = true
  Tool = -> Box034
FEATURE [Part::Cylinder] Cylinder071
  Angle = 360
  AttacherType = Attacher::AttachEngine3D
  FirstAngle = 0
  Height = 100
  Placement = pos=(543.2,13.75,60) rot=(0,0,1;0rad)
  Radius = 1.6
  SecondAngle = 0
FEATURE [Part::Fillet] Fillet008
  Base = -> Cut042
  Edges = 4 edges r=5: [Edge9,Edge11,Edge12,Edge14]
FEATURE [Part::Fillet] Fillet009
  Base = -> Fillet008
  Edges = 2 edges r=3: [Edge4,Edge20]
FEATURE [Part::Cut] Cut043
  Base = -> Fillet009
  Refine = true
  Tool = -> Cylinder071
FEATURE [Part::Feature] Part__Feature012  label="Tail support FR clocked vertical004"
  Placement = pos=(525.78,-1.17e-13,0) rot=(0,0,-1;1.5708rad)
  shape: bbox 43.63 x 70.89 x 168.7 mm, 166 faces (baked)
FEATURE [Part::Cut] Cut041
  Base = -> Part__Feature012
  Refine = true
  Tool = -> Box032
FEATURE [Part::Mirroring] Part__Mirroring005  label="Cylinder069 (Mirror #4)002"
  Base = (0,0,0)
  Normal = (0,1,0)
  Source = -> Cylinder071
FEATURE [Part::Cut] Cut044
  Base = -> Cut043
  Refine = true
  Tool = -> Part__Mirroring005
FEATURE [Part::MultiFuse] Fusion023
  Placement = pos=(-386.75,0,828.75) rot=(0,0,1;0rad)
  Refine = true
  Shapes = -> [Cut044,Cut041]
FEATURE [Part::Cylinder] Cylinder072
  Angle = 360
  AttacherType = Attacher::AttachEngine3D
  FirstAngle = 0
  Height = 40
  Placement = pos=(0,0,0) rot=(0,1,0;1.5708rad)
  Radius = 32.8
  SecondAngle = 0
FEATURE [Part::Box] Box035  label="Cube035"
  AttacherType = Attacher::AttachEngine3D
  Height = 70
  Length = 60
  Placement = pos=(0,6.32888,-34.9807) rot=(0,0,1;0rad)
  Width = 70
FEATURE [Part::Mirroring] Part__Mirroring006  label="Cube035 (Mirror #7)"
  Base = (0,0,0)
  Normal = (0,1,0)
  Source = -> Box035
FEATURE [Part::MultiFuse] Fusion024
  Refine = true
  Shapes = -> [Box035,Part__Mirroring006]
FEATURE [Part::Cut] Cut045
  Base = -> Cylinder072
  Placement = pos=(48.8969,0,829.591) rot=(0,0,1;0rad)
  Refine = true
  Tool = -> Fusion024
FEATURE [Part::Feature] Aft_mast_clamp_v005_solid  label="Aft_mast_clamp_v005 (Solid)"
  shape: bbox 40 x 60.15 x 65.5 mm, 9906 faces (baked)
FEATURE [Part::Refine] Aft_mast_clamp_v005_solid001  label="Aft_mast_clamp_v005 (Solid)001"
  Source = -> Aft_mast_clamp_v005_solid
FEATURE [Part::MultiFuse] Fusion025  label="aft mast clamp fixed"
  Placement = pos=(0,-0.14,-0.72) rot=(0,0,1;0rad)
  Refine = true
  Shapes = -> [Aft_mast_clamp_v005_solid001,Cut045]
FEATURE [Part::Feature] Fore_mast_clamp_v005_solid  label="Fore_mast_clamp_v005 (Solid)"
  shape: bbox 25 x 61.3 x 61.3 mm, 6348 faces (baked)
FEATURE [Part::Refine] Fore_mast_clamp_v005_solid001  label="Fore_mast_clamp_v005 (Solid)001"
  Placement = pos=(-0.55,-0.04,-0.65) rot=(0,0,1;0rad)
  Source = -> Fore_mast_clamp_v005_solid
FEATURE [Part::Torus] Torus
  Angle1 = -180
  Angle2 = 180
  Angle3 = 360
  AttacherType = Attacher::AttachEngine3D
  Placement = pos=(38.21,-64.65,748.03) rot=(0,1,0;1.5708rad)
  Radius1 = 10
  Radius2 = 7.6
FEATURE [Part::Box] Box036  label="Cube036"
  AttacherType = Attacher::AttachEngine3D
  Height = 40
  Length = 20
  Placement = pos=(29.25,-64.67,728.42) rot=(0,0,1;0rad)
  Width = 20
FEATURE [Part::MultiCommon] Common
  Placement = pos=(2.44,737.99,883.53) rot=(1,0,0;1.5708rad)
  Refine = true
  Shapes = -> [Torus,Box036]
FEATURE [Part::Cut] Cut033
  Base = -> Connect001
  Tool = -> Cylinder066
FEATURE [Part::Cut] Cut046
  Base = -> Cut033
  Refine = true
  Tool = -> Common
FEATURE [App::DocumentObjectGroup] Group019  label="Mast Support"
  Group = -> [Body039,Body040,Body041,Body042,Body045,Body046,Cut046]
FEATURE [App::DocumentObjectGroup] Group006  label="Mast Group"
  Group = -> [Box009,Group010,Group012,Cut024,Cut025,Group018,Group019]
FEATURE [PartDesign::Body] AdditiveLoft001Body002
  Origin = -> Origin087
FEATURE [App::Part] Part009
  Group = -> [AdditiveLoft001Body002]
  Origin = -> Origin086
FEATURE [Part::Chamfer] Chamfer005
  Base = -> Cut046
  Edges = 1 edges r=0.75: [Edge123]
FEATURE [Part::Cylinder] Cylinder073
  Angle = 360
  AttacherType = Attacher::AttachEngine3D
  FirstAngle = 0
  Height = 190
  Placement = pos=(100.54,14.78,843.71) rot=(0,1,0;4.71239rad)
  Radius = 2.65
  SecondAngle = 0
FEATURE [Part::Cylinder] Cylinder074
  Angle = 360
  AttacherType = Attacher::AttachEngine3D
  FirstAngle = 0
  Height = 190
  Placement = pos=(100.54,-14.92,814.01) rot=(0,-1,0;1.5708rad)
  Radius = 2.65
  SecondAngle = 0
FEATURE [Part::Cylinder] Cylinder075
  Angle = 360
  AttacherType = Attacher::AttachEngine3D
  FirstAngle = 0
  Height = 190
  Placement = pos=(100.54,14.78,814.01) rot=(0,-1,0;1.5708rad)
  Radius = 2.65
  SecondAngle = 0
FEATURE [Part::Cylinder] Cylinder076
  Angle = 360
  AttacherType = Attacher::AttachEngine3D
  FirstAngle = 0
  Height = 190
  Placement = pos=(100.54,-14.92,843.71) rot=(0,-1,0;1.5708rad)
  Radius = 2.65
  SecondAngle = 0
FEATURE [Part::MultiFuse] Fusion026  label="threaded rods"
  Refine = true
  Shapes = -> [Cylinder073,Cylinder074,Cylinder075,Cylinder076]
FEATURE [Part::Cut] Cut047
  Base = -> Chamfer005
  Refine = true
  Tool = -> Fusion026
